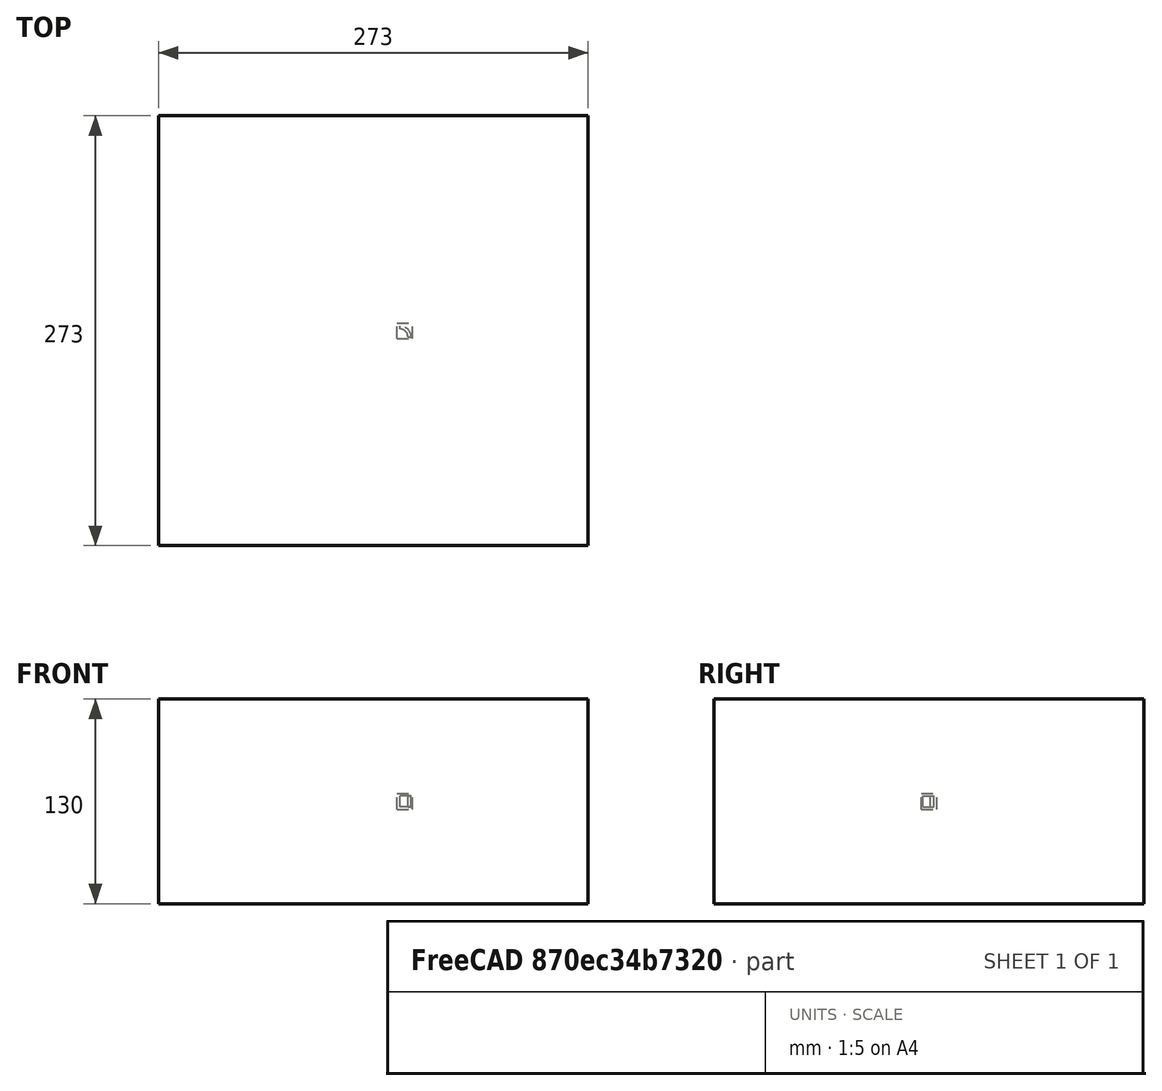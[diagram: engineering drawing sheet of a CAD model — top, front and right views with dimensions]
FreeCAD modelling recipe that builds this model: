
FCSTD DOCUMENT  (FreeCAD 0.21R33694 (Git))
Label: polarArray-of-Part-base-xformed
License: All rights reserved
LicenseURL: http://en.wikipedia.org/wiki/All_rights_reserved
objects: App::DocumentObjectGroupPython×1251, Part::FeaturePython×4, App::Part×4
note: 3 computed .brp shape members not serialized (recipe doc carries the construction recipe); baked Part::Feature solids carry a one-line shape summary decoded from their .brp

FEATURE [App::DocumentObjectGroupPython] HALFPI  # scripted group (container) (typed FeaturePython)
  name = HALFPI
  value = pi/2.
FEATURE [App::DocumentObjectGroupPython] PI  # scripted group (container) (typed FeaturePython)
  name = PI
  value = 1.*pi
FEATURE [App::DocumentObjectGroupPython] TWOPI  # scripted group (container) (typed FeaturePython)
  name = TWOPI
  value = 2.*pi
FEATURE [App::DocumentObjectGroupPython] Constants  # scripted group (container) (typed FeaturePython)
  Group = -> [HALFPI,PI,TWOPI]
FEATURE [App::DocumentObjectGroupPython] Variables  # scripted group (container) (typed FeaturePython)
FEATURE [App::DocumentObjectGroupPython] Quantities  # scripted group (container) (typed FeaturePython)
FEATURE [App::DocumentObjectGroupPython] Isotopes  # scripted group (container) (typed FeaturePython)
FEATURE [App::DocumentObjectGroupPython] Elements  # scripted group (container) (typed FeaturePython)
FEATURE [App::DocumentObjectGroupPython] Matrix  # scripted group (container) (typed FeaturePython)
FEATURE [App::DocumentObjectGroupPython] Surfaces  # scripted group (container) (typed FeaturePython)
FEATURE [App::DocumentObjectGroupPython] Opticals  # scripted group (container) (typed FeaturePython)
  Group = -> [Matrix,Surfaces]
FEATURE [App::DocumentObjectGroupPython] G4Isotopes  # scripted group (container) (typed FeaturePython)
FEATURE [App::DocumentObjectGroupPython] H_element  # scripted group (container) (typed FeaturePython)
  Z = 1
  atom_value = 1.008
  formula = H
  name = H_element
FEATURE [App::DocumentObjectGroupPython] He_element  # scripted group (container) (typed FeaturePython)
  Z = 2
  atom_value = 4.0026
  formula = He
  name = He_element
FEATURE [App::DocumentObjectGroupPython] Li_element  # scripted group (container) (typed FeaturePython)
  Z = 3
  atom_value = 6.94
  formula = Li
  name = Li_element
FEATURE [App::DocumentObjectGroupPython] Be_element  # scripted group (container) (typed FeaturePython)
  Z = 4
  atom_value = 9.01218
  formula = Be
  name = Be_element
FEATURE [App::DocumentObjectGroupPython] B_element  # scripted group (container) (typed FeaturePython)
  Z = 5
  atom_value = 10.81
  formula = B
  name = B_element
FEATURE [App::DocumentObjectGroupPython] C_element  # scripted group (container) (typed FeaturePython)
  Z = 6
  atom_value = 12.011
  formula = C
  name = C_element
FEATURE [App::DocumentObjectGroupPython] N_element  # scripted group (container) (typed FeaturePython)
  Z = 7
  atom_value = 14.007
  formula = N
  name = N_element
FEATURE [App::DocumentObjectGroupPython] O_element  # scripted group (container) (typed FeaturePython)
  Z = 8
  atom_value = 15.999
  formula = O
  name = O_element
FEATURE [App::DocumentObjectGroupPython] F_element  # scripted group (container) (typed FeaturePython)
  Z = 9
  atom_value = 18.9984
  formula = F
  name = F_element
FEATURE [App::DocumentObjectGroupPython] Ne_element  # scripted group (container) (typed FeaturePython)
  Z = 10
  atom_value = 20.1797
  formula = Ne
  name = Ne_element
FEATURE [App::DocumentObjectGroupPython] Na_element  # scripted group (container) (typed FeaturePython)
  Z = 11
  atom_value = 22.9898
  formula = Na
  name = Na_element
FEATURE [App::DocumentObjectGroupPython] Mg_element  # scripted group (container) (typed FeaturePython)
  Z = 12
  atom_value = 24.305
  formula = Mg
  name = Mg_element
FEATURE [App::DocumentObjectGroupPython] Al_element  # scripted group (container) (typed FeaturePython)
  Z = 13
  atom_value = 26.9815
  formula = Al
  name = Al_element
FEATURE [App::DocumentObjectGroupPython] Si_element  # scripted group (container) (typed FeaturePython)
  Z = 14
  atom_value = 28.085
  formula = Si
  name = Si_element
FEATURE [App::DocumentObjectGroupPython] P_element  # scripted group (container) (typed FeaturePython)
  Z = 15
  atom_value = 30.9738
  formula = P
  name = P_element
FEATURE [App::DocumentObjectGroupPython] S_element  # scripted group (container) (typed FeaturePython)
  Z = 16
  atom_value = 32.06
  formula = S
  name = S_element
FEATURE [App::DocumentObjectGroupPython] Cl_element  # scripted group (container) (typed FeaturePython)
  Z = 17
  atom_value = 35.45
  formula = Cl
  name = Cl_element
FEATURE [App::DocumentObjectGroupPython] Ar_element  # scripted group (container) (typed FeaturePython)
  Z = 18
  atom_value = 39.95
  formula = Ar
  name = Ar_element
FEATURE [App::DocumentObjectGroupPython] K_element  # scripted group (container) (typed FeaturePython)
  Z = 19
  atom_value = 39.0983
  formula = K
  name = K_element
FEATURE [App::DocumentObjectGroupPython] Ca_element  # scripted group (container) (typed FeaturePython)
  Z = 20
  atom_value = 40.078
  formula = Ca
  name = Ca_element
FEATURE [App::DocumentObjectGroupPython] Sc_element  # scripted group (container) (typed FeaturePython)
  Z = 21
  atom_value = 44.9559
  formula = Sc
  name = Sc_element
FEATURE [App::DocumentObjectGroupPython] Ti_element  # scripted group (container) (typed FeaturePython)
  Z = 22
  atom_value = 47.867
  formula = Ti
  name = Ti_element
FEATURE [App::DocumentObjectGroupPython] V_element  # scripted group (container) (typed FeaturePython)
  Z = 23
  atom_value = 50.9415
  formula = V
  name = V_element
FEATURE [App::DocumentObjectGroupPython] Cr_element  # scripted group (container) (typed FeaturePython)
  Z = 24
  atom_value = 51.9961
  formula = Cr
  name = Cr_element
FEATURE [App::DocumentObjectGroupPython] Mn_element  # scripted group (container) (typed FeaturePython)
  Z = 25
  atom_value = 54.938
  formula = Mn
  name = Mn_element
FEATURE [App::DocumentObjectGroupPython] Fe_element  # scripted group (container) (typed FeaturePython)
  Z = 26
  atom_value = 55.845
  formula = Fe
  name = Fe_element
FEATURE [App::DocumentObjectGroupPython] Co_element  # scripted group (container) (typed FeaturePython)
  Z = 27
  atom_value = 58.9332
  formula = Co
  name = Co_element
FEATURE [App::DocumentObjectGroupPython] Ni_element  # scripted group (container) (typed FeaturePython)
  Z = 28
  atom_value = 58.6934
  formula = Ni
  name = Ni_element
FEATURE [App::DocumentObjectGroupPython] Cu_element  # scripted group (container) (typed FeaturePython)
  Z = 29
  atom_value = 63.546
  formula = Cu
  name = Cu_element
FEATURE [App::DocumentObjectGroupPython] Zn_element  # scripted group (container) (typed FeaturePython)
  Z = 30
  atom_value = 65.38
  formula = Zn
  name = Zn_element
FEATURE [App::DocumentObjectGroupPython] Ga_element  # scripted group (container) (typed FeaturePython)
  Z = 31
  atom_value = 69.723
  formula = Ga
  name = Ga_element
FEATURE [App::DocumentObjectGroupPython] Ge_element  # scripted group (container) (typed FeaturePython)
  Z = 32
  atom_value = 72.63
  formula = Ge
  name = Ge_element
FEATURE [App::DocumentObjectGroupPython] As_element  # scripted group (container) (typed FeaturePython)
  Z = 33
  atom_value = 74.9216
  formula = As
  name = As_element
FEATURE [App::DocumentObjectGroupPython] Se_element  # scripted group (container) (typed FeaturePython)
  Z = 34
  atom_value = 78.971
  formula = Se
  name = Se_element
FEATURE [App::DocumentObjectGroupPython] Br_element  # scripted group (container) (typed FeaturePython)
  Z = 35
  atom_value = 79.904
  formula = Br
  name = Br_element
FEATURE [App::DocumentObjectGroupPython] Kr_element  # scripted group (container) (typed FeaturePython)
  Z = 36
  atom_value = 83.798
  formula = Kr
  name = Kr_element
FEATURE [App::DocumentObjectGroupPython] Rb_element  # scripted group (container) (typed FeaturePython)
  Z = 37
  atom_value = 85.4678
  formula = Rb
  name = Rb_element
FEATURE [App::DocumentObjectGroupPython] Sr_element  # scripted group (container) (typed FeaturePython)
  Z = 38
  atom_value = 87.62
  formula = Sr
  name = Sr_element
FEATURE [App::DocumentObjectGroupPython] Y_element  # scripted group (container) (typed FeaturePython)
  Z = 39
  atom_value = 88.9058
  formula = Y
  name = Y_element
FEATURE [App::DocumentObjectGroupPython] Zr_element  # scripted group (container) (typed FeaturePython)
  Z = 40
  atom_value = 91.224
  formula = Zr
  name = Zr_element
FEATURE [App::DocumentObjectGroupPython] Nb_element  # scripted group (container) (typed FeaturePython)
  Z = 41
  atom_value = 92.9064
  formula = Nb
  name = Nb_element
FEATURE [App::DocumentObjectGroupPython] Mo_element  # scripted group (container) (typed FeaturePython)
  Z = 42
  atom_value = 95.95
  formula = Mo
  name = Mo_element
FEATURE [App::DocumentObjectGroupPython] Tc_element  # scripted group (container) (typed FeaturePython)
  Z = 43
  atom_value = 97
  formula = Tc
  name = Tc_element
FEATURE [App::DocumentObjectGroupPython] Ru_element  # scripted group (container) (typed FeaturePython)
  Z = 44
  atom_value = 101.07
  formula = Ru
  name = Ru_element
FEATURE [App::DocumentObjectGroupPython] Rh_element  # scripted group (container) (typed FeaturePython)
  Z = 45
  atom_value = 102.905
  formula = Rh
  name = Rh_element
FEATURE [App::DocumentObjectGroupPython] Pd_element  # scripted group (container) (typed FeaturePython)
  Z = 46
  atom_value = 106.42
  formula = Pd
  name = Pd_element
FEATURE [App::DocumentObjectGroupPython] Ag_element  # scripted group (container) (typed FeaturePython)
  Z = 47
  atom_value = 107.868
  formula = Ag
  name = Ag_element
FEATURE [App::DocumentObjectGroupPython] Cd_element  # scripted group (container) (typed FeaturePython)
  Z = 48
  atom_value = 112.414
  formula = Cd
  name = Cd_element
FEATURE [App::DocumentObjectGroupPython] In_element  # scripted group (container) (typed FeaturePython)
  Z = 49
  atom_value = 114.818
  formula = In
  name = In_element
FEATURE [App::DocumentObjectGroupPython] Sn_element  # scripted group (container) (typed FeaturePython)
  Z = 50
  atom_value = 118.71
  formula = Sn
  name = Sn_element
FEATURE [App::DocumentObjectGroupPython] Sb_element  # scripted group (container) (typed FeaturePython)
  Z = 51
  atom_value = 121.76
  formula = Sb
  name = Sb_element
FEATURE [App::DocumentObjectGroupPython] Te_element  # scripted group (container) (typed FeaturePython)
  Z = 52
  atom_value = 127.6
  formula = Te
  name = Te_element
FEATURE [App::DocumentObjectGroupPython] I_element  # scripted group (container) (typed FeaturePython)
  Z = 53
  atom_value = 126.904
  formula = I
  name = I_element
FEATURE [App::DocumentObjectGroupPython] Xe_element  # scripted group (container) (typed FeaturePython)
  Z = 54
  atom_value = 131.293
  formula = Xe
  name = Xe_element
FEATURE [App::DocumentObjectGroupPython] Cs_element  # scripted group (container) (typed FeaturePython)
  Z = 55
  atom_value = 132.905
  formula = Cs
  name = Cs_element
FEATURE [App::DocumentObjectGroupPython] Ba_element  # scripted group (container) (typed FeaturePython)
  Z = 56
  atom_value = 137.327
  formula = Ba
  name = Ba_element
FEATURE [App::DocumentObjectGroupPython] La_element  # scripted group (container) (typed FeaturePython)
  Z = 57
  atom_value = 138.905
  formula = La
  name = La_element
FEATURE [App::DocumentObjectGroupPython] Ce_element  # scripted group (container) (typed FeaturePython)
  Z = 58
  atom_value = 140.116
  formula = Ce
  name = Ce_element
FEATURE [App::DocumentObjectGroupPython] Pr_element  # scripted group (container) (typed FeaturePython)
  Z = 59
  atom_value = 140.908
  formula = Pr
  name = Pr_element
FEATURE [App::DocumentObjectGroupPython] Nd_element  # scripted group (container) (typed FeaturePython)
  Z = 60
  atom_value = 144.242
  formula = Nd
  name = Nd_element
FEATURE [App::DocumentObjectGroupPython] Pm_element  # scripted group (container) (typed FeaturePython)
  Z = 61
  atom_value = 145
  formula = Pm
  name = Pm_element
FEATURE [App::DocumentObjectGroupPython] Sm_element  # scripted group (container) (typed FeaturePython)
  Z = 62
  atom_value = 150.36
  formula = Sm
  name = Sm_element
FEATURE [App::DocumentObjectGroupPython] Eu_element  # scripted group (container) (typed FeaturePython)
  Z = 63
  atom_value = 151.964
  formula = Eu
  name = Eu_element
FEATURE [App::DocumentObjectGroupPython] Gd_element  # scripted group (container) (typed FeaturePython)
  Z = 64
  atom_value = 157.25
  formula = Gd
  name = Gd_element
FEATURE [App::DocumentObjectGroupPython] Tb_element  # scripted group (container) (typed FeaturePython)
  Z = 65
  atom_value = 158.925
  formula = Tb
  name = Tb_element
FEATURE [App::DocumentObjectGroupPython] Dy_element  # scripted group (container) (typed FeaturePython)
  Z = 66
  atom_value = 162.5
  formula = Dy
  name = Dy_element
FEATURE [App::DocumentObjectGroupPython] Ho_element  # scripted group (container) (typed FeaturePython)
  Z = 67
  atom_value = 164.93
  formula = Ho
  name = Ho_element
FEATURE [App::DocumentObjectGroupPython] Er_element  # scripted group (container) (typed FeaturePython)
  Z = 68
  atom_value = 167.259
  formula = Er
  name = Er_element
FEATURE [App::DocumentObjectGroupPython] Tm_element  # scripted group (container) (typed FeaturePython)
  Z = 69
  atom_value = 168.934
  formula = Tm
  name = Tm_element
FEATURE [App::DocumentObjectGroupPython] Yb_element  # scripted group (container) (typed FeaturePython)
  Z = 70
  atom_value = 173.045
  formula = Yb
  name = Yb_element
FEATURE [App::DocumentObjectGroupPython] Lu_element  # scripted group (container) (typed FeaturePython)
  Z = 71
  atom_value = 174.967
  formula = Lu
  name = Lu_element
FEATURE [App::DocumentObjectGroupPython] Hf_element  # scripted group (container) (typed FeaturePython)
  Z = 72
  atom_value = 178.49
  formula = Hf
  name = Hf_element
FEATURE [App::DocumentObjectGroupPython] Ta_element  # scripted group (container) (typed FeaturePython)
  Z = 73
  atom_value = 180.948
  formula = Ta
  name = Ta_element
FEATURE [App::DocumentObjectGroupPython] W_element  # scripted group (container) (typed FeaturePython)
  Z = 74
  atom_value = 183.84
  formula = W
  name = W_element
FEATURE [App::DocumentObjectGroupPython] Re_element  # scripted group (container) (typed FeaturePython)
  Z = 75
  atom_value = 186.207
  formula = Re
  name = Re_element
FEATURE [App::DocumentObjectGroupPython] Os_element  # scripted group (container) (typed FeaturePython)
  Z = 76
  atom_value = 190.23
  formula = Os
  name = Os_element
FEATURE [App::DocumentObjectGroupPython] Ir_element  # scripted group (container) (typed FeaturePython)
  Z = 77
  atom_value = 192.217
  formula = Ir
  name = Ir_element
FEATURE [App::DocumentObjectGroupPython] Pt_element  # scripted group (container) (typed FeaturePython)
  Z = 78
  atom_value = 195.084
  formula = Pt
  name = Pt_element
FEATURE [App::DocumentObjectGroupPython] Au_element  # scripted group (container) (typed FeaturePython)
  Z = 79
  atom_value = 196.967
  formula = Au
  name = Au_element
FEATURE [App::DocumentObjectGroupPython] Hg_element  # scripted group (container) (typed FeaturePython)
  Z = 80
  atom_value = 200.592
  formula = Hg
  name = Hg_element
FEATURE [App::DocumentObjectGroupPython] Tl_element  # scripted group (container) (typed FeaturePython)
  Z = 81
  atom_value = 204.38
  formula = Tl
  name = Tl_element
FEATURE [App::DocumentObjectGroupPython] Pb_element  # scripted group (container) (typed FeaturePython)
  Z = 82
  atom_value = 207.2
  formula = Pb
  name = Pb_element
FEATURE [App::DocumentObjectGroupPython] Bi_element  # scripted group (container) (typed FeaturePython)
  Z = 83
  atom_value = 208.98
  formula = Bi
  name = Bi_element
FEATURE [App::DocumentObjectGroupPython] Po_element  # scripted group (container) (typed FeaturePython)
  Z = 84
  atom_value = 209
  formula = Po
  name = Po_element
FEATURE [App::DocumentObjectGroupPython] At_element  # scripted group (container) (typed FeaturePython)
  Z = 85
  atom_value = 210
  formula = At
  name = At_element
FEATURE [App::DocumentObjectGroupPython] Rn_element  # scripted group (container) (typed FeaturePython)
  Z = 86
  atom_value = 222
  formula = Rn
  name = Rn_element
FEATURE [App::DocumentObjectGroupPython] Fr_element  # scripted group (container) (typed FeaturePython)
  Z = 87
  atom_value = 223
  formula = Fr
  name = Fr_element
FEATURE [App::DocumentObjectGroupPython] Ra_element  # scripted group (container) (typed FeaturePython)
  Z = 88
  atom_value = 226
  formula = Ra
  name = Ra_element
FEATURE [App::DocumentObjectGroupPython] Ac_element  # scripted group (container) (typed FeaturePython)
  Z = 89
  atom_value = 227
  formula = Ac
  name = Ac_element
FEATURE [App::DocumentObjectGroupPython] Th_element  # scripted group (container) (typed FeaturePython)
  Z = 90
  atom_value = 232.038
  formula = Th
  name = Th_element
FEATURE [App::DocumentObjectGroupPython] Pa_element  # scripted group (container) (typed FeaturePython)
  Z = 91
  atom_value = 231.036
  formula = Pa
  name = Pa_element
FEATURE [App::DocumentObjectGroupPython] U_element  # scripted group (container) (typed FeaturePython)
  Z = 92
  atom_value = 238.029
  formula = U
  name = U_element
FEATURE [App::DocumentObjectGroupPython] Np_element  # scripted group (container) (typed FeaturePython)
  Z = 93
  atom_value = 237
  formula = Np
  name = Np_element
FEATURE [App::DocumentObjectGroupPython] Pu_element  # scripted group (container) (typed FeaturePython)
  Z = 94
  atom_value = 244
  formula = Pu
  name = Pu_element
FEATURE [App::DocumentObjectGroupPython] Am_element  # scripted group (container) (typed FeaturePython)
  Z = 95
  atom_value = 243
  formula = Am
  name = Am_element
FEATURE [App::DocumentObjectGroupPython] Cm_element  # scripted group (container) (typed FeaturePython)
  Z = 96
  atom_value = 247
  formula = Cm
  name = Cm_element
FEATURE [App::DocumentObjectGroupPython] Bk_element  # scripted group (container) (typed FeaturePython)
  Z = 97
  atom_value = 247
  formula = Bk
  name = Bk_element
FEATURE [App::DocumentObjectGroupPython] Cf_element  # scripted group (container) (typed FeaturePython)
  Z = 98
  atom_value = 251
  formula = Cf
  name = Cf_element
FEATURE [App::DocumentObjectGroupPython] G4Elements  # scripted group (container) (typed FeaturePython)
  Group = -> [H_element,He_element,Li_element,Be_element,B_element,C_element,N_element,O_element,F_element,Ne_element,Na_element,Mg_element,Al_element,Si_element,P_element,S_element,Cl_element,Ar_element,K_element,Ca_element,Sc_element,Ti_element,V_element,Cr_element,Mn_element,Fe_element,Co_element,Ni_element,Cu_element,Zn_element,Ga_element,Ge_element,As_element,Se_element,Br_element,Kr_element,Rb_element,+61 more]
FEATURE [App::DocumentObjectGroupPython] H_element001  label="H_element : 0.101"  # scripted group (container) (typed FeaturePython)
  n = 0.101327
FEATURE [App::DocumentObjectGroupPython] C_element001  label="C_element : 0.775"  # scripted group (container) (typed FeaturePython)
  n = 0.7755
FEATURE [App::DocumentObjectGroupPython] N_element001  label="N_element : 0.035"  # scripted group (container) (typed FeaturePython)
  n = 0.035057
FEATURE [App::DocumentObjectGroupPython] O_element001  label="O_element : 0.052"  # scripted group (container) (typed FeaturePython)
  n = 0.0523159
FEATURE [App::DocumentObjectGroupPython] F_element001  label="F_element : 0.017"  # scripted group (container) (typed FeaturePython)
  n = 0.017422
FEATURE [App::DocumentObjectGroupPython] Ca_element001  label="Ca_element : 0.018"  # scripted group (container) (typed FeaturePython)
  n = 0.018378
FEATURE [App::DocumentObjectGroupPython] G4_A_150_TISSUE  label="G4_A-150_TISSUE"  # scripted group (container) (typed FeaturePython)
  Dunit = g/cm3
  Dvalue = 1.127
  Group = -> [H_element001,C_element001,N_element001,O_element001,F_element001,Ca_element001]
  conduct = 2
  density = 1
  expand = 3
  formula = G4_A-150_TISSUE
  name = G4_A-150_TISSUE
  specific = 4
FEATURE [App::DocumentObjectGroupPython] C_element002  label="C_element : 3"  # scripted group (container) (typed FeaturePython)
  n = 3
  ref = C_element
FEATURE [App::DocumentObjectGroupPython] H_element002  label="H_element : 6"  # scripted group (container) (typed FeaturePython)
  n = 6
  ref = H_element
FEATURE [App::DocumentObjectGroupPython] O_element002  label="O_element : 1"  # scripted group (container) (typed FeaturePython)
  n = 1
  ref = O_element
FEATURE [App::DocumentObjectGroupPython] G4_ACETONE  # scripted group (container) (typed FeaturePython)
  Dunit = g/cm3
  Dvalue = 0.7899
  Group = -> [C_element002,H_element002,O_element002]
  conduct = 2
  density = 1
  expand = 3
  formula = G4_ACETONE
  name = G4_ACETONE
  specific = 4
FEATURE [App::DocumentObjectGroupPython] C_element003  label="C_element : 2"  # scripted group (container) (typed FeaturePython)
  n = 2
  ref = C_element
FEATURE [App::DocumentObjectGroupPython] H_element003  label="H_element : 2"  # scripted group (container) (typed FeaturePython)
  n = 2
  ref = H_element
FEATURE [App::DocumentObjectGroupPython] G4_ACETYLENE  # scripted group (container) (typed FeaturePython)
  Dunit = g/cm3
  Dvalue = 0.0010967
  Group = -> [C_element003,H_element003]
  conduct = 2
  density = 1
  expand = 3
  formula = G4_ACETYLENE
  name = G4_ACETYLENE
  specific = 4
FEATURE [App::DocumentObjectGroupPython] C_element004  label="C_element : 5"  # scripted group (container) (typed FeaturePython)
  n = 5
  ref = C_element
FEATURE [App::DocumentObjectGroupPython] H_element004  label="H_element : 5"  # scripted group (container) (typed FeaturePython)
  n = 5
  ref = H_element
FEATURE [App::DocumentObjectGroupPython] N_element002  label="N_element : 5"  # scripted group (container) (typed FeaturePython)
  n = 5
  ref = N_element
FEATURE [App::DocumentObjectGroupPython] G4_ADENINE  # scripted group (container) (typed FeaturePython)
  Dunit = g/cm3
  Dvalue = 1.6
  Group = -> [C_element004,H_element004,N_element002]
  conduct = 2
  density = 1
  expand = 3
  formula = G4_ADENINE
  name = G4_ADENINE
  specific = 4
FEATURE [App::DocumentObjectGroupPython] H_element005  label="H_element : 0.114"  # scripted group (container) (typed FeaturePython)
  n = 0.114
FEATURE [App::DocumentObjectGroupPython] C_element005  label="C_element : 0.598"  # scripted group (container) (typed FeaturePython)
  n = 0.598
FEATURE [App::DocumentObjectGroupPython] N_element003  label="N_element : 0.007"  # scripted group (container) (typed FeaturePython)
  n = 0.007
FEATURE [App::DocumentObjectGroupPython] O_element003  label="O_element : 0.278"  # scripted group (container) (typed FeaturePython)
  n = 0.278
FEATURE [App::DocumentObjectGroupPython] Na_element001  label="Na_element : 0.001"  # scripted group (container) (typed FeaturePython)
  n = 0.001
FEATURE [App::DocumentObjectGroupPython] S_element001  label="S_element : 0.001"  # scripted group (container) (typed FeaturePython)
  n = 0.001
FEATURE [App::DocumentObjectGroupPython] Cl_element001  label="Cl_element : 0.001"  # scripted group (container) (typed FeaturePython)
  n = 0.001
FEATURE [App::DocumentObjectGroupPython] G4_ADIPOSE_TISSUE_ICRP  # scripted group (container) (typed FeaturePython)
  Dunit = g/cm3
  Dvalue = 0.95
  Group = -> [H_element005,C_element005,N_element003,O_element003,Na_element001,S_element001,Cl_element001]
  conduct = 2
  density = 1
  expand = 3
  formula = G4_ADIPOSE_TISSUE_ICRP
  name = G4_ADIPOSE_TISSUE_ICRP
  specific = 4
FEATURE [App::DocumentObjectGroupPython] C_element006  label="C_element : 0.000"  # scripted group (container) (typed FeaturePython)
  n = 0.000124
FEATURE [App::DocumentObjectGroupPython] N_element004  label="N_element : 0.755"  # scripted group (container) (typed FeaturePython)
  n = 0.755268
FEATURE [App::DocumentObjectGroupPython] O_element004  label="O_element : 0.232"  # scripted group (container) (typed FeaturePython)
  n = 0.231781
FEATURE [App::DocumentObjectGroupPython] Ar_element001  label="Ar_element : 0.013"  # scripted group (container) (typed FeaturePython)
  n = 0.012827
FEATURE [App::DocumentObjectGroupPython] G4_AIR  # scripted group (container) (typed FeaturePython)
  Dunit = g/cm3
  Dvalue = 0.00120479
  Group = -> [C_element006,N_element004,O_element004,Ar_element001]
  conduct = 2
  density = 1
  expand = 3
  formula = G4_AIR
  name = G4_AIR
  specific = 4
FEATURE [App::DocumentObjectGroupPython] C_element007  label="C_element : 006"  # scripted group (container) (typed FeaturePython)
  n = 3
  ref = C_element
FEATURE [App::DocumentObjectGroupPython] H_element006  label="H_element : 7"  # scripted group (container) (typed FeaturePython)
  n = 7
  ref = H_element
FEATURE [App::DocumentObjectGroupPython] N_element005  label="N_element : 1"  # scripted group (container) (typed FeaturePython)
  n = 1
  ref = N_element
FEATURE [App::DocumentObjectGroupPython] O_element005  label="O_element : 2"  # scripted group (container) (typed FeaturePython)
  n = 2
  ref = O_element
FEATURE [App::DocumentObjectGroupPython] G4_ALANINE  # scripted group (container) (typed FeaturePython)
  Dunit = g/cm3
  Dvalue = 1.42
  Group = -> [C_element007,H_element006,N_element005,O_element005]
  conduct = 2
  density = 1
  expand = 3
  formula = G4_ALANINE
  name = G4_ALANINE
  specific = 4
FEATURE [App::DocumentObjectGroupPython] Al_element001  label="Al_element : 2"  # scripted group (container) (typed FeaturePython)
  n = 2
  ref = Al_element
FEATURE [App::DocumentObjectGroupPython] O_element006  label="O_element : 3"  # scripted group (container) (typed FeaturePython)
  n = 3
  ref = O_element
FEATURE [App::DocumentObjectGroupPython] G4_ALUMINUM_OXIDE  # scripted group (container) (typed FeaturePython)
  Dunit = g/cm3
  Dvalue = 3.97
  Group = -> [Al_element001,O_element006]
  conduct = 2
  density = 1
  expand = 3
  formula = G4_ALUMINUM_OXIDE
  name = G4_ALUMINUM_OXIDE
  specific = 4
FEATURE [App::DocumentObjectGroupPython] H_element007  label="H_element : 0.106"  # scripted group (container) (typed FeaturePython)
  n = 0.10593
FEATURE [App::DocumentObjectGroupPython] C_element008  label="C_element : 0.789"  # scripted group (container) (typed FeaturePython)
  n = 0.788974
FEATURE [App::DocumentObjectGroupPython] O_element007  label="O_element : 0.105"  # scripted group (container) (typed FeaturePython)
  n = 0.105096
FEATURE [App::DocumentObjectGroupPython] G4_AMBER  # scripted group (container) (typed FeaturePython)
  Dunit = g/cm3
  Dvalue = 1.1
  Group = -> [H_element007,C_element008,O_element007]
  conduct = 2
  density = 1
  expand = 3
  formula = G4_AMBER
  name = G4_AMBER
  specific = 4
FEATURE [App::DocumentObjectGroupPython] N_element006  label="N_element : 006"  # scripted group (container) (typed FeaturePython)
  n = 1
  ref = N_element
FEATURE [App::DocumentObjectGroupPython] H_element008  label="H_element : 3"  # scripted group (container) (typed FeaturePython)
  n = 3
  ref = H_element
FEATURE [App::DocumentObjectGroupPython] G4_AMMONIA  # scripted group (container) (typed FeaturePython)
  Dunit = g/cm3
  Dvalue = 0.000826019
  Group = -> [N_element006,H_element008]
  conduct = 2
  density = 1
  expand = 3
  formula = G4_AMMONIA
  name = G4_AMMONIA
  specific = 4
FEATURE [App::DocumentObjectGroupPython] C_element009  label="C_element : 6"  # scripted group (container) (typed FeaturePython)
  n = 6
  ref = C_element
FEATURE [App::DocumentObjectGroupPython] H_element009  label="H_element : 008"  # scripted group (container) (typed FeaturePython)
  n = 7
  ref = H_element
FEATURE [App::DocumentObjectGroupPython] N_element007  label="N_element : 007"  # scripted group (container) (typed FeaturePython)
  n = 1
  ref = N_element
FEATURE [App::DocumentObjectGroupPython] G4_ANILINE  # scripted group (container) (typed FeaturePython)
  Dunit = g/cm3
  Dvalue = 1.0235
  Group = -> [C_element009,H_element009,N_element007]
  conduct = 2
  density = 1
  expand = 3
  formula = G4_ANILINE
  name = G4_ANILINE
  specific = 4
FEATURE [App::DocumentObjectGroupPython] C_element010  label="C_element : 14"  # scripted group (container) (typed FeaturePython)
  n = 14
  ref = C_element
FEATURE [App::DocumentObjectGroupPython] H_element010  label="H_element : 10"  # scripted group (container) (typed FeaturePython)
  n = 10
  ref = H_element
FEATURE [App::DocumentObjectGroupPython] G4_ANTHRACENE  # scripted group (container) (typed FeaturePython)
  Dunit = g/cm3
  Dvalue = 1.283
  Group = -> [C_element010,H_element010]
  conduct = 2
  density = 1
  expand = 3
  formula = G4_ANTHRACENE
  name = G4_ANTHRACENE
  specific = 4
FEATURE [App::DocumentObjectGroupPython] H_element011  label="H_element : 0.065"  # scripted group (container) (typed FeaturePython)
  n = 0.0654709
FEATURE [App::DocumentObjectGroupPython] C_element011  label="C_element : 0.537"  # scripted group (container) (typed FeaturePython)
  n = 0.536944
FEATURE [App::DocumentObjectGroupPython] N_element008  label="N_element : 0.021"  # scripted group (container) (typed FeaturePython)
  n = 0.0215
FEATURE [App::DocumentObjectGroupPython] O_element008  label="O_element : 0.032"  # scripted group (container) (typed FeaturePython)
  n = 0.032085
FEATURE [App::DocumentObjectGroupPython] F_element002  label="F_element : 0.167"  # scripted group (container) (typed FeaturePython)
  n = 0.167411
FEATURE [App::DocumentObjectGroupPython] Ca_element002  label="Ca_element : 0.177"  # scripted group (container) (typed FeaturePython)
  n = 0.176589
FEATURE [App::DocumentObjectGroupPython] G4_B_100_BONE  label="G4_B-100_BONE"  # scripted group (container) (typed FeaturePython)
  Dunit = g/cm3
  Dvalue = 1.45
  Group = -> [H_element011,C_element011,N_element008,O_element008,F_element002,Ca_element002]
  conduct = 2
  density = 1
  expand = 3
  formula = G4_B-100_BONE
  name = G4_B-100_BONE
  specific = 4
FEATURE [App::DocumentObjectGroupPython] H_element012  label="H_element : 0.057"  # scripted group (container) (typed FeaturePython)
  n = 0.057441
FEATURE [App::DocumentObjectGroupPython] C_element012  label="C_element : 0.790"  # scripted group (container) (typed FeaturePython)
  n = 0.774591
FEATURE [App::DocumentObjectGroupPython] O_element009  label="O_element : 0.168"  # scripted group (container) (typed FeaturePython)
  n = 0.167968
FEATURE [App::DocumentObjectGroupPython] G4_BAKELITE  # scripted group (container) (typed FeaturePython)
  Dunit = g/cm3
  Dvalue = 1.25
  Group = -> [H_element012,C_element012,O_element009]
  conduct = 2
  density = 1
  expand = 3
  formula = G4_BAKELITE
  name = G4_BAKELITE
  specific = 4
FEATURE [App::DocumentObjectGroupPython] Ba_element001  label="Ba_element : 1"  # scripted group (container) (typed FeaturePython)
  n = 1
  ref = Ba_element
FEATURE [App::DocumentObjectGroupPython] F_element003  label="F_element : 2"  # scripted group (container) (typed FeaturePython)
  n = 2
  ref = F_element
FEATURE [App::DocumentObjectGroupPython] G4_BARIUM_FLUORIDE  # scripted group (container) (typed FeaturePython)
  Dunit = g/cm3
  Dvalue = 4.89
  Group = -> [Ba_element001,F_element003]
  conduct = 2
  density = 1
  expand = 3
  formula = G4_BARIUM_FLUORIDE
  name = G4_BARIUM_FLUORIDE
  specific = 4
FEATURE [App::DocumentObjectGroupPython] Ba_element002  label="Ba_element : 002"  # scripted group (container) (typed FeaturePython)
  n = 1
  ref = Ba_element
FEATURE [App::DocumentObjectGroupPython] S_element002  label="S_element : 1"  # scripted group (container) (typed FeaturePython)
  n = 1
  ref = S_element
FEATURE [App::DocumentObjectGroupPython] O_element010  label="O_element : 4"  # scripted group (container) (typed FeaturePython)
  n = 4
  ref = O_element
FEATURE [App::DocumentObjectGroupPython] G4_BARIUM_SULFATE  # scripted group (container) (typed FeaturePython)
  Dunit = g/cm3
  Dvalue = 4.5
  Group = -> [Ba_element002,S_element002,O_element010]
  conduct = 2
  density = 1
  expand = 3
  formula = G4_BARIUM_SULFATE
  name = G4_BARIUM_SULFATE
  specific = 4
FEATURE [App::DocumentObjectGroupPython] C_element013  label="C_element : 007"  # scripted group (container) (typed FeaturePython)
  n = 6
  ref = C_element
FEATURE [App::DocumentObjectGroupPython] H_element013  label="H_element : 009"  # scripted group (container) (typed FeaturePython)
  n = 6
  ref = H_element
FEATURE [App::DocumentObjectGroupPython] G4_BENZENE  # scripted group (container) (typed FeaturePython)
  Dunit = g/cm3
  Dvalue = 0.87865
  Group = -> [C_element013,H_element013]
  conduct = 2
  density = 1
  expand = 3
  formula = G4_BENZENE
  name = G4_BENZENE
  specific = 4
FEATURE [App::DocumentObjectGroupPython] Be_element001  label="Be_element : 1"  # scripted group (container) (typed FeaturePython)
  n = 1
  ref = Be_element
FEATURE [App::DocumentObjectGroupPython] O_element011  label="O_element : 005"  # scripted group (container) (typed FeaturePython)
  n = 1
  ref = O_element
FEATURE [App::DocumentObjectGroupPython] G4_BERYLLIUM_OXIDE  # scripted group (container) (typed FeaturePython)
  Dunit = g/cm3
  Dvalue = 3.01
  Group = -> [Be_element001,O_element011]
  conduct = 2
  density = 1
  expand = 3
  formula = G4_BERYLLIUM_OXIDE
  name = G4_BERYLLIUM_OXIDE
  specific = 4
FEATURE [App::DocumentObjectGroupPython] Bi_element001  label="Bi_element : 4"  # scripted group (container) (typed FeaturePython)
  n = 4
  ref = Bi_element
FEATURE [App::DocumentObjectGroupPython] Ge_element001  label="Ge_element : 3"  # scripted group (container) (typed FeaturePython)
  n = 3
  ref = Ge_element
FEATURE [App::DocumentObjectGroupPython] O_element012  label="O_element : 12"  # scripted group (container) (typed FeaturePython)
  n = 12
  ref = O_element
FEATURE [App::DocumentObjectGroupPython] G4_BGO  # scripted group (container) (typed FeaturePython)
  Dunit = g/cm3
  Dvalue = 7.13
  Group = -> [Bi_element001,Ge_element001,O_element012]
  conduct = 2
  density = 1
  expand = 3
  formula = G4_BGO
  name = G4_BGO
  specific = 4
FEATURE [App::DocumentObjectGroupPython] H_element014  label="H_element : 0.102"  # scripted group (container) (typed FeaturePython)
  n = 0.102
FEATURE [App::DocumentObjectGroupPython] C_element014  label="C_element : 0.110"  # scripted group (container) (typed FeaturePython)
  n = 0.11
FEATURE [App::DocumentObjectGroupPython] N_element009  label="N_element : 0.033"  # scripted group (container) (typed FeaturePython)
  n = 0.033
FEATURE [App::DocumentObjectGroupPython] O_element013  label="O_element : 0.745"  # scripted group (container) (typed FeaturePython)
  n = 0.745
FEATURE [App::DocumentObjectGroupPython] Na_element002  label="Na_element : 0.002"  # scripted group (container) (typed FeaturePython)
  n = 0.001
FEATURE [App::DocumentObjectGroupPython] P_element001  label="P_element : 0.001"  # scripted group (container) (typed FeaturePython)
  n = 0.001
FEATURE [App::DocumentObjectGroupPython] S_element003  label="S_element : 0.002"  # scripted group (container) (typed FeaturePython)
  n = 0.002
FEATURE [App::DocumentObjectGroupPython] Cl_element002  label="Cl_element : 0.003"  # scripted group (container) (typed FeaturePython)
  n = 0.003
FEATURE [App::DocumentObjectGroupPython] K_element001  label="K_element : 0.002"  # scripted group (container) (typed FeaturePython)
  n = 0.002
FEATURE [App::DocumentObjectGroupPython] Fe_element001  label="Fe_element : 0.001"  # scripted group (container) (typed FeaturePython)
  n = 0.001
FEATURE [App::DocumentObjectGroupPython] G4_BLOOD_ICRP  # scripted group (container) (typed FeaturePython)
  Dunit = g/cm3
  Dvalue = 1.06
  Group = -> [H_element014,C_element014,N_element009,O_element013,Na_element002,P_element001,S_element003,Cl_element002,K_element001,Fe_element001]
  conduct = 2
  density = 1
  expand = 3
  formula = G4_BLOOD_ICRP
  name = G4_BLOOD_ICRP
  specific = 4
FEATURE [App::DocumentObjectGroupPython] H_element015  label="H_element : 0.064"  # scripted group (container) (typed FeaturePython)
  n = 0.064
FEATURE [App::DocumentObjectGroupPython] C_element015  label="C_element : 0.278"  # scripted group (container) (typed FeaturePython)
  n = 0.278
FEATURE [App::DocumentObjectGroupPython] N_element010  label="N_element : 0.027"  # scripted group (container) (typed FeaturePython)
  n = 0.027
FEATURE [App::DocumentObjectGroupPython] O_element014  label="O_element : 0.410"  # scripted group (container) (typed FeaturePython)
  n = 0.41
FEATURE [App::DocumentObjectGroupPython] Mg_element001  label="Mg_element : 0.002"  # scripted group (container) (typed FeaturePython)
  n = 0.002
FEATURE [App::DocumentObjectGroupPython] P_element002  label="P_element : 0.070"  # scripted group (container) (typed FeaturePython)
  n = 0.07
FEATURE [App::DocumentObjectGroupPython] S_element004  label="S_element : 0.003"  # scripted group (container) (typed FeaturePython)
  n = 0.002
FEATURE [App::DocumentObjectGroupPython] Ca_element003  label="Ca_element : 0.147"  # scripted group (container) (typed FeaturePython)
  n = 0.147
FEATURE [App::DocumentObjectGroupPython] G4_BONE_COMPACT_ICRU  # scripted group (container) (typed FeaturePython)
  Dunit = g/cm3
  Dvalue = 1.85
  Group = -> [H_element015,C_element015,N_element010,O_element014,Mg_element001,P_element002,S_element004,Ca_element003]
  conduct = 2
  density = 1
  expand = 3
  formula = G4_BONE_COMPACT_ICRU
  name = G4_BONE_COMPACT_ICRU
  specific = 4
FEATURE [App::DocumentObjectGroupPython] H_element016  label="H_element : 0.034"  # scripted group (container) (typed FeaturePython)
  n = 0.034
FEATURE [App::DocumentObjectGroupPython] C_element016  label="C_element : 0.155"  # scripted group (container) (typed FeaturePython)
  n = 0.155
FEATURE [App::DocumentObjectGroupPython] N_element011  label="N_element : 0.042"  # scripted group (container) (typed FeaturePython)
  n = 0.042
FEATURE [App::DocumentObjectGroupPython] O_element015  label="O_element : 0.435"  # scripted group (container) (typed FeaturePython)
  n = 0.435
FEATURE [App::DocumentObjectGroupPython] Na_element003  label="Na_element : 0.003"  # scripted group (container) (typed FeaturePython)
  n = 0.001
FEATURE [App::DocumentObjectGroupPython] Mg_element002  label="Mg_element : 0.003"  # scripted group (container) (typed FeaturePython)
  n = 0.002
FEATURE [App::DocumentObjectGroupPython] P_element003  label="P_element : 0.103"  # scripted group (container) (typed FeaturePython)
  n = 0.103
FEATURE [App::DocumentObjectGroupPython] S_element005  label="S_element : 0.004"  # scripted group (container) (typed FeaturePython)
  n = 0.003
FEATURE [App::DocumentObjectGroupPython] Ca_element004  label="Ca_element : 0.225"  # scripted group (container) (typed FeaturePython)
  n = 0.225
FEATURE [App::DocumentObjectGroupPython] G4_BONE_CORTICAL_ICRP  # scripted group (container) (typed FeaturePython)
  Dunit = g/cm3
  Dvalue = 1.92
  Group = -> [H_element016,C_element016,N_element011,O_element015,Na_element003,Mg_element002,P_element003,S_element005,Ca_element004]
  conduct = 2
  density = 1
  expand = 3
  formula = G4_BONE_CORTICAL_ICRP
  name = G4_BONE_CORTICAL_ICRP
  specific = 4
FEATURE [App::DocumentObjectGroupPython] B_element001  label="B_element : 4"  # scripted group (container) (typed FeaturePython)
  n = 4
  ref = B_element
FEATURE [App::DocumentObjectGroupPython] C_element017  label="C_element : 1"  # scripted group (container) (typed FeaturePython)
  n = 1
  ref = C_element
FEATURE [App::DocumentObjectGroupPython] G4_BORON_CARBIDE  # scripted group (container) (typed FeaturePython)
  Dunit = g/cm3
  Dvalue = 2.52
  Group = -> [B_element001,C_element017]
  conduct = 2
  density = 1
  expand = 3
  formula = G4_BORON_CARBIDE
  name = G4_BORON_CARBIDE
  specific = 4
FEATURE [App::DocumentObjectGroupPython] B_element002  label="B_element : 2"  # scripted group (container) (typed FeaturePython)
  n = 2
  ref = B_element
FEATURE [App::DocumentObjectGroupPython] O_element016  label="O_element : 006"  # scripted group (container) (typed FeaturePython)
  n = 3
  ref = O_element
FEATURE [App::DocumentObjectGroupPython] G4_BORON_OXIDE  # scripted group (container) (typed FeaturePython)
  Dunit = g/cm3
  Dvalue = 1.812
  Group = -> [B_element002,O_element016]
  conduct = 2
  density = 1
  expand = 3
  formula = G4_BORON_OXIDE
  name = G4_BORON_OXIDE
  specific = 4
FEATURE [App::DocumentObjectGroupPython] H_element017  label="H_element : 0.107"  # scripted group (container) (typed FeaturePython)
  n = 0.107
FEATURE [App::DocumentObjectGroupPython] C_element018  label="C_element : 0.145"  # scripted group (container) (typed FeaturePython)
  n = 0.145
FEATURE [App::DocumentObjectGroupPython] N_element012  label="N_element : 0.022"  # scripted group (container) (typed FeaturePython)
  n = 0.022
FEATURE [App::DocumentObjectGroupPython] O_element017  label="O_element : 0.712"  # scripted group (container) (typed FeaturePython)
  n = 0.712
FEATURE [App::DocumentObjectGroupPython] Na_element004  label="Na_element : 0.004"  # scripted group (container) (typed FeaturePython)
  n = 0.002
FEATURE [App::DocumentObjectGroupPython] P_element004  label="P_element : 0.004"  # scripted group (container) (typed FeaturePython)
  n = 0.004
FEATURE [App::DocumentObjectGroupPython] S_element006  label="S_element : 0.005"  # scripted group (container) (typed FeaturePython)
  n = 0.002
FEATURE [App::DocumentObjectGroupPython] Cl_element003  label="Cl_element : 0.004"  # scripted group (container) (typed FeaturePython)
  n = 0.003
FEATURE [App::DocumentObjectGroupPython] K_element002  label="K_element : 0.003"  # scripted group (container) (typed FeaturePython)
  n = 0.003
FEATURE [App::DocumentObjectGroupPython] G4_BRAIN_ICRP  # scripted group (container) (typed FeaturePython)
  Dunit = g/cm3
  Dvalue = 1.04
  Group = -> [H_element017,C_element018,N_element012,O_element017,Na_element004,P_element004,S_element006,Cl_element003,K_element002]
  conduct = 2
  density = 1
  expand = 3
  formula = G4_BRAIN_ICRP
  name = G4_BRAIN_ICRP
  specific = 4
FEATURE [App::DocumentObjectGroupPython] C_element019  label="C_element : 4"  # scripted group (container) (typed FeaturePython)
  n = 4
  ref = C_element
FEATURE [App::DocumentObjectGroupPython] H_element018  label="H_element : 010"  # scripted group (container) (typed FeaturePython)
  n = 10
  ref = H_element
FEATURE [App::DocumentObjectGroupPython] G4_BUTANE  # scripted group (container) (typed FeaturePython)
  Dunit = g/cm3
  Dvalue = 0.00249343
  Group = -> [C_element019,H_element018]
  conduct = 2
  density = 1
  expand = 3
  formula = G4_BUTANE
  name = G4_BUTANE
  specific = 4
FEATURE [App::DocumentObjectGroupPython] C_element020  label="C_element : 008"  # scripted group (container) (typed FeaturePython)
  n = 4
  ref = C_element
FEATURE [App::DocumentObjectGroupPython] H_element019  label="H_element : 011"  # scripted group (container) (typed FeaturePython)
  n = 10
  ref = H_element
FEATURE [App::DocumentObjectGroupPython] O_element018  label="O_element : 007"  # scripted group (container) (typed FeaturePython)
  n = 1
  ref = O_element
FEATURE [App::DocumentObjectGroupPython] G4_N_BUTYL_ALCOHOL  label="G4_N-BUTYL_ALCOHOL"  # scripted group (container) (typed FeaturePython)
  Dunit = g/cm3
  Dvalue = 0.8098
  Group = -> [C_element020,H_element019,O_element018]
  conduct = 2
  density = 1
  expand = 3
  formula = G4_N-BUTYL_ALCOHOL
  name = G4_N-BUTYL_ALCOHOL
  specific = 4
FEATURE [App::DocumentObjectGroupPython] H_element020  label="H_element : 0.025"  # scripted group (container) (typed FeaturePython)
  n = 0.02468
FEATURE [App::DocumentObjectGroupPython] C_element021  label="C_element : 0.502"  # scripted group (container) (typed FeaturePython)
  n = 0.501611
FEATURE [App::DocumentObjectGroupPython] O_element019  label="O_element : 0.005"  # scripted group (container) (typed FeaturePython)
  n = 0.004527
FEATURE [App::DocumentObjectGroupPython] F_element004  label="F_element : 0.465"  # scripted group (container) (typed FeaturePython)
  n = 0.465209
FEATURE [App::DocumentObjectGroupPython] Si_element001  label="Si_element : 0.004"  # scripted group (container) (typed FeaturePython)
  n = 0.003973
FEATURE [App::DocumentObjectGroupPython] G4_C_552  label="G4_C-552"  # scripted group (container) (typed FeaturePython)
  Dunit = g/cm3
  Dvalue = 1.76
  Group = -> [H_element020,C_element021,O_element019,F_element004,Si_element001]
  conduct = 2
  density = 1
  expand = 3
  formula = G4_C-552
  name = G4_C-552
  specific = 4
FEATURE [App::DocumentObjectGroupPython] Cd_element001  label="Cd_element : 1"  # scripted group (container) (typed FeaturePython)
  n = 1
  ref = Cd_element
FEATURE [App::DocumentObjectGroupPython] Te_element001  label="Te_element : 1"  # scripted group (container) (typed FeaturePython)
  n = 1
  ref = Te_element
FEATURE [App::DocumentObjectGroupPython] G4_CADMIUM_TELLURIDE  # scripted group (container) (typed FeaturePython)
  Dunit = g/cm3
  Dvalue = 6.2
  Group = -> [Cd_element001,Te_element001]
  conduct = 2
  density = 1
  expand = 3
  formula = G4_CADMIUM_TELLURIDE
  name = G4_CADMIUM_TELLURIDE
  specific = 4
FEATURE [App::DocumentObjectGroupPython] Cd_element002  label="Cd_element : 002"  # scripted group (container) (typed FeaturePython)
  n = 1
  ref = Cd_element
FEATURE [App::DocumentObjectGroupPython] W_element001  label="W_element : 1"  # scripted group (container) (typed FeaturePython)
  n = 1
  ref = W_element
FEATURE [App::DocumentObjectGroupPython] O_element020  label="O_element : 008"  # scripted group (container) (typed FeaturePython)
  n = 4
  ref = O_element
FEATURE [App::DocumentObjectGroupPython] G4_CADMIUM_TUNGSTATE  # scripted group (container) (typed FeaturePython)
  Dunit = g/cm3
  Dvalue = 7.9
  Group = -> [Cd_element002,W_element001,O_element020]
  conduct = 2
  density = 1
  expand = 3
  formula = G4_CADMIUM_TUNGSTATE
  name = G4_CADMIUM_TUNGSTATE
  specific = 4
FEATURE [App::DocumentObjectGroupPython] Ca_element005  label="Ca_element : 1"  # scripted group (container) (typed FeaturePython)
  n = 1
  ref = Ca_element
FEATURE [App::DocumentObjectGroupPython] C_element022  label="C_element : 009"  # scripted group (container) (typed FeaturePython)
  n = 1
  ref = C_element
FEATURE [App::DocumentObjectGroupPython] O_element021  label="O_element : 009"  # scripted group (container) (typed FeaturePython)
  n = 3
  ref = O_element
FEATURE [App::DocumentObjectGroupPython] G4_CALCIUM_CARBONATE  # scripted group (container) (typed FeaturePython)
  Dunit = g/cm3
  Dvalue = 2.8
  Group = -> [Ca_element005,C_element022,O_element021]
  conduct = 2
  density = 1
  expand = 3
  formula = G4_CALCIUM_CARBONATE
  name = G4_CALCIUM_CARBONATE
  specific = 4
FEATURE [App::DocumentObjectGroupPython] Ca_element006  label="Ca_element : 002"  # scripted group (container) (typed FeaturePython)
  n = 1
  ref = Ca_element
FEATURE [App::DocumentObjectGroupPython] F_element005  label="F_element : 003"  # scripted group (container) (typed FeaturePython)
  n = 2
  ref = F_element
FEATURE [App::DocumentObjectGroupPython] G4_CALCIUM_FLUORIDE  # scripted group (container) (typed FeaturePython)
  Dunit = g/cm3
  Dvalue = 3.18
  Group = -> [Ca_element006,F_element005]
  conduct = 2
  density = 1
  expand = 3
  formula = G4_CALCIUM_FLUORIDE
  name = G4_CALCIUM_FLUORIDE
  specific = 4
FEATURE [App::DocumentObjectGroupPython] Ca_element007  label="Ca_element : 003"  # scripted group (container) (typed FeaturePython)
  n = 1
  ref = Ca_element
FEATURE [App::DocumentObjectGroupPython] O_element022  label="O_element : 010"  # scripted group (container) (typed FeaturePython)
  n = 1
  ref = O_element
FEATURE [App::DocumentObjectGroupPython] G4_CALCIUM_OXIDE  # scripted group (container) (typed FeaturePython)
  Dunit = g/cm3
  Dvalue = 3.3
  Group = -> [Ca_element007,O_element022]
  conduct = 2
  density = 1
  expand = 3
  formula = G4_CALCIUM_OXIDE
  name = G4_CALCIUM_OXIDE
  specific = 4
FEATURE [App::DocumentObjectGroupPython] Ca_element008  label="Ca_element : 004"  # scripted group (container) (typed FeaturePython)
  n = 1
  ref = Ca_element
FEATURE [App::DocumentObjectGroupPython] S_element007  label="S_element : 002"  # scripted group (container) (typed FeaturePython)
  n = 1
  ref = S_element
FEATURE [App::DocumentObjectGroupPython] O_element023  label="O_element : 011"  # scripted group (container) (typed FeaturePython)
  n = 4
  ref = O_element
FEATURE [App::DocumentObjectGroupPython] G4_CALCIUM_SULFATE  # scripted group (container) (typed FeaturePython)
  Dunit = g/cm3
  Dvalue = 2.96
  Group = -> [Ca_element008,S_element007,O_element023]
  conduct = 2
  density = 1
  expand = 3
  formula = G4_CALCIUM_SULFATE
  name = G4_CALCIUM_SULFATE
  specific = 4
FEATURE [App::DocumentObjectGroupPython] Ca_element009  label="Ca_element : 005"  # scripted group (container) (typed FeaturePython)
  n = 1
  ref = Ca_element
FEATURE [App::DocumentObjectGroupPython] W_element002  label="W_element : 002"  # scripted group (container) (typed FeaturePython)
  n = 1
  ref = W_element
FEATURE [App::DocumentObjectGroupPython] O_element024  label="O_element : 012"  # scripted group (container) (typed FeaturePython)
  n = 4
  ref = O_element
FEATURE [App::DocumentObjectGroupPython] G4_CALCIUM_TUNGSTATE  # scripted group (container) (typed FeaturePython)
  Dunit = g/cm3
  Dvalue = 6.062
  Group = -> [Ca_element009,W_element002,O_element024]
  conduct = 2
  density = 1
  expand = 3
  formula = G4_CALCIUM_TUNGSTATE
  name = G4_CALCIUM_TUNGSTATE
  specific = 4
FEATURE [App::DocumentObjectGroupPython] C_element023  label="C_element : 010"  # scripted group (container) (typed FeaturePython)
  n = 1
  ref = C_element
FEATURE [App::DocumentObjectGroupPython] O_element025  label="O_element : 013"  # scripted group (container) (typed FeaturePython)
  n = 2
  ref = O_element
FEATURE [App::DocumentObjectGroupPython] G4_CARBON_DIOXIDE  # scripted group (container) (typed FeaturePython)
  Dunit = g/cm3
  Dvalue = 0.00184212
  Group = -> [C_element023,O_element025]
  conduct = 2
  density = 1
  expand = 3
  formula = G4_CARBON_DIOXIDE
  name = G4_CARBON_DIOXIDE
  specific = 4
FEATURE [App::DocumentObjectGroupPython] C_element024  label="C_element : 011"  # scripted group (container) (typed FeaturePython)
  n = 1
  ref = C_element
FEATURE [App::DocumentObjectGroupPython] Cl_element004  label="Cl_element : 4"  # scripted group (container) (typed FeaturePython)
  n = 4
  ref = Cl_element
FEATURE [App::DocumentObjectGroupPython] G4_CARBON_TETRACHLORIDE  # scripted group (container) (typed FeaturePython)
  Dunit = g/cm3
  Dvalue = 1.594
  Group = -> [C_element024,Cl_element004]
  conduct = 2
  density = 1
  expand = 3
  formula = G4_CARBON_TETRACHLORIDE
  name = G4_CARBON_TETRACHLORIDE
  specific = 4
FEATURE [App::DocumentObjectGroupPython] C_element025  label="C_element : 012"  # scripted group (container) (typed FeaturePython)
  n = 6
  ref = C_element
FEATURE [App::DocumentObjectGroupPython] H_element021  label="H_element : 012"  # scripted group (container) (typed FeaturePython)
  n = 10
  ref = H_element
FEATURE [App::DocumentObjectGroupPython] O_element026  label="O_element : 5"  # scripted group (container) (typed FeaturePython)
  n = 5
  ref = O_element
FEATURE [App::DocumentObjectGroupPython] G4_CELLULOSE_CELLOPHANE  # scripted group (container) (typed FeaturePython)
  Dunit = g/cm3
  Dvalue = 1.42
  Group = -> [C_element025,H_element021,O_element026]
  conduct = 2
  density = 1
  expand = 3
  formula = G4_CELLULOSE_CELLOPHANE
  name = G4_CELLULOSE_CELLOPHANE
  specific = 4
FEATURE [App::DocumentObjectGroupPython] H_element022  label="H_element : 0.067"  # scripted group (container) (typed FeaturePython)
  n = 0.067125
FEATURE [App::DocumentObjectGroupPython] C_element026  label="C_element : 0.545"  # scripted group (container) (typed FeaturePython)
  n = 0.545403
FEATURE [App::DocumentObjectGroupPython] O_element027  label="O_element : 0.387"  # scripted group (container) (typed FeaturePython)
  n = 0.387472
FEATURE [App::DocumentObjectGroupPython] G4_CELLULOSE_BUTYRATE  # scripted group (container) (typed FeaturePython)
  Dunit = g/cm3
  Dvalue = 1.2
  Group = -> [H_element022,C_element026,O_element027]
  conduct = 2
  density = 1
  expand = 3
  formula = G4_CELLULOSE_BUTYRATE
  name = G4_CELLULOSE_BUTYRATE
  specific = 4
FEATURE [App::DocumentObjectGroupPython] H_element023  label="H_element : 0.029"  # scripted group (container) (typed FeaturePython)
  n = 0.029216
FEATURE [App::DocumentObjectGroupPython] C_element027  label="C_element : 0.271"  # scripted group (container) (typed FeaturePython)
  n = 0.271296
FEATURE [App::DocumentObjectGroupPython] N_element013  label="N_element : 0.121"  # scripted group (container) (typed FeaturePython)
  n = 0.121276
FEATURE [App::DocumentObjectGroupPython] O_element028  label="O_element : 0.578"  # scripted group (container) (typed FeaturePython)
  n = 0.578212
FEATURE [App::DocumentObjectGroupPython] G4_CELLULOSE_NITRATE  # scripted group (container) (typed FeaturePython)
  Dunit = g/cm3
  Dvalue = 1.49
  Group = -> [H_element023,C_element027,N_element013,O_element028]
  conduct = 2
  density = 1
  expand = 3
  formula = G4_CELLULOSE_NITRATE
  name = G4_CELLULOSE_NITRATE
  specific = 4
FEATURE [App::DocumentObjectGroupPython] H_element024  label="H_element : 0.108"  # scripted group (container) (typed FeaturePython)
  n = 0.107596
FEATURE [App::DocumentObjectGroupPython] N_element014  label="N_element : 0.001"  # scripted group (container) (typed FeaturePython)
  n = 0.0008
FEATURE [App::DocumentObjectGroupPython] O_element029  label="O_element : 0.875"  # scripted group (container) (typed FeaturePython)
  n = 0.874976
FEATURE [App::DocumentObjectGroupPython] S_element008  label="S_element : 0.015"  # scripted group (container) (typed FeaturePython)
  n = 0.014627
FEATURE [App::DocumentObjectGroupPython] Ce_element001  label="Ce_element : 0.002"  # scripted group (container) (typed FeaturePython)
  n = 0.002001
FEATURE [App::DocumentObjectGroupPython] G4_CERIC_SULFATE  # scripted group (container) (typed FeaturePython)
  Dunit = g/cm3
  Dvalue = 1.03
  Group = -> [H_element024,N_element014,O_element029,S_element008,Ce_element001]
  conduct = 2
  density = 1
  expand = 3
  formula = G4_CERIC_SULFATE
  name = G4_CERIC_SULFATE
  specific = 4
FEATURE [App::DocumentObjectGroupPython] Cs_element001  label="Cs_element : 1"  # scripted group (container) (typed FeaturePython)
  n = 1
  ref = Cs_element
FEATURE [App::DocumentObjectGroupPython] F_element006  label="F_element : 1"  # scripted group (container) (typed FeaturePython)
  n = 1
  ref = F_element
FEATURE [App::DocumentObjectGroupPython] G4_CESIUM_FLUORIDE  # scripted group (container) (typed FeaturePython)
  Dunit = g/cm3
  Dvalue = 4.115
  Group = -> [Cs_element001,F_element006]
  conduct = 2
  density = 1
  expand = 3
  formula = G4_CESIUM_FLUORIDE
  name = G4_CESIUM_FLUORIDE
  specific = 4
FEATURE [App::DocumentObjectGroupPython] Cs_element002  label="Cs_element : 002"  # scripted group (container) (typed FeaturePython)
  n = 1
  ref = Cs_element
FEATURE [App::DocumentObjectGroupPython] I_element001  label="I_element : 1"  # scripted group (container) (typed FeaturePython)
  n = 1
  ref = I_element
FEATURE [App::DocumentObjectGroupPython] G4_CESIUM_IODIDE  # scripted group (container) (typed FeaturePython)
  Dunit = g/cm3
  Dvalue = 4.51
  Group = -> [Cs_element002,I_element001]
  conduct = 2
  density = 1
  expand = 3
  formula = G4_CESIUM_IODIDE
  name = G4_CESIUM_IODIDE
  specific = 4
FEATURE [App::DocumentObjectGroupPython] C_element028  label="C_element : 013"  # scripted group (container) (typed FeaturePython)
  n = 6
  ref = C_element
FEATURE [App::DocumentObjectGroupPython] H_element025  label="H_element : 013"  # scripted group (container) (typed FeaturePython)
  n = 5
  ref = H_element
FEATURE [App::DocumentObjectGroupPython] Cl_element005  label="Cl_element : 1"  # scripted group (container) (typed FeaturePython)
  n = 1
  ref = Cl_element
FEATURE [App::DocumentObjectGroupPython] G4_CHLOROBENZENE  # scripted group (container) (typed FeaturePython)
  Dunit = g/cm3
  Dvalue = 1.1058
  Group = -> [C_element028,H_element025,Cl_element005]
  conduct = 2
  density = 1
  expand = 3
  formula = G4_CHLOROBENZENE
  name = G4_CHLOROBENZENE
  specific = 4
FEATURE [App::DocumentObjectGroupPython] C_element029  label="C_element : 014"  # scripted group (container) (typed FeaturePython)
  n = 1
  ref = C_element
FEATURE [App::DocumentObjectGroupPython] H_element026  label="H_element : 1"  # scripted group (container) (typed FeaturePython)
  n = 1
  ref = H_element
FEATURE [App::DocumentObjectGroupPython] Cl_element006  label="Cl_element : 3"  # scripted group (container) (typed FeaturePython)
  n = 3
  ref = Cl_element
FEATURE [App::DocumentObjectGroupPython] G4_CHLOROFORM  # scripted group (container) (typed FeaturePython)
  Dunit = g/cm3
  Dvalue = 1.4832
  Group = -> [C_element029,H_element026,Cl_element006]
  conduct = 2
  density = 1
  expand = 3
  formula = G4_CHLOROFORM
  name = G4_CHLOROFORM
  specific = 4
FEATURE [App::DocumentObjectGroupPython] H_element027  label="H_element : 0.010"  # scripted group (container) (typed FeaturePython)
  n = 0.01
FEATURE [App::DocumentObjectGroupPython] C_element030  label="C_element : 0.001"  # scripted group (container) (typed FeaturePython)
  n = 0.001
FEATURE [App::DocumentObjectGroupPython] O_element030  label="O_element : 0.529"  # scripted group (container) (typed FeaturePython)
  n = 0.529107
FEATURE [App::DocumentObjectGroupPython] Na_element005  label="Na_element : 0.016"  # scripted group (container) (typed FeaturePython)
  n = 0.016
FEATURE [App::DocumentObjectGroupPython] Mg_element003  label="Mg_element : 0.004"  # scripted group (container) (typed FeaturePython)
  n = 0.002
FEATURE [App::DocumentObjectGroupPython] Al_element002  label="Al_element : 0.034"  # scripted group (container) (typed FeaturePython)
  n = 0.033872
FEATURE [App::DocumentObjectGroupPython] Si_element002  label="Si_element : 0.337"  # scripted group (container) (typed FeaturePython)
  n = 0.337021
FEATURE [App::DocumentObjectGroupPython] K_element003  label="K_element : 0.013"  # scripted group (container) (typed FeaturePython)
  n = 0.013
FEATURE [App::DocumentObjectGroupPython] Ca_element010  label="Ca_element : 0.044"  # scripted group (container) (typed FeaturePython)
  n = 0.044
FEATURE [App::DocumentObjectGroupPython] Fe_element002  label="Fe_element : 0.014"  # scripted group (container) (typed FeaturePython)
  n = 0.014
FEATURE [App::DocumentObjectGroupPython] G4_CONCRETE  # scripted group (container) (typed FeaturePython)
  Dunit = g/cm3
  Dvalue = 2.3
  Group = -> [H_element027,C_element030,O_element030,Na_element005,Mg_element003,Al_element002,Si_element002,K_element003,Ca_element010,Fe_element002]
  conduct = 2
  density = 1
  expand = 3
  formula = G4_CONCRETE
  name = G4_CONCRETE
  specific = 4
FEATURE [App::DocumentObjectGroupPython] C_element031  label="C_element : 015"  # scripted group (container) (typed FeaturePython)
  n = 6
  ref = C_element
FEATURE [App::DocumentObjectGroupPython] H_element028  label="H_element : 12"  # scripted group (container) (typed FeaturePython)
  n = 12
  ref = H_element
FEATURE [App::DocumentObjectGroupPython] G4_CYCLOHEXANE  # scripted group (container) (typed FeaturePython)
  Dunit = g/cm3
  Dvalue = 0.779
  Group = -> [C_element031,H_element028]
  conduct = 2
  density = 1
  expand = 3
  formula = G4_CYCLOHEXANE
  name = G4_CYCLOHEXANE
  specific = 4
FEATURE [App::DocumentObjectGroupPython] C_element032  label="C_element : 016"  # scripted group (container) (typed FeaturePython)
  n = 6
  ref = C_element
FEATURE [App::DocumentObjectGroupPython] H_element029  label="H_element : 4"  # scripted group (container) (typed FeaturePython)
  n = 4
  ref = H_element
FEATURE [App::DocumentObjectGroupPython] Cl_element007  label="Cl_element : 2"  # scripted group (container) (typed FeaturePython)
  n = 2
  ref = Cl_element
FEATURE [App::DocumentObjectGroupPython] G4_1_2_DICHLOROBENZENE  label="G4_1.2-DICHLOROBENZENE"  # scripted group (container) (typed FeaturePython)
  Dunit = g/cm3
  Dvalue = 1.3048
  Group = -> [C_element032,H_element029,Cl_element007]
  conduct = 2
  density = 1
  expand = 3
  formula = G4_1.2-DICHLOROBENZENE
  name = G4_1.2-DICHLOROBENZENE
  specific = 4
FEATURE [App::DocumentObjectGroupPython] C_element033  label="C_element : 017"  # scripted group (container) (typed FeaturePython)
  n = 4
  ref = C_element
FEATURE [App::DocumentObjectGroupPython] H_element030  label="H_element : 8"  # scripted group (container) (typed FeaturePython)
  n = 8
  ref = H_element
FEATURE [App::DocumentObjectGroupPython] O_element031  label="O_element : 014"  # scripted group (container) (typed FeaturePython)
  n = 1
  ref = O_element
FEATURE [App::DocumentObjectGroupPython] Cl_element008  label="Cl_element : 005"  # scripted group (container) (typed FeaturePython)
  n = 2
  ref = Cl_element
FEATURE [App::DocumentObjectGroupPython] G4_DICHLORODIETHYL_ETHER  # scripted group (container) (typed FeaturePython)
  Dunit = g/cm3
  Dvalue = 1.2199
  Group = -> [C_element033,H_element030,O_element031,Cl_element008]
  conduct = 2
  density = 1
  expand = 3
  formula = G4_DICHLORODIETHYL_ETHER
  name = G4_DICHLORODIETHYL_ETHER
  specific = 4
FEATURE [App::DocumentObjectGroupPython] C_element034  label="C_element : 018"  # scripted group (container) (typed FeaturePython)
  n = 2
  ref = C_element
FEATURE [App::DocumentObjectGroupPython] H_element031  label="H_element : 014"  # scripted group (container) (typed FeaturePython)
  n = 4
  ref = H_element
FEATURE [App::DocumentObjectGroupPython] Cl_element009  label="Cl_element : 006"  # scripted group (container) (typed FeaturePython)
  n = 2
  ref = Cl_element
FEATURE [App::DocumentObjectGroupPython] G4_1_2_DICHLOROETHANE  label="G4_1.2-DICHLOROETHANE"  # scripted group (container) (typed FeaturePython)
  Dunit = g/cm3
  Dvalue = 1.2351
  Group = -> [C_element034,H_element031,Cl_element009]
  conduct = 2
  density = 1
  expand = 3
  formula = G4_1.2-DICHLOROETHANE
  name = G4_1.2-DICHLOROETHANE
  specific = 4
FEATURE [App::DocumentObjectGroupPython] C_element035  label="C_element : 019"  # scripted group (container) (typed FeaturePython)
  n = 4
  ref = C_element
FEATURE [App::DocumentObjectGroupPython] H_element032  label="H_element : 015"  # scripted group (container) (typed FeaturePython)
  n = 10
  ref = H_element
FEATURE [App::DocumentObjectGroupPython] O_element032  label="O_element : 015"  # scripted group (container) (typed FeaturePython)
  n = 1
  ref = O_element
FEATURE [App::DocumentObjectGroupPython] G4_DIETHYL_ETHER  # scripted group (container) (typed FeaturePython)
  Dunit = g/cm3
  Dvalue = 0.71378
  Group = -> [C_element035,H_element032,O_element032]
  conduct = 2
  density = 1
  expand = 3
  formula = G4_DIETHYL_ETHER
  name = G4_DIETHYL_ETHER
  specific = 4
FEATURE [App::DocumentObjectGroupPython] C_element036  label="C_element : 020"  # scripted group (container) (typed FeaturePython)
  n = 3
  ref = C_element
FEATURE [App::DocumentObjectGroupPython] H_element033  label="H_element : 016"  # scripted group (container) (typed FeaturePython)
  n = 7
  ref = H_element
FEATURE [App::DocumentObjectGroupPython] N_element015  label="N_element : 008"  # scripted group (container) (typed FeaturePython)
  n = 1
  ref = N_element
FEATURE [App::DocumentObjectGroupPython] O_element033  label="O_element : 016"  # scripted group (container) (typed FeaturePython)
  n = 1
  ref = O_element
FEATURE [App::DocumentObjectGroupPython] G4_N_N_DIMETHYL_FORMAMIDE  label="G4_N.N-DIMETHYL_FORMAMIDE"  # scripted group (container) (typed FeaturePython)
  Dunit = g/cm3
  Dvalue = 0.9487
  Group = -> [C_element036,H_element033,N_element015,O_element033]
  conduct = 2
  density = 1
  expand = 3
  formula = G4_N.N-DIMETHYL_FORMAMIDE
  name = G4_N.N-DIMETHYL_FORMAMIDE
  specific = 4
FEATURE [App::DocumentObjectGroupPython] C_element037  label="C_element : 021"  # scripted group (container) (typed FeaturePython)
  n = 2
  ref = C_element
FEATURE [App::DocumentObjectGroupPython] H_element034  label="H_element : 017"  # scripted group (container) (typed FeaturePython)
  n = 6
  ref = H_element
FEATURE [App::DocumentObjectGroupPython] O_element034  label="O_element : 017"  # scripted group (container) (typed FeaturePython)
  n = 1
  ref = O_element
FEATURE [App::DocumentObjectGroupPython] S_element009  label="S_element : 003"  # scripted group (container) (typed FeaturePython)
  n = 1
  ref = S_element
FEATURE [App::DocumentObjectGroupPython] G4_DIMETHYL_SULFOXIDE  # scripted group (container) (typed FeaturePython)
  Dunit = g/cm3
  Dvalue = 1.1014
  Group = -> [C_element037,H_element034,O_element034,S_element009]
  conduct = 2
  density = 1
  expand = 3
  formula = G4_DIMETHYL_SULFOXIDE
  name = G4_DIMETHYL_SULFOXIDE
  specific = 4
FEATURE [App::DocumentObjectGroupPython] C_element038  label="C_element : 022"  # scripted group (container) (typed FeaturePython)
  n = 2
  ref = C_element
FEATURE [App::DocumentObjectGroupPython] H_element035  label="H_element : 018"  # scripted group (container) (typed FeaturePython)
  n = 6
  ref = H_element
FEATURE [App::DocumentObjectGroupPython] G4_ETHANE  # scripted group (container) (typed FeaturePython)
  Dunit = g/cm3
  Dvalue = 0.00125324
  Group = -> [C_element038,H_element035]
  conduct = 2
  density = 1
  expand = 3
  formula = G4_ETHANE
  name = G4_ETHANE
  specific = 4
FEATURE [App::DocumentObjectGroupPython] C_element039  label="C_element : 023"  # scripted group (container) (typed FeaturePython)
  n = 2
  ref = C_element
FEATURE [App::DocumentObjectGroupPython] H_element036  label="H_element : 019"  # scripted group (container) (typed FeaturePython)
  n = 6
  ref = H_element
FEATURE [App::DocumentObjectGroupPython] O_element035  label="O_element : 018"  # scripted group (container) (typed FeaturePython)
  n = 1
  ref = O_element
FEATURE [App::DocumentObjectGroupPython] G4_ETHYL_ALCOHOL  # scripted group (container) (typed FeaturePython)
  Dunit = g/cm3
  Dvalue = 0.7893
  Group = -> [C_element039,H_element036,O_element035]
  conduct = 2
  density = 1
  expand = 3
  formula = G4_ETHYL_ALCOHOL
  name = G4_ETHYL_ALCOHOL
  specific = 4
FEATURE [App::DocumentObjectGroupPython] H_element037  label="H_element : 0.090"  # scripted group (container) (typed FeaturePython)
  n = 0.090027
FEATURE [App::DocumentObjectGroupPython] C_element040  label="C_element : 0.585"  # scripted group (container) (typed FeaturePython)
  n = 0.585182
FEATURE [App::DocumentObjectGroupPython] O_element036  label="O_element : 0.325"  # scripted group (container) (typed FeaturePython)
  n = 0.324791
FEATURE [App::DocumentObjectGroupPython] G4_ETHYL_CELLULOSE  # scripted group (container) (typed FeaturePython)
  Dunit = g/cm3
  Dvalue = 1.13
  Group = -> [H_element037,C_element040,O_element036]
  conduct = 2
  density = 1
  expand = 3
  formula = G4_ETHYL_CELLULOSE
  name = G4_ETHYL_CELLULOSE
  specific = 4
FEATURE [App::DocumentObjectGroupPython] C_element041  label="C_element : 024"  # scripted group (container) (typed FeaturePython)
  n = 2
  ref = C_element
FEATURE [App::DocumentObjectGroupPython] H_element038  label="H_element : 020"  # scripted group (container) (typed FeaturePython)
  n = 4
  ref = H_element
FEATURE [App::DocumentObjectGroupPython] G4_ETHYLENE  # scripted group (container) (typed FeaturePython)
  Dunit = g/cm3
  Dvalue = 0.00117497
  Group = -> [C_element041,H_element038]
  conduct = 2
  density = 1
  expand = 3
  formula = G4_ETHYLENE
  name = G4_ETHYLENE
  specific = 4
FEATURE [App::DocumentObjectGroupPython] H_element039  label="H_element : 0.096"  # scripted group (container) (typed FeaturePython)
  n = 0.096
FEATURE [App::DocumentObjectGroupPython] C_element042  label="C_element : 0.195"  # scripted group (container) (typed FeaturePython)
  n = 0.195
FEATURE [App::DocumentObjectGroupPython] N_element016  label="N_element : 0.057"  # scripted group (container) (typed FeaturePython)
  n = 0.057
FEATURE [App::DocumentObjectGroupPython] O_element037  label="O_element : 0.646"  # scripted group (container) (typed FeaturePython)
  n = 0.646
FEATURE [App::DocumentObjectGroupPython] Na_element006  label="Na_element : 0.017"  # scripted group (container) (typed FeaturePython)
  n = 0.001
FEATURE [App::DocumentObjectGroupPython] P_element005  label="P_element : 0.104"  # scripted group (container) (typed FeaturePython)
  n = 0.001
FEATURE [App::DocumentObjectGroupPython] S_element010  label="S_element : 0.016"  # scripted group (container) (typed FeaturePython)
  n = 0.003
FEATURE [App::DocumentObjectGroupPython] Cl_element010  label="Cl_element : 0.005"  # scripted group (container) (typed FeaturePython)
  n = 0.001
FEATURE [App::DocumentObjectGroupPython] G4_EYE_LENS_ICRP  # scripted group (container) (typed FeaturePython)
  Dunit = g/cm3
  Dvalue = 1.07
  Group = -> [H_element039,C_element042,N_element016,O_element037,Na_element006,P_element005,S_element010,Cl_element010]
  conduct = 2
  density = 1
  expand = 3
  formula = G4_EYE_LENS_ICRP
  name = G4_EYE_LENS_ICRP
  specific = 4
FEATURE [App::DocumentObjectGroupPython] Fe_element003  label="Fe_element : 2"  # scripted group (container) (typed FeaturePython)
  n = 2
  ref = Fe_element
FEATURE [App::DocumentObjectGroupPython] O_element038  label="O_element : 019"  # scripted group (container) (typed FeaturePython)
  n = 3
  ref = O_element
FEATURE [App::DocumentObjectGroupPython] G4_FERRIC_OXIDE  # scripted group (container) (typed FeaturePython)
  Dunit = g/cm3
  Dvalue = 5.2
  Group = -> [Fe_element003,O_element038]
  conduct = 2
  density = 1
  expand = 3
  formula = G4_FERRIC_OXIDE
  name = G4_FERRIC_OXIDE
  specific = 4
FEATURE [App::DocumentObjectGroupPython] Fe_element004  label="Fe_element : 1"  # scripted group (container) (typed FeaturePython)
  n = 1
  ref = Fe_element
FEATURE [App::DocumentObjectGroupPython] B_element003  label="B_element : 1"  # scripted group (container) (typed FeaturePython)
  n = 1
  ref = B_element
FEATURE [App::DocumentObjectGroupPython] G4_FERROBORIDE  # scripted group (container) (typed FeaturePython)
  Dunit = g/cm3
  Dvalue = 7.15
  Group = -> [Fe_element004,B_element003]
  conduct = 2
  density = 1
  expand = 3
  formula = G4_FERROBORIDE
  name = G4_FERROBORIDE
  specific = 4
FEATURE [App::DocumentObjectGroupPython] Fe_element005  label="Fe_element : 003"  # scripted group (container) (typed FeaturePython)
  n = 1
  ref = Fe_element
FEATURE [App::DocumentObjectGroupPython] O_element039  label="O_element : 020"  # scripted group (container) (typed FeaturePython)
  n = 1
  ref = O_element
FEATURE [App::DocumentObjectGroupPython] G4_FERROUS_OXIDE  # scripted group (container) (typed FeaturePython)
  Dunit = g/cm3
  Dvalue = 5.7
  Group = -> [Fe_element005,O_element039]
  conduct = 2
  density = 1
  expand = 3
  formula = G4_FERROUS_OXIDE
  name = G4_FERROUS_OXIDE
  specific = 4
FEATURE [App::DocumentObjectGroupPython] H_element040  label="H_element : 0.115"  # scripted group (container) (typed FeaturePython)
  n = 0.108259
FEATURE [App::DocumentObjectGroupPython] N_element017  label="N_element : 0.000"  # scripted group (container) (typed FeaturePython)
  n = 2.7e-05
FEATURE [App::DocumentObjectGroupPython] O_element040  label="O_element : 0.879"  # scripted group (container) (typed FeaturePython)
  n = 0.878636
FEATURE [App::DocumentObjectGroupPython] Na_element007  label="Na_element : 0.000"  # scripted group (container) (typed FeaturePython)
  n = 2.2e-05
FEATURE [App::DocumentObjectGroupPython] S_element011  label="S_element : 0.013"  # scripted group (container) (typed FeaturePython)
  n = 0.012968
FEATURE [App::DocumentObjectGroupPython] Cl_element011  label="Cl_element : 0.000"  # scripted group (container) (typed FeaturePython)
  n = 3.4e-05
FEATURE [App::DocumentObjectGroupPython] Fe_element006  label="Fe_element : 0.000"  # scripted group (container) (typed FeaturePython)
  n = 5.4e-05
FEATURE [App::DocumentObjectGroupPython] G4_FERROUS_SULFATE  # scripted group (container) (typed FeaturePython)
  Dunit = g/cm3
  Dvalue = 1.024
  Group = -> [H_element040,N_element017,O_element040,Na_element007,S_element011,Cl_element011,Fe_element006]
  conduct = 2
  density = 1
  expand = 3
  formula = G4_FERROUS_SULFATE
  name = G4_FERROUS_SULFATE
  specific = 4
FEATURE [App::DocumentObjectGroupPython] C_element043  label="C_element : 0.099"  # scripted group (container) (typed FeaturePython)
  n = 0.099335
FEATURE [App::DocumentObjectGroupPython] F_element007  label="F_element : 0.314"  # scripted group (container) (typed FeaturePython)
  n = 0.314247
FEATURE [App::DocumentObjectGroupPython] Cl_element012  label="Cl_element : 0.586"  # scripted group (container) (typed FeaturePython)
  n = 0.586418
FEATURE [App::DocumentObjectGroupPython] G4_FREON_12  label="G4_FREON-12"  # scripted group (container) (typed FeaturePython)
  Dunit = g/cm3
  Dvalue = 1.12
  Group = -> [C_element043,F_element007,Cl_element012]
  conduct = 2
  density = 1
  expand = 3
  formula = G4_FREON-12
  name = G4_FREON-12
  specific = 4
FEATURE [App::DocumentObjectGroupPython] C_element044  label="C_element : 0.057"  # scripted group (container) (typed FeaturePython)
  n = 0.057245
FEATURE [App::DocumentObjectGroupPython] F_element008  label="F_element : 0.181"  # scripted group (container) (typed FeaturePython)
  n = 0.181096
FEATURE [App::DocumentObjectGroupPython] Br_element001  label="Br_element : 0.762"  # scripted group (container) (typed FeaturePython)
  n = 0.761659
FEATURE [App::DocumentObjectGroupPython] G4_FREON_12B2  label="G4_FREON-12B2"  # scripted group (container) (typed FeaturePython)
  Dunit = g/cm3
  Dvalue = 1.8
  Group = -> [C_element044,F_element008,Br_element001]
  conduct = 2
  density = 1
  expand = 3
  formula = G4_FREON-12B2
  name = G4_FREON-12B2
  specific = 4
FEATURE [App::DocumentObjectGroupPython] C_element045  label="C_element : 0.115"  # scripted group (container) (typed FeaturePython)
  n = 0.114983
FEATURE [App::DocumentObjectGroupPython] F_element009  label="F_element : 0.546"  # scripted group (container) (typed FeaturePython)
  n = 0.545621
FEATURE [App::DocumentObjectGroupPython] Cl_element013  label="Cl_element : 0.339"  # scripted group (container) (typed FeaturePython)
  n = 0.339396
FEATURE [App::DocumentObjectGroupPython] G4_FREON_13  label="G4_FREON-13"  # scripted group (container) (typed FeaturePython)
  Dunit = g/cm3
  Dvalue = 0.95
  Group = -> [C_element045,F_element009,Cl_element013]
  conduct = 2
  density = 1
  expand = 3
  formula = G4_FREON-13
  name = G4_FREON-13
  specific = 4
FEATURE [App::DocumentObjectGroupPython] C_element046  label="C_element : 025"  # scripted group (container) (typed FeaturePython)
  n = 1
  ref = C_element
FEATURE [App::DocumentObjectGroupPython] F_element010  label="F_element : 3"  # scripted group (container) (typed FeaturePython)
  n = 3
  ref = F_element
FEATURE [App::DocumentObjectGroupPython] Br_element002  label="Br_element : 1"  # scripted group (container) (typed FeaturePython)
  n = 1
  ref = Br_element
FEATURE [App::DocumentObjectGroupPython] G4_FREON_13B1  label="G4_FREON-13B1"  # scripted group (container) (typed FeaturePython)
  Dunit = g/cm3
  Dvalue = 1.5
  Group = -> [C_element046,F_element010,Br_element002]
  conduct = 2
  density = 1
  expand = 3
  formula = G4_FREON-13B1
  name = G4_FREON-13B1
  specific = 4
FEATURE [App::DocumentObjectGroupPython] C_element047  label="C_element : 0.061"  # scripted group (container) (typed FeaturePython)
  n = 0.061309
FEATURE [App::DocumentObjectGroupPython] F_element011  label="F_element : 0.291"  # scripted group (container) (typed FeaturePython)
  n = 0.290924
FEATURE [App::DocumentObjectGroupPython] I_element002  label="I_element : 0.648"  # scripted group (container) (typed FeaturePython)
  n = 0.647767
FEATURE [App::DocumentObjectGroupPython] G4_FREON_13I1  label="G4_FREON-13I1"  # scripted group (container) (typed FeaturePython)
  Dunit = g/cm3
  Dvalue = 1.8
  Group = -> [C_element047,F_element011,I_element002]
  conduct = 2
  density = 1
  expand = 3
  formula = G4_FREON-13I1
  name = G4_FREON-13I1
  specific = 4
FEATURE [App::DocumentObjectGroupPython] Gd_element001  label="Gd_element : 2"  # scripted group (container) (typed FeaturePython)
  n = 2
  ref = Gd_element
FEATURE [App::DocumentObjectGroupPython] O_element041  label="O_element : 021"  # scripted group (container) (typed FeaturePython)
  n = 2
  ref = O_element
FEATURE [App::DocumentObjectGroupPython] S_element012  label="S_element : 004"  # scripted group (container) (typed FeaturePython)
  n = 1
  ref = S_element
FEATURE [App::DocumentObjectGroupPython] G4_GADOLINIUM_OXYSULFIDE  # scripted group (container) (typed FeaturePython)
  Dunit = g/cm3
  Dvalue = 7.44
  Group = -> [Gd_element001,O_element041,S_element012]
  conduct = 2
  density = 1
  expand = 3
  formula = G4_GADOLINIUM_OXYSULFIDE
  name = G4_GADOLINIUM_OXYSULFIDE
  specific = 4
FEATURE [App::DocumentObjectGroupPython] Ga_element001  label="Ga_element : 1"  # scripted group (container) (typed FeaturePython)
  n = 1
  ref = Ga_element
FEATURE [App::DocumentObjectGroupPython] As_element001  label="As_element : 1"  # scripted group (container) (typed FeaturePython)
  n = 1
  ref = As_element
FEATURE [App::DocumentObjectGroupPython] G4_GALLIUM_ARSENIDE  # scripted group (container) (typed FeaturePython)
  Dunit = g/cm3
  Dvalue = 5.31
  Group = -> [Ga_element001,As_element001]
  conduct = 2
  density = 1
  expand = 3
  formula = G4_GALLIUM_ARSENIDE
  name = G4_GALLIUM_ARSENIDE
  specific = 4
FEATURE [App::DocumentObjectGroupPython] H_element041  label="H_element : 0.081"  # scripted group (container) (typed FeaturePython)
  n = 0.08118
FEATURE [App::DocumentObjectGroupPython] C_element048  label="C_element : 0.416"  # scripted group (container) (typed FeaturePython)
  n = 0.41606
FEATURE [App::DocumentObjectGroupPython] N_element018  label="N_element : 0.111"  # scripted group (container) (typed FeaturePython)
  n = 0.11124
FEATURE [App::DocumentObjectGroupPython] O_element042  label="O_element : 0.381"  # scripted group (container) (typed FeaturePython)
  n = 0.38064
FEATURE [App::DocumentObjectGroupPython] S_element013  label="S_element : 0.011"  # scripted group (container) (typed FeaturePython)
  n = 0.01088
FEATURE [App::DocumentObjectGroupPython] G4_GEL_PHOTO_EMULSION  # scripted group (container) (typed FeaturePython)
  Dunit = g/cm3
  Dvalue = 1.2914
  Group = -> [H_element041,C_element048,N_element018,O_element042,S_element013]
  conduct = 2
  density = 1
  expand = 3
  formula = G4_GEL_PHOTO_EMULSION
  name = G4_GEL_PHOTO_EMULSION
  specific = 4
FEATURE [App::DocumentObjectGroupPython] B_element004  label="B_element : 0.040"  # scripted group (container) (typed FeaturePython)
  n = 0.0400639
FEATURE [App::DocumentObjectGroupPython] O_element043  label="O_element : 0.540"  # scripted group (container) (typed FeaturePython)
  n = 0.539561
FEATURE [App::DocumentObjectGroupPython] Na_element008  label="Na_element : 0.028"  # scripted group (container) (typed FeaturePython)
  n = 0.0281909
FEATURE [App::DocumentObjectGroupPython] Al_element003  label="Al_element : 0.012"  # scripted group (container) (typed FeaturePython)
  n = 0.011644
FEATURE [App::DocumentObjectGroupPython] Si_element003  label="Si_element : 0.377"  # scripted group (container) (typed FeaturePython)
  n = 0.377219
FEATURE [App::DocumentObjectGroupPython] K_element004  label="K_element : 0.014"  # scripted group (container) (typed FeaturePython)
  n = 0.00332099
FEATURE [App::DocumentObjectGroupPython] G4_Pyrex_Glass  # scripted group (container) (typed FeaturePython)
  Dunit = g/cm3
  Dvalue = 2.23
  Group = -> [B_element004,O_element043,Na_element008,Al_element003,Si_element003,K_element004]
  conduct = 2
  density = 1
  expand = 3
  formula = G4_Pyrex_Glass
  name = G4_Pyrex_Glass
  specific = 4
FEATURE [App::DocumentObjectGroupPython] O_element044  label="O_element : 0.156"  # scripted group (container) (typed FeaturePython)
  n = 0.156453
FEATURE [App::DocumentObjectGroupPython] Si_element004  label="Si_element : 0.081"  # scripted group (container) (typed FeaturePython)
  n = 0.080866
FEATURE [App::DocumentObjectGroupPython] Ti_element001  label="Ti_element : 0.008"  # scripted group (container) (typed FeaturePython)
  n = 0.008092
FEATURE [App::DocumentObjectGroupPython] As_element002  label="As_element : 0.003"  # scripted group (container) (typed FeaturePython)
  n = 0.002651
FEATURE [App::DocumentObjectGroupPython] Pb_element001  label="Pb_element : 0.752"  # scripted group (container) (typed FeaturePython)
  n = 0.751938
FEATURE [App::DocumentObjectGroupPython] G4_GLASS_LEAD  # scripted group (container) (typed FeaturePython)
  Dunit = g/cm3
  Dvalue = 6.22
  Group = -> [O_element044,Si_element004,Ti_element001,As_element002,Pb_element001]
  conduct = 2
  density = 1
  expand = 3
  formula = G4_GLASS_LEAD
  name = G4_GLASS_LEAD
  specific = 4
FEATURE [App::DocumentObjectGroupPython] O_element045  label="O_element : 0.460"  # scripted group (container) (typed FeaturePython)
  n = 0.4598
FEATURE [App::DocumentObjectGroupPython] Na_element009  label="Na_element : 0.096"  # scripted group (container) (typed FeaturePython)
  n = 0.0964411
FEATURE [App::DocumentObjectGroupPython] Si_element005  label="Si_element : 0.378"  # scripted group (container) (typed FeaturePython)
  n = 0.336553
FEATURE [App::DocumentObjectGroupPython] Ca_element011  label="Ca_element : 0.107"  # scripted group (container) (typed FeaturePython)
  n = 0.107205
FEATURE [App::DocumentObjectGroupPython] G4_GLASS_PLATE  # scripted group (container) (typed FeaturePython)
  Dunit = g/cm3
  Dvalue = 2.4
  Group = -> [O_element045,Na_element009,Si_element005,Ca_element011]
  conduct = 2
  density = 1
  expand = 3
  formula = G4_GLASS_PLATE
  name = G4_GLASS_PLATE
  specific = 4
FEATURE [App::DocumentObjectGroupPython] C_element049  label="C_element : 026"  # scripted group (container) (typed FeaturePython)
  n = 5
  ref = C_element
FEATURE [App::DocumentObjectGroupPython] H_element042  label="H_element : 021"  # scripted group (container) (typed FeaturePython)
  n = 10
  ref = H_element
FEATURE [App::DocumentObjectGroupPython] N_element019  label="N_element : 2"  # scripted group (container) (typed FeaturePython)
  n = 2
  ref = N_element
FEATURE [App::DocumentObjectGroupPython] O_element046  label="O_element : 022"  # scripted group (container) (typed FeaturePython)
  n = 3
  ref = O_element
FEATURE [App::DocumentObjectGroupPython] G4_GLUTAMINE  # scripted group (container) (typed FeaturePython)
  Dunit = g/cm3
  Dvalue = 1.46
  Group = -> [C_element049,H_element042,N_element019,O_element046]
  conduct = 2
  density = 1
  expand = 3
  formula = G4_GLUTAMINE
  name = G4_GLUTAMINE
  specific = 4
FEATURE [App::DocumentObjectGroupPython] C_element050  label="C_element : 027"  # scripted group (container) (typed FeaturePython)
  n = 3
  ref = C_element
FEATURE [App::DocumentObjectGroupPython] H_element043  label="H_element : 022"  # scripted group (container) (typed FeaturePython)
  n = 8
  ref = H_element
FEATURE [App::DocumentObjectGroupPython] O_element047  label="O_element : 023"  # scripted group (container) (typed FeaturePython)
  n = 3
  ref = O_element
FEATURE [App::DocumentObjectGroupPython] G4_GLYCEROL  # scripted group (container) (typed FeaturePython)
  Dunit = g/cm3
  Dvalue = 1.2613
  Group = -> [C_element050,H_element043,O_element047]
  conduct = 2
  density = 1
  expand = 3
  formula = G4_GLYCEROL
  name = G4_GLYCEROL
  specific = 4
FEATURE [App::DocumentObjectGroupPython] C_element051  label="C_element : 028"  # scripted group (container) (typed FeaturePython)
  n = 5
  ref = C_element
FEATURE [App::DocumentObjectGroupPython] H_element044  label="H_element : 023"  # scripted group (container) (typed FeaturePython)
  n = 5
  ref = H_element
FEATURE [App::DocumentObjectGroupPython] N_element020  label="N_element : 009"  # scripted group (container) (typed FeaturePython)
  n = 5
  ref = N_element
FEATURE [App::DocumentObjectGroupPython] O_element048  label="O_element : 024"  # scripted group (container) (typed FeaturePython)
  n = 1
  ref = O_element
FEATURE [App::DocumentObjectGroupPython] G4_GUANINE  # scripted group (container) (typed FeaturePython)
  Dunit = g/cm3
  Dvalue = 2.2
  Group = -> [C_element051,H_element044,N_element020,O_element048]
  conduct = 2
  density = 1
  expand = 3
  formula = G4_GUANINE
  name = G4_GUANINE
  specific = 4
FEATURE [App::DocumentObjectGroupPython] Ca_element012  label="Ca_element : 006"  # scripted group (container) (typed FeaturePython)
  n = 1
  ref = Ca_element
FEATURE [App::DocumentObjectGroupPython] S_element014  label="S_element : 005"  # scripted group (container) (typed FeaturePython)
  n = 1
  ref = S_element
FEATURE [App::DocumentObjectGroupPython] O_element049  label="O_element : 6"  # scripted group (container) (typed FeaturePython)
  n = 6
  ref = O_element
FEATURE [App::DocumentObjectGroupPython] H_element045  label="H_element : 024"  # scripted group (container) (typed FeaturePython)
  n = 4
  ref = H_element
FEATURE [App::DocumentObjectGroupPython] G4_GYPSUM  # scripted group (container) (typed FeaturePython)
  Dunit = g/cm3
  Dvalue = 2.32
  Group = -> [Ca_element012,S_element014,O_element049,H_element045]
  conduct = 2
  density = 1
  expand = 3
  formula = G4_GYPSUM
  name = G4_GYPSUM
  specific = 4
FEATURE [App::DocumentObjectGroupPython] C_element052  label="C_element : 7"  # scripted group (container) (typed FeaturePython)
  n = 7
  ref = C_element
FEATURE [App::DocumentObjectGroupPython] H_element046  label="H_element : 16"  # scripted group (container) (typed FeaturePython)
  n = 16
  ref = H_element
FEATURE [App::DocumentObjectGroupPython] G4_N_HEPTANE  label="G4_N-HEPTANE"  # scripted group (container) (typed FeaturePython)
  Dunit = g/cm3
  Dvalue = 0.68376
  Group = -> [C_element052,H_element046]
  conduct = 2
  density = 1
  expand = 3
  formula = G4_N-HEPTANE
  name = G4_N-HEPTANE
  specific = 4
FEATURE [App::DocumentObjectGroupPython] C_element053  label="C_element : 029"  # scripted group (container) (typed FeaturePython)
  n = 6
  ref = C_element
FEATURE [App::DocumentObjectGroupPython] H_element047  label="H_element : 14"  # scripted group (container) (typed FeaturePython)
  n = 14
  ref = H_element
FEATURE [App::DocumentObjectGroupPython] G4_N_HEXANE  label="G4_N-HEXANE"  # scripted group (container) (typed FeaturePython)
  Dunit = g/cm3
  Dvalue = 0.6603
  Group = -> [C_element053,H_element047]
  conduct = 2
  density = 1
  expand = 3
  formula = G4_N-HEXANE
  name = G4_N-HEXANE
  specific = 4
FEATURE [App::DocumentObjectGroupPython] C_element054  label="C_element : 22"  # scripted group (container) (typed FeaturePython)
  n = 22
  ref = C_element
FEATURE [App::DocumentObjectGroupPython] H_element048  label="H_element : 025"  # scripted group (container) (typed FeaturePython)
  n = 10
  ref = H_element
FEATURE [App::DocumentObjectGroupPython] N_element021  label="N_element : 010"  # scripted group (container) (typed FeaturePython)
  n = 2
  ref = N_element
FEATURE [App::DocumentObjectGroupPython] O_element050  label="O_element : 025"  # scripted group (container) (typed FeaturePython)
  n = 5
  ref = O_element
FEATURE [App::DocumentObjectGroupPython] G4_KAPTON  # scripted group (container) (typed FeaturePython)
  Dunit = g/cm3
  Dvalue = 1.42
  Group = -> [C_element054,H_element048,N_element021,O_element050]
  conduct = 2
  density = 1
  expand = 3
  formula = G4_KAPTON
  name = G4_KAPTON
  specific = 4
FEATURE [App::DocumentObjectGroupPython] La_element001  label="La_element : 1"  # scripted group (container) (typed FeaturePython)
  n = 1
  ref = La_element
FEATURE [App::DocumentObjectGroupPython] Br_element003  label="Br_element : 002"  # scripted group (container) (typed FeaturePython)
  n = 1
  ref = Br_element
FEATURE [App::DocumentObjectGroupPython] O_element051  label="O_element : 026"  # scripted group (container) (typed FeaturePython)
  n = 1
  ref = O_element
FEATURE [App::DocumentObjectGroupPython] G4_LANTHANUM_OXYBROMIDE  # scripted group (container) (typed FeaturePython)
  Dunit = g/cm3
  Dvalue = 6.28
  Group = -> [La_element001,Br_element003,O_element051]
  conduct = 2
  density = 1
  expand = 3
  formula = G4_LANTHANUM_OXYBROMIDE
  name = G4_LANTHANUM_OXYBROMIDE
  specific = 4
FEATURE [App::DocumentObjectGroupPython] La_element002  label="La_element : 2"  # scripted group (container) (typed FeaturePython)
  n = 2
  ref = La_element
FEATURE [App::DocumentObjectGroupPython] O_element052  label="O_element : 027"  # scripted group (container) (typed FeaturePython)
  n = 2
  ref = O_element
FEATURE [App::DocumentObjectGroupPython] S_element015  label="S_element : 006"  # scripted group (container) (typed FeaturePython)
  n = 1
  ref = S_element
FEATURE [App::DocumentObjectGroupPython] G4_LANTHANUM_OXYSULFIDE  # scripted group (container) (typed FeaturePython)
  Dunit = g/cm3
  Dvalue = 5.86
  Group = -> [La_element002,O_element052,S_element015]
  conduct = 2
  density = 1
  expand = 3
  formula = G4_LANTHANUM_OXYSULFIDE
  name = G4_LANTHANUM_OXYSULFIDE
  specific = 4
FEATURE [App::DocumentObjectGroupPython] O_element053  label="O_element : 0.072"  # scripted group (container) (typed FeaturePython)
  n = 0.071682
FEATURE [App::DocumentObjectGroupPython] Pb_element002  label="Pb_element : 0.928"  # scripted group (container) (typed FeaturePython)
  n = 0.928318
FEATURE [App::DocumentObjectGroupPython] G4_LEAD_OXIDE  # scripted group (container) (typed FeaturePython)
  Dunit = g/cm3
  Dvalue = 9.53
  Group = -> [O_element053,Pb_element002]
  conduct = 2
  density = 1
  expand = 3
  formula = G4_LEAD_OXIDE
  name = G4_LEAD_OXIDE
  specific = 4
FEATURE [App::DocumentObjectGroupPython] Li_element001  label="Li_element : 1"  # scripted group (container) (typed FeaturePython)
  n = 1
  ref = Li_element
FEATURE [App::DocumentObjectGroupPython] N_element022  label="N_element : 011"  # scripted group (container) (typed FeaturePython)
  n = 1
  ref = N_element
FEATURE [App::DocumentObjectGroupPython] H_element049  label="H_element : 026"  # scripted group (container) (typed FeaturePython)
  n = 2
  ref = H_element
FEATURE [App::DocumentObjectGroupPython] G4_LITHIUM_AMIDE  # scripted group (container) (typed FeaturePython)
  Dunit = g/cm3
  Dvalue = 1.178
  Group = -> [Li_element001,N_element022,H_element049]
  conduct = 2
  density = 1
  expand = 3
  formula = G4_LITHIUM_AMIDE
  name = G4_LITHIUM_AMIDE
  specific = 4
FEATURE [App::DocumentObjectGroupPython] Li_element002  label="Li_element : 2"  # scripted group (container) (typed FeaturePython)
  n = 2
  ref = Li_element
FEATURE [App::DocumentObjectGroupPython] C_element055  label="C_element : 030"  # scripted group (container) (typed FeaturePython)
  n = 1
  ref = C_element
FEATURE [App::DocumentObjectGroupPython] O_element054  label="O_element : 028"  # scripted group (container) (typed FeaturePython)
  n = 3
  ref = O_element
FEATURE [App::DocumentObjectGroupPython] G4_LITHIUM_CARBONATE  # scripted group (container) (typed FeaturePython)
  Dunit = g/cm3
  Dvalue = 2.11
  Group = -> [Li_element002,C_element055,O_element054]
  conduct = 2
  density = 1
  expand = 3
  formula = G4_LITHIUM_CARBONATE
  name = G4_LITHIUM_CARBONATE
  specific = 4
FEATURE [App::DocumentObjectGroupPython] Li_element003  label="Li_element : 003"  # scripted group (container) (typed FeaturePython)
  n = 1
  ref = Li_element
FEATURE [App::DocumentObjectGroupPython] F_element012  label="F_element : 004"  # scripted group (container) (typed FeaturePython)
  n = 1
  ref = F_element
FEATURE [App::DocumentObjectGroupPython] G4_LITHIUM_FLUORIDE  # scripted group (container) (typed FeaturePython)
  Dunit = g/cm3
  Dvalue = 2.635
  Group = -> [Li_element003,F_element012]
  conduct = 2
  density = 1
  expand = 3
  formula = G4_LITHIUM_FLUORIDE
  name = G4_LITHIUM_FLUORIDE
  specific = 4
FEATURE [App::DocumentObjectGroupPython] Li_element004  label="Li_element : 004"  # scripted group (container) (typed FeaturePython)
  n = 1
  ref = Li_element
FEATURE [App::DocumentObjectGroupPython] H_element050  label="H_element : 027"  # scripted group (container) (typed FeaturePython)
  n = 1
  ref = H_element
FEATURE [App::DocumentObjectGroupPython] G4_LITHIUM_HYDRIDE  # scripted group (container) (typed FeaturePython)
  Dunit = g/cm3
  Dvalue = 0.82
  Group = -> [Li_element004,H_element050]
  conduct = 2
  density = 1
  expand = 3
  formula = G4_LITHIUM_HYDRIDE
  name = G4_LITHIUM_HYDRIDE
  specific = 4
FEATURE [App::DocumentObjectGroupPython] Li_element005  label="Li_element : 005"  # scripted group (container) (typed FeaturePython)
  n = 1
  ref = Li_element
FEATURE [App::DocumentObjectGroupPython] I_element003  label="I_element : 002"  # scripted group (container) (typed FeaturePython)
  n = 1
  ref = I_element
FEATURE [App::DocumentObjectGroupPython] G4_LITHIUM_IODIDE  # scripted group (container) (typed FeaturePython)
  Dunit = g/cm3
  Dvalue = 3.494
  Group = -> [Li_element005,I_element003]
  conduct = 2
  density = 1
  expand = 3
  formula = G4_LITHIUM_IODIDE
  name = G4_LITHIUM_IODIDE
  specific = 4
FEATURE [App::DocumentObjectGroupPython] Li_element006  label="Li_element : 006"  # scripted group (container) (typed FeaturePython)
  n = 2
  ref = Li_element
FEATURE [App::DocumentObjectGroupPython] O_element055  label="O_element : 029"  # scripted group (container) (typed FeaturePython)
  n = 1
  ref = O_element
FEATURE [App::DocumentObjectGroupPython] G4_LITHIUM_OXIDE  # scripted group (container) (typed FeaturePython)
  Dunit = g/cm3
  Dvalue = 2.013
  Group = -> [Li_element006,O_element055]
  conduct = 2
  density = 1
  expand = 3
  formula = G4_LITHIUM_OXIDE
  name = G4_LITHIUM_OXIDE
  specific = 4
FEATURE [App::DocumentObjectGroupPython] Li_element007  label="Li_element : 007"  # scripted group (container) (typed FeaturePython)
  n = 2
  ref = Li_element
FEATURE [App::DocumentObjectGroupPython] B_element005  label="B_element : 005"  # scripted group (container) (typed FeaturePython)
  n = 4
  ref = B_element
FEATURE [App::DocumentObjectGroupPython] O_element056  label="O_element : 7"  # scripted group (container) (typed FeaturePython)
  n = 7
  ref = O_element
FEATURE [App::DocumentObjectGroupPython] G4_LITHIUM_TETRABORATE  # scripted group (container) (typed FeaturePython)
  Dunit = g/cm3
  Dvalue = 2.44
  Group = -> [Li_element007,B_element005,O_element056]
  conduct = 2
  density = 1
  expand = 3
  formula = G4_LITHIUM_TETRABORATE
  name = G4_LITHIUM_TETRABORATE
  specific = 4
FEATURE [App::DocumentObjectGroupPython] H_element051  label="H_element : 0.105"  # scripted group (container) (typed FeaturePython)
  n = 0.105
FEATURE [App::DocumentObjectGroupPython] C_element056  label="C_element : 0.083"  # scripted group (container) (typed FeaturePython)
  n = 0.083
FEATURE [App::DocumentObjectGroupPython] N_element023  label="N_element : 0.023"  # scripted group (container) (typed FeaturePython)
  n = 0.023
FEATURE [App::DocumentObjectGroupPython] O_element057  label="O_element : 0.779"  # scripted group (container) (typed FeaturePython)
  n = 0.779
FEATURE [App::DocumentObjectGroupPython] Na_element010  label="Na_element : 0.097"  # scripted group (container) (typed FeaturePython)
  n = 0.002
FEATURE [App::DocumentObjectGroupPython] P_element006  label="P_element : 0.105"  # scripted group (container) (typed FeaturePython)
  n = 0.001
FEATURE [App::DocumentObjectGroupPython] S_element016  label="S_element : 0.017"  # scripted group (container) (typed FeaturePython)
  n = 0.002
FEATURE [App::DocumentObjectGroupPython] Cl_element014  label="Cl_element : 0.587"  # scripted group (container) (typed FeaturePython)
  n = 0.003
FEATURE [App::DocumentObjectGroupPython] K_element005  label="K_element : 0.015"  # scripted group (container) (typed FeaturePython)
  n = 0.002
FEATURE [App::DocumentObjectGroupPython] G4_LUNG_ICRP  # scripted group (container) (typed FeaturePython)
  Dunit = g/cm3
  Dvalue = 1.04
  Group = -> [H_element051,C_element056,N_element023,O_element057,Na_element010,P_element006,S_element016,Cl_element014,K_element005]
  conduct = 2
  density = 1
  expand = 3
  formula = G4_LUNG_ICRP
  name = G4_LUNG_ICRP
  specific = 4
FEATURE [App::DocumentObjectGroupPython] H_element052  label="H_element : 0.116"  # scripted group (container) (typed FeaturePython)
  n = 0.114318
FEATURE [App::DocumentObjectGroupPython] C_element057  label="C_element : 0.656"  # scripted group (container) (typed FeaturePython)
  n = 0.655824
FEATURE [App::DocumentObjectGroupPython] O_element058  label="O_element : 0.092"  # scripted group (container) (typed FeaturePython)
  n = 0.0921831
FEATURE [App::DocumentObjectGroupPython] Mg_element004  label="Mg_element : 0.135"  # scripted group (container) (typed FeaturePython)
  n = 0.134792
FEATURE [App::DocumentObjectGroupPython] Ca_element013  label="Ca_element : 0.003"  # scripted group (container) (typed FeaturePython)
  n = 0.002883
FEATURE [App::DocumentObjectGroupPython] G4_M3_WAX  # scripted group (container) (typed FeaturePython)
  Dunit = g/cm3
  Dvalue = 1.05
  Group = -> [H_element052,C_element057,O_element058,Mg_element004,Ca_element013]
  conduct = 2
  density = 1
  expand = 3
  formula = G4_M3_WAX
  name = G4_M3_WAX
  specific = 4
FEATURE [App::DocumentObjectGroupPython] Mg_element005  label="Mg_element : 1"  # scripted group (container) (typed FeaturePython)
  n = 1
  ref = Mg_element
FEATURE [App::DocumentObjectGroupPython] C_element058  label="C_element : 031"  # scripted group (container) (typed FeaturePython)
  n = 1
  ref = C_element
FEATURE [App::DocumentObjectGroupPython] O_element059  label="O_element : 030"  # scripted group (container) (typed FeaturePython)
  n = 3
  ref = O_element
FEATURE [App::DocumentObjectGroupPython] G4_MAGNESIUM_CARBONATE  # scripted group (container) (typed FeaturePython)
  Dunit = g/cm3
  Dvalue = 2.958
  Group = -> [Mg_element005,C_element058,O_element059]
  conduct = 2
  density = 1
  expand = 3
  formula = G4_MAGNESIUM_CARBONATE
  name = G4_MAGNESIUM_CARBONATE
  specific = 4
FEATURE [App::DocumentObjectGroupPython] Mg_element006  label="Mg_element : 002"  # scripted group (container) (typed FeaturePython)
  n = 1
  ref = Mg_element
FEATURE [App::DocumentObjectGroupPython] F_element013  label="F_element : 005"  # scripted group (container) (typed FeaturePython)
  n = 2
  ref = F_element
FEATURE [App::DocumentObjectGroupPython] G4_MAGNESIUM_FLUORIDE  # scripted group (container) (typed FeaturePython)
  Dunit = g/cm3
  Dvalue = 3
  Group = -> [Mg_element006,F_element013]
  conduct = 2
  density = 1
  expand = 3
  formula = G4_MAGNESIUM_FLUORIDE
  name = G4_MAGNESIUM_FLUORIDE
  specific = 4
FEATURE [App::DocumentObjectGroupPython] Mg_element007  label="Mg_element : 003"  # scripted group (container) (typed FeaturePython)
  n = 1
  ref = Mg_element
FEATURE [App::DocumentObjectGroupPython] O_element060  label="O_element : 031"  # scripted group (container) (typed FeaturePython)
  n = 1
  ref = O_element
FEATURE [App::DocumentObjectGroupPython] G4_MAGNESIUM_OXIDE  # scripted group (container) (typed FeaturePython)
  Dunit = g/cm3
  Dvalue = 3.58
  Group = -> [Mg_element007,O_element060]
  conduct = 2
  density = 1
  expand = 3
  formula = G4_MAGNESIUM_OXIDE
  name = G4_MAGNESIUM_OXIDE
  specific = 4
FEATURE [App::DocumentObjectGroupPython] Mg_element008  label="Mg_element : 004"  # scripted group (container) (typed FeaturePython)
  n = 1
  ref = Mg_element
FEATURE [App::DocumentObjectGroupPython] B_element006  label="B_element : 006"  # scripted group (container) (typed FeaturePython)
  n = 4
  ref = B_element
FEATURE [App::DocumentObjectGroupPython] O_element061  label="O_element : 032"  # scripted group (container) (typed FeaturePython)
  n = 7
  ref = O_element
FEATURE [App::DocumentObjectGroupPython] G4_MAGNESIUM_TETRABORATE  # scripted group (container) (typed FeaturePython)
  Dunit = g/cm3
  Dvalue = 2.53
  Group = -> [Mg_element008,B_element006,O_element061]
  conduct = 2
  density = 1
  expand = 3
  formula = G4_MAGNESIUM_TETRABORATE
  name = G4_MAGNESIUM_TETRABORATE
  specific = 4
FEATURE [App::DocumentObjectGroupPython] Hg_element001  label="Hg_element : 1"  # scripted group (container) (typed FeaturePython)
  n = 1
  ref = Hg_element
FEATURE [App::DocumentObjectGroupPython] I_element004  label="I_element : 2"  # scripted group (container) (typed FeaturePython)
  n = 2
  ref = I_element
FEATURE [App::DocumentObjectGroupPython] G4_MERCURIC_IODIDE  # scripted group (container) (typed FeaturePython)
  Dunit = g/cm3
  Dvalue = 6.36
  Group = -> [Hg_element001,I_element004]
  conduct = 2
  density = 1
  expand = 3
  formula = G4_MERCURIC_IODIDE
  name = G4_MERCURIC_IODIDE
  specific = 4
FEATURE [App::DocumentObjectGroupPython] C_element059  label="C_element : 032"  # scripted group (container) (typed FeaturePython)
  n = 1
  ref = C_element
FEATURE [App::DocumentObjectGroupPython] H_element053  label="H_element : 028"  # scripted group (container) (typed FeaturePython)
  n = 4
  ref = H_element
FEATURE [App::DocumentObjectGroupPython] G4_METHANE  # scripted group (container) (typed FeaturePython)
  Dunit = g/cm3
  Dvalue = 0.000667151
  Group = -> [C_element059,H_element053]
  conduct = 2
  density = 1
  expand = 3
  formula = G4_METHANE
  name = G4_METHANE
  specific = 4
FEATURE [App::DocumentObjectGroupPython] C_element060  label="C_element : 033"  # scripted group (container) (typed FeaturePython)
  n = 1
  ref = C_element
FEATURE [App::DocumentObjectGroupPython] H_element054  label="H_element : 029"  # scripted group (container) (typed FeaturePython)
  n = 4
  ref = H_element
FEATURE [App::DocumentObjectGroupPython] O_element062  label="O_element : 033"  # scripted group (container) (typed FeaturePython)
  n = 1
  ref = O_element
FEATURE [App::DocumentObjectGroupPython] G4_METHANOL  # scripted group (container) (typed FeaturePython)
  Dunit = g/cm3
  Dvalue = 0.7914
  Group = -> [C_element060,H_element054,O_element062]
  conduct = 2
  density = 1
  expand = 3
  formula = G4_METHANOL
  name = G4_METHANOL
  specific = 4
FEATURE [App::DocumentObjectGroupPython] H_element055  label="H_element : 0.134"  # scripted group (container) (typed FeaturePython)
  n = 0.13404
FEATURE [App::DocumentObjectGroupPython] C_element061  label="C_element : 0.778"  # scripted group (container) (typed FeaturePython)
  n = 0.77796
FEATURE [App::DocumentObjectGroupPython] O_element063  label="O_element : 0.035"  # scripted group (container) (typed FeaturePython)
  n = 0.03502
FEATURE [App::DocumentObjectGroupPython] Mg_element009  label="Mg_element : 0.039"  # scripted group (container) (typed FeaturePython)
  n = 0.038594
FEATURE [App::DocumentObjectGroupPython] Ti_element002  label="Ti_element : 0.014"  # scripted group (container) (typed FeaturePython)
  n = 0.014386
FEATURE [App::DocumentObjectGroupPython] G4_MIX_D_WAX  # scripted group (container) (typed FeaturePython)
  Dunit = g/cm3
  Dvalue = 0.99
  Group = -> [H_element055,C_element061,O_element063,Mg_element009,Ti_element002]
  conduct = 2
  density = 1
  expand = 3
  formula = G4_MIX_D_WAX
  name = G4_MIX_D_WAX
  specific = 4
FEATURE [App::DocumentObjectGroupPython] H_element056  label="H_element : 0.135"  # scripted group (container) (typed FeaturePython)
  n = 0.081192
FEATURE [App::DocumentObjectGroupPython] C_element062  label="C_element : 0.583"  # scripted group (container) (typed FeaturePython)
  n = 0.583442
FEATURE [App::DocumentObjectGroupPython] N_element024  label="N_element : 0.018"  # scripted group (container) (typed FeaturePython)
  n = 0.017798
FEATURE [App::DocumentObjectGroupPython] O_element064  label="O_element : 0.186"  # scripted group (container) (typed FeaturePython)
  n = 0.186381
FEATURE [App::DocumentObjectGroupPython] Mg_element010  label="Mg_element : 0.130"  # scripted group (container) (typed FeaturePython)
  n = 0.130287
FEATURE [App::DocumentObjectGroupPython] Cl_element015  label="Cl_element : 0.588"  # scripted group (container) (typed FeaturePython)
  n = 0.0009
FEATURE [App::DocumentObjectGroupPython] G4_MS20_TISSUE  # scripted group (container) (typed FeaturePython)
  Dunit = g/cm3
  Dvalue = 1
  Group = -> [H_element056,C_element062,N_element024,O_element064,Mg_element010,Cl_element015]
  conduct = 2
  density = 1
  expand = 3
  formula = G4_MS20_TISSUE
  name = G4_MS20_TISSUE
  specific = 4
FEATURE [App::DocumentObjectGroupPython] H_element057  label="H_element : 0.136"  # scripted group (container) (typed FeaturePython)
  n = 0.102
FEATURE [App::DocumentObjectGroupPython] C_element063  label="C_element : 0.143"  # scripted group (container) (typed FeaturePython)
  n = 0.143
FEATURE [App::DocumentObjectGroupPython] N_element025  label="N_element : 0.034"  # scripted group (container) (typed FeaturePython)
  n = 0.034
FEATURE [App::DocumentObjectGroupPython] O_element065  label="O_element : 0.710"  # scripted group (container) (typed FeaturePython)
  n = 0.71
FEATURE [App::DocumentObjectGroupPython] Na_element011  label="Na_element : 0.098"  # scripted group (container) (typed FeaturePython)
  n = 0.001
FEATURE [App::DocumentObjectGroupPython] P_element007  label="P_element : 0.002"  # scripted group (container) (typed FeaturePython)
  n = 0.002
FEATURE [App::DocumentObjectGroupPython] S_element017  label="S_element : 0.018"  # scripted group (container) (typed FeaturePython)
  n = 0.003
FEATURE [App::DocumentObjectGroupPython] Cl_element016  label="Cl_element : 0.589"  # scripted group (container) (typed FeaturePython)
  n = 0.001
FEATURE [App::DocumentObjectGroupPython] K_element006  label="K_element : 0.004"  # scripted group (container) (typed FeaturePython)
  n = 0.004
FEATURE [App::DocumentObjectGroupPython] G4_MUSCLE_SKELETAL_ICRP  # scripted group (container) (typed FeaturePython)
  Dunit = g/cm3
  Dvalue = 1.05
  Group = -> [H_element057,C_element063,N_element025,O_element065,Na_element011,P_element007,S_element017,Cl_element016,K_element006]
  conduct = 2
  density = 1
  expand = 3
  formula = G4_MUSCLE_SKELETAL_ICRP
  name = G4_MUSCLE_SKELETAL_ICRP
  specific = 4
FEATURE [App::DocumentObjectGroupPython] H_element058  label="H_element : 0.137"  # scripted group (container) (typed FeaturePython)
  n = 0.102102
FEATURE [App::DocumentObjectGroupPython] C_element064  label="C_element : 0.123"  # scripted group (container) (typed FeaturePython)
  n = 0.123123
FEATURE [App::DocumentObjectGroupPython] N_element026  label="N_element : 0.756"  # scripted group (container) (typed FeaturePython)
  n = 0.035035
FEATURE [App::DocumentObjectGroupPython] O_element066  label="O_element : 0.730"  # scripted group (container) (typed FeaturePython)
  n = 0.72973
FEATURE [App::DocumentObjectGroupPython] Na_element012  label="Na_element : 0.099"  # scripted group (container) (typed FeaturePython)
  n = 0.001001
FEATURE [App::DocumentObjectGroupPython] P_element008  label="P_element : 0.106"  # scripted group (container) (typed FeaturePython)
  n = 0.002002
FEATURE [App::DocumentObjectGroupPython] S_element018  label="S_element : 0.019"  # scripted group (container) (typed FeaturePython)
  n = 0.004004
FEATURE [App::DocumentObjectGroupPython] K_element007  label="K_element : 0.016"  # scripted group (container) (typed FeaturePython)
  n = 0.003003
FEATURE [App::DocumentObjectGroupPython] G4_MUSCLE_STRIATED_ICRU  # scripted group (container) (typed FeaturePython)
  Dunit = g/cm3
  Dvalue = 1.04
  Group = -> [H_element058,C_element064,N_element026,O_element066,Na_element012,P_element008,S_element018,K_element007]
  conduct = 2
  density = 1
  expand = 3
  formula = G4_MUSCLE_STRIATED_ICRU
  name = G4_MUSCLE_STRIATED_ICRU
  specific = 4
FEATURE [App::DocumentObjectGroupPython] H_element059  label="H_element : 0.098"  # scripted group (container) (typed FeaturePython)
  n = 0.0982341
FEATURE [App::DocumentObjectGroupPython] C_element065  label="C_element : 0.156"  # scripted group (container) (typed FeaturePython)
  n = 0.156214
FEATURE [App::DocumentObjectGroupPython] N_element027  label="N_element : 0.757"  # scripted group (container) (typed FeaturePython)
  n = 0.035451
FEATURE [App::DocumentObjectGroupPython] O_element067  label="O_element : 0.880"  # scripted group (container) (typed FeaturePython)
  n = 0.710101
FEATURE [App::DocumentObjectGroupPython] G4_MUSCLE_WITH_SUCROSE  # scripted group (container) (typed FeaturePython)
  Dunit = g/cm3
  Dvalue = 1.11
  Group = -> [H_element059,C_element065,N_element027,O_element067]
  conduct = 2
  density = 1
  expand = 3
  formula = G4_MUSCLE_WITH_SUCROSE
  name = G4_MUSCLE_WITH_SUCROSE
  specific = 4
FEATURE [App::DocumentObjectGroupPython] H_element060  label="H_element : 0.138"  # scripted group (container) (typed FeaturePython)
  n = 0.101969
FEATURE [App::DocumentObjectGroupPython] C_element066  label="C_element : 0.120"  # scripted group (container) (typed FeaturePython)
  n = 0.120058
FEATURE [App::DocumentObjectGroupPython] N_element028  label="N_element : 0.758"  # scripted group (container) (typed FeaturePython)
  n = 0.035451
FEATURE [App::DocumentObjectGroupPython] O_element068  label="O_element : 0.743"  # scripted group (container) (typed FeaturePython)
  n = 0.742522
FEATURE [App::DocumentObjectGroupPython] G4_MUSCLE_WITHOUT_SUCROSE  # scripted group (container) (typed FeaturePython)
  Dunit = g/cm3
  Dvalue = 1.07
  Group = -> [H_element060,C_element066,N_element028,O_element068]
  conduct = 2
  density = 1
  expand = 3
  formula = G4_MUSCLE_WITHOUT_SUCROSE
  name = G4_MUSCLE_WITHOUT_SUCROSE
  specific = 4
FEATURE [App::DocumentObjectGroupPython] C_element067  label="C_element : 10"  # scripted group (container) (typed FeaturePython)
  n = 10
  ref = C_element
FEATURE [App::DocumentObjectGroupPython] H_element061  label="H_element : 030"  # scripted group (container) (typed FeaturePython)
  n = 8
  ref = H_element
FEATURE [App::DocumentObjectGroupPython] G4_NAPHTHALENE  # scripted group (container) (typed FeaturePython)
  Dunit = g/cm3
  Dvalue = 1.145
  Group = -> [C_element067,H_element061]
  conduct = 2
  density = 1
  expand = 3
  formula = G4_NAPHTHALENE
  name = G4_NAPHTHALENE
  specific = 4
FEATURE [App::DocumentObjectGroupPython] C_element068  label="C_element : 034"  # scripted group (container) (typed FeaturePython)
  n = 6
  ref = C_element
FEATURE [App::DocumentObjectGroupPython] H_element062  label="H_element : 031"  # scripted group (container) (typed FeaturePython)
  n = 5
  ref = H_element
FEATURE [App::DocumentObjectGroupPython] N_element029  label="N_element : 012"  # scripted group (container) (typed FeaturePython)
  n = 1
  ref = N_element
FEATURE [App::DocumentObjectGroupPython] O_element069  label="O_element : 034"  # scripted group (container) (typed FeaturePython)
  n = 2
  ref = O_element
FEATURE [App::DocumentObjectGroupPython] G4_NITROBENZENE  # scripted group (container) (typed FeaturePython)
  Dunit = g/cm3
  Dvalue = 1.19867
  Group = -> [C_element068,H_element062,N_element029,O_element069]
  conduct = 2
  density = 1
  expand = 3
  formula = G4_NITROBENZENE
  name = G4_NITROBENZENE
  specific = 4
FEATURE [App::DocumentObjectGroupPython] N_element030  label="N_element : 013"  # scripted group (container) (typed FeaturePython)
  n = 2
  ref = N_element
FEATURE [App::DocumentObjectGroupPython] O_element070  label="O_element : 035"  # scripted group (container) (typed FeaturePython)
  n = 1
  ref = O_element
FEATURE [App::DocumentObjectGroupPython] G4_NITROUS_OXIDE  # scripted group (container) (typed FeaturePython)
  Dunit = g/cm3
  Dvalue = 0.00183094
  Group = -> [N_element030,O_element070]
  conduct = 2
  density = 1
  expand = 3
  formula = G4_NITROUS_OXIDE
  name = G4_NITROUS_OXIDE
  specific = 4
FEATURE [App::DocumentObjectGroupPython] H_element063  label="H_element : 0.104"  # scripted group (container) (typed FeaturePython)
  n = 0.103509
FEATURE [App::DocumentObjectGroupPython] C_element069  label="C_element : 0.648"  # scripted group (container) (typed FeaturePython)
  n = 0.648416
FEATURE [App::DocumentObjectGroupPython] N_element031  label="N_element : 0.100"  # scripted group (container) (typed FeaturePython)
  n = 0.0995361
FEATURE [App::DocumentObjectGroupPython] O_element071  label="O_element : 0.149"  # scripted group (container) (typed FeaturePython)
  n = 0.148539
FEATURE [App::DocumentObjectGroupPython] G4_NYLON_8062  label="G4_NYLON-8062"  # scripted group (container) (typed FeaturePython)
  Dunit = g/cm3
  Dvalue = 1.08
  Group = -> [H_element063,C_element069,N_element031,O_element071]
  conduct = 2
  density = 1
  expand = 3
  formula = G4_NYLON-8062
  name = G4_NYLON-8062
  specific = 4
FEATURE [App::DocumentObjectGroupPython] C_element070  label="C_element : 035"  # scripted group (container) (typed FeaturePython)
  n = 6
  ref = C_element
FEATURE [App::DocumentObjectGroupPython] H_element064  label="H_element : 11"  # scripted group (container) (typed FeaturePython)
  n = 11
  ref = H_element
FEATURE [App::DocumentObjectGroupPython] N_element032  label="N_element : 014"  # scripted group (container) (typed FeaturePython)
  n = 1
  ref = N_element
FEATURE [App::DocumentObjectGroupPython] O_element072  label="O_element : 036"  # scripted group (container) (typed FeaturePython)
  n = 1
  ref = O_element
FEATURE [App::DocumentObjectGroupPython] G4_NYLON_6_6  label="G4_NYLON-6-6"  # scripted group (container) (typed FeaturePython)
  Dunit = g/cm3
  Dvalue = 1.14
  Group = -> [C_element070,H_element064,N_element032,O_element072]
  conduct = 2
  density = 1
  expand = 3
  formula = G4_NYLON-6-6
  name = G4_NYLON-6-6
  specific = 4
FEATURE [App::DocumentObjectGroupPython] H_element065  label="H_element : 0.139"  # scripted group (container) (typed FeaturePython)
  n = 0.107062
FEATURE [App::DocumentObjectGroupPython] C_element071  label="C_element : 0.680"  # scripted group (container) (typed FeaturePython)
  n = 0.680449
FEATURE [App::DocumentObjectGroupPython] N_element033  label="N_element : 0.099"  # scripted group (container) (typed FeaturePython)
  n = 0.099189
FEATURE [App::DocumentObjectGroupPython] O_element073  label="O_element : 0.113"  # scripted group (container) (typed FeaturePython)
  n = 0.1133
FEATURE [App::DocumentObjectGroupPython] G4_NYLON_6_10  label="G4_NYLON-6-10"  # scripted group (container) (typed FeaturePython)
  Dunit = g/cm3
  Dvalue = 1.14
  Group = -> [H_element065,C_element071,N_element033,O_element073]
  conduct = 2
  density = 1
  expand = 3
  formula = G4_NYLON-6-10
  name = G4_NYLON-6-10
  specific = 4
FEATURE [App::DocumentObjectGroupPython] H_element066  label="H_element : 0.140"  # scripted group (container) (typed FeaturePython)
  n = 0.115476
FEATURE [App::DocumentObjectGroupPython] C_element072  label="C_element : 0.721"  # scripted group (container) (typed FeaturePython)
  n = 0.720818
FEATURE [App::DocumentObjectGroupPython] N_element034  label="N_element : 0.076"  # scripted group (container) (typed FeaturePython)
  n = 0.0764169
FEATURE [App::DocumentObjectGroupPython] O_element074  label="O_element : 0.087"  # scripted group (container) (typed FeaturePython)
  n = 0.0872889
FEATURE [App::DocumentObjectGroupPython] G4_NYLON_11_RILSAN  label="G4_NYLON-11_RILSAN"  # scripted group (container) (typed FeaturePython)
  Dunit = g/cm3
  Dvalue = 1.425
  Group = -> [H_element066,C_element072,N_element034,O_element074]
  conduct = 2
  density = 1
  expand = 3
  formula = G4_NYLON-11_RILSAN
  name = G4_NYLON-11_RILSAN
  specific = 4
FEATURE [App::DocumentObjectGroupPython] C_element073  label="C_element : 8"  # scripted group (container) (typed FeaturePython)
  n = 8
  ref = C_element
FEATURE [App::DocumentObjectGroupPython] H_element067  label="H_element : 18"  # scripted group (container) (typed FeaturePython)
  n = 18
  ref = H_element
FEATURE [App::DocumentObjectGroupPython] G4_OCTANE  # scripted group (container) (typed FeaturePython)
  Dunit = g/cm3
  Dvalue = 0.7026
  Group = -> [C_element073,H_element067]
  conduct = 2
  density = 1
  expand = 3
  formula = G4_OCTANE
  name = G4_OCTANE
  specific = 4
FEATURE [App::DocumentObjectGroupPython] C_element074  label="C_element : 25"  # scripted group (container) (typed FeaturePython)
  n = 25
  ref = C_element
FEATURE [App::DocumentObjectGroupPython] H_element068  label="H_element : 52"  # scripted group (container) (typed FeaturePython)
  n = 52
  ref = H_element
FEATURE [App::DocumentObjectGroupPython] G4_PARAFFIN  # scripted group (container) (typed FeaturePython)
  Dunit = g/cm3
  Dvalue = 0.93
  Group = -> [C_element074,H_element068]
  conduct = 2
  density = 1
  expand = 3
  formula = G4_PARAFFIN
  name = G4_PARAFFIN
  specific = 4
FEATURE [App::DocumentObjectGroupPython] C_element075  label="C_element : 036"  # scripted group (container) (typed FeaturePython)
  n = 5
  ref = C_element
FEATURE [App::DocumentObjectGroupPython] H_element069  label="H_element : 032"  # scripted group (container) (typed FeaturePython)
  n = 12
  ref = H_element
FEATURE [App::DocumentObjectGroupPython] G4_N_PENTANE  label="G4_N-PENTANE"  # scripted group (container) (typed FeaturePython)
  Dunit = g/cm3
  Dvalue = 0.6262
  Group = -> [C_element075,H_element069]
  conduct = 2
  density = 1
  expand = 3
  formula = G4_N-PENTANE
  name = G4_N-PENTANE
  specific = 4
FEATURE [App::DocumentObjectGroupPython] H_element070  label="H_element : 0.014"  # scripted group (container) (typed FeaturePython)
  n = 0.0141
FEATURE [App::DocumentObjectGroupPython] C_element076  label="C_element : 0.072"  # scripted group (container) (typed FeaturePython)
  n = 0.072261
FEATURE [App::DocumentObjectGroupPython] N_element035  label="N_element : 0.019"  # scripted group (container) (typed FeaturePython)
  n = 0.01932
FEATURE [App::DocumentObjectGroupPython] O_element075  label="O_element : 0.066"  # scripted group (container) (typed FeaturePython)
  n = 0.066101
FEATURE [App::DocumentObjectGroupPython] S_element019  label="S_element : 0.020"  # scripted group (container) (typed FeaturePython)
  n = 0.00189
FEATURE [App::DocumentObjectGroupPython] Br_element004  label="Br_element : 0.349"  # scripted group (container) (typed FeaturePython)
  n = 0.349103
FEATURE [App::DocumentObjectGroupPython] Ag_element001  label="Ag_element : 0.474"  # scripted group (container) (typed FeaturePython)
  n = 0.474105
FEATURE [App::DocumentObjectGroupPython] I_element005  label="I_element : 0.003"  # scripted group (container) (typed FeaturePython)
  n = 0.00312
FEATURE [App::DocumentObjectGroupPython] G4_PHOTO_EMULSION  # scripted group (container) (typed FeaturePython)
  Dunit = g/cm3
  Dvalue = 3.815
  Group = -> [H_element070,C_element076,N_element035,O_element075,S_element019,Br_element004,Ag_element001,I_element005]
  conduct = 2
  density = 1
  expand = 3
  formula = G4_PHOTO_EMULSION
  name = G4_PHOTO_EMULSION
  specific = 4
FEATURE [App::DocumentObjectGroupPython] C_element077  label="C_element : 9"  # scripted group (container) (typed FeaturePython)
  n = 9
  ref = C_element
FEATURE [App::DocumentObjectGroupPython] H_element071  label="H_element : 033"  # scripted group (container) (typed FeaturePython)
  n = 10
  ref = H_element
FEATURE [App::DocumentObjectGroupPython] G4_PLASTIC_SC_VINYLTOLUENE  # scripted group (container) (typed FeaturePython)
  Dunit = g/cm3
  Dvalue = 1.032
  Group = -> [C_element077,H_element071]
  conduct = 2
  density = 1
  expand = 3
  formula = G4_PLASTIC_SC_VINYLTOLUENE
  name = G4_PLASTIC_SC_VINYLTOLUENE
  specific = 4
FEATURE [App::DocumentObjectGroupPython] Pu_element001  label="Pu_element : 1"  # scripted group (container) (typed FeaturePython)
  n = 1
  ref = Pu_element
FEATURE [App::DocumentObjectGroupPython] O_element076  label="O_element : 037"  # scripted group (container) (typed FeaturePython)
  n = 2
  ref = O_element
FEATURE [App::DocumentObjectGroupPython] G4_PLUTONIUM_DIOXIDE  # scripted group (container) (typed FeaturePython)
  Dunit = g/cm3
  Dvalue = 11.46
  Group = -> [Pu_element001,O_element076]
  conduct = 2
  density = 1
  expand = 3
  formula = G4_PLUTONIUM_DIOXIDE
  name = G4_PLUTONIUM_DIOXIDE
  specific = 4
FEATURE [App::DocumentObjectGroupPython] C_element078  label="C_element : 037"  # scripted group (container) (typed FeaturePython)
  n = 3
  ref = C_element
FEATURE [App::DocumentObjectGroupPython] H_element072  label="H_element : 034"  # scripted group (container) (typed FeaturePython)
  n = 3
  ref = H_element
FEATURE [App::DocumentObjectGroupPython] N_element036  label="N_element : 015"  # scripted group (container) (typed FeaturePython)
  n = 1
  ref = N_element
FEATURE [App::DocumentObjectGroupPython] G4_POLYACRYLONITRILE  # scripted group (container) (typed FeaturePython)
  Dunit = g/cm3
  Dvalue = 1.17
  Group = -> [C_element078,H_element072,N_element036]
  conduct = 2
  density = 1
  expand = 3
  formula = G4_POLYACRYLONITRILE
  name = G4_POLYACRYLONITRILE
  specific = 4
FEATURE [App::DocumentObjectGroupPython] C_element079  label="C_element : 16"  # scripted group (container) (typed FeaturePython)
  n = 16
  ref = C_element
FEATURE [App::DocumentObjectGroupPython] H_element073  label="H_element : 035"  # scripted group (container) (typed FeaturePython)
  n = 14
  ref = H_element
FEATURE [App::DocumentObjectGroupPython] O_element077  label="O_element : 038"  # scripted group (container) (typed FeaturePython)
  n = 3
  ref = O_element
FEATURE [App::DocumentObjectGroupPython] G4_POLYCARBONATE  # scripted group (container) (typed FeaturePython)
  Dunit = g/cm3
  Dvalue = 1.2
  Group = -> [C_element079,H_element073,O_element077]
  conduct = 2
  density = 1
  expand = 3
  formula = G4_POLYCARBONATE
  name = G4_POLYCARBONATE
  specific = 4
FEATURE [App::DocumentObjectGroupPython] C_element080  label="C_element : 038"  # scripted group (container) (typed FeaturePython)
  n = 8
  ref = C_element
FEATURE [App::DocumentObjectGroupPython] H_element074  label="H_element : 036"  # scripted group (container) (typed FeaturePython)
  n = 7
  ref = H_element
FEATURE [App::DocumentObjectGroupPython] Cl_element017  label="Cl_element : 007"  # scripted group (container) (typed FeaturePython)
  n = 1
  ref = Cl_element
FEATURE [App::DocumentObjectGroupPython] G4_POLYCHLOROSTYRENE  # scripted group (container) (typed FeaturePython)
  Dunit = g/cm3
  Dvalue = 1.3
  Group = -> [C_element080,H_element074,Cl_element017]
  conduct = 2
  density = 1
  expand = 3
  formula = G4_POLYCHLOROSTYRENE
  name = G4_POLYCHLOROSTYRENE
  specific = 4
FEATURE [App::DocumentObjectGroupPython] C_element081  label="C_element : 039"  # scripted group (container) (typed FeaturePython)
  n = 1
  ref = C_element
FEATURE [App::DocumentObjectGroupPython] H_element075  label="H_element : 037"  # scripted group (container) (typed FeaturePython)
  n = 2
  ref = H_element
FEATURE [App::DocumentObjectGroupPython] G4_POLYETHYLENE  # scripted group (container) (typed FeaturePython)
  Dunit = g/cm3
  Dvalue = 0.94
  Group = -> [C_element081,H_element075]
  conduct = 2
  density = 1
  expand = 3
  formula = G4_POLYETHYLENE
  name = G4_POLYETHYLENE
  specific = 4
FEATURE [App::DocumentObjectGroupPython] C_element082  label="C_element : 040"  # scripted group (container) (typed FeaturePython)
  n = 10
  ref = C_element
FEATURE [App::DocumentObjectGroupPython] H_element076  label="H_element : 038"  # scripted group (container) (typed FeaturePython)
  n = 8
  ref = H_element
FEATURE [App::DocumentObjectGroupPython] O_element078  label="O_element : 039"  # scripted group (container) (typed FeaturePython)
  n = 4
  ref = O_element
FEATURE [App::DocumentObjectGroupPython] G4_MYLAR  # scripted group (container) (typed FeaturePython)
  Dunit = g/cm3
  Dvalue = 1.4
  Group = -> [C_element082,H_element076,O_element078]
  conduct = 2
  density = 1
  expand = 3
  formula = G4_MYLAR
  name = G4_MYLAR
  specific = 4
FEATURE [App::DocumentObjectGroupPython] C_element083  label="C_element : 041"  # scripted group (container) (typed FeaturePython)
  n = 5
  ref = C_element
FEATURE [App::DocumentObjectGroupPython] H_element077  label="H_element : 039"  # scripted group (container) (typed FeaturePython)
  n = 8
  ref = H_element
FEATURE [App::DocumentObjectGroupPython] O_element079  label="O_element : 040"  # scripted group (container) (typed FeaturePython)
  n = 2
  ref = O_element
FEATURE [App::DocumentObjectGroupPython] G4_PLEXIGLASS  # scripted group (container) (typed FeaturePython)
  Dunit = g/cm3
  Dvalue = 1.19
  Group = -> [C_element083,H_element077,O_element079]
  conduct = 2
  density = 1
  expand = 3
  formula = G4_PLEXIGLASS
  name = G4_PLEXIGLASS
  specific = 4
FEATURE [App::DocumentObjectGroupPython] C_element084  label="C_element : 042"  # scripted group (container) (typed FeaturePython)
  n = 1
  ref = C_element
FEATURE [App::DocumentObjectGroupPython] H_element078  label="H_element : 040"  # scripted group (container) (typed FeaturePython)
  n = 2
  ref = H_element
FEATURE [App::DocumentObjectGroupPython] O_element080  label="O_element : 041"  # scripted group (container) (typed FeaturePython)
  n = 1
  ref = O_element
FEATURE [App::DocumentObjectGroupPython] G4_POLYOXYMETHYLENE  # scripted group (container) (typed FeaturePython)
  Dunit = g/cm3
  Dvalue = 1.425
  Group = -> [C_element084,H_element078,O_element080]
  conduct = 2
  density = 1
  expand = 3
  formula = G4_POLYOXYMETHYLENE
  name = G4_POLYOXYMETHYLENE
  specific = 4
FEATURE [App::DocumentObjectGroupPython] C_element085  label="C_element : 043"  # scripted group (container) (typed FeaturePython)
  n = 2
  ref = C_element
FEATURE [App::DocumentObjectGroupPython] H_element079  label="H_element : 041"  # scripted group (container) (typed FeaturePython)
  n = 4
  ref = H_element
FEATURE [App::DocumentObjectGroupPython] G4_POLYPROPYLENE  # scripted group (container) (typed FeaturePython)
  Dunit = g/cm3
  Dvalue = 0.9
  Group = -> [C_element085,H_element079]
  conduct = 2
  density = 1
  expand = 3
  formula = G4_POLYPROPYLENE
  name = G4_POLYPROPYLENE
  specific = 4
FEATURE [App::DocumentObjectGroupPython] C_element086  label="C_element : 044"  # scripted group (container) (typed FeaturePython)
  n = 8
  ref = C_element
FEATURE [App::DocumentObjectGroupPython] H_element080  label="H_element : 042"  # scripted group (container) (typed FeaturePython)
  n = 8
  ref = H_element
FEATURE [App::DocumentObjectGroupPython] G4_POLYSTYRENE  # scripted group (container) (typed FeaturePython)
  Dunit = g/cm3
  Dvalue = 1.06
  Group = -> [C_element086,H_element080]
  conduct = 2
  density = 1
  expand = 3
  formula = G4_POLYSTYRENE
  name = G4_POLYSTYRENE
  specific = 4
FEATURE [App::DocumentObjectGroupPython] C_element087  label="C_element : 045"  # scripted group (container) (typed FeaturePython)
  n = 2
  ref = C_element
FEATURE [App::DocumentObjectGroupPython] F_element014  label="F_element : 4"  # scripted group (container) (typed FeaturePython)
  n = 4
  ref = F_element
FEATURE [App::DocumentObjectGroupPython] G4_TEFLON  # scripted group (container) (typed FeaturePython)
  Dunit = g/cm3
  Dvalue = 2.2
  Group = -> [C_element087,F_element014]
  conduct = 2
  density = 1
  expand = 3
  formula = G4_TEFLON
  name = G4_TEFLON
  specific = 4
FEATURE [App::DocumentObjectGroupPython] C_element088  label="C_element : 046"  # scripted group (container) (typed FeaturePython)
  n = 2
  ref = C_element
FEATURE [App::DocumentObjectGroupPython] F_element015  label="F_element : 006"  # scripted group (container) (typed FeaturePython)
  n = 3
  ref = F_element
FEATURE [App::DocumentObjectGroupPython] Cl_element018  label="Cl_element : 008"  # scripted group (container) (typed FeaturePython)
  n = 1
  ref = Cl_element
FEATURE [App::DocumentObjectGroupPython] G4_POLYTRIFLUOROCHLOROETHYLENE  # scripted group (container) (typed FeaturePython)
  Dunit = g/cm3
  Dvalue = 2.1
  Group = -> [C_element088,F_element015,Cl_element018]
  conduct = 2
  density = 1
  expand = 3
  formula = G4_POLYTRIFLUOROCHLOROETHYLENE
  name = G4_POLYTRIFLUOROCHLOROETHYLENE
  specific = 4
FEATURE [App::DocumentObjectGroupPython] C_element089  label="C_element : 047"  # scripted group (container) (typed FeaturePython)
  n = 4
  ref = C_element
FEATURE [App::DocumentObjectGroupPython] H_element081  label="H_element : 043"  # scripted group (container) (typed FeaturePython)
  n = 6
  ref = H_element
FEATURE [App::DocumentObjectGroupPython] O_element081  label="O_element : 042"  # scripted group (container) (typed FeaturePython)
  n = 2
  ref = O_element
FEATURE [App::DocumentObjectGroupPython] G4_POLYVINYL_ACETATE  # scripted group (container) (typed FeaturePython)
  Dunit = g/cm3
  Dvalue = 1.19
  Group = -> [C_element089,H_element081,O_element081]
  conduct = 2
  density = 1
  expand = 3
  formula = G4_POLYVINYL_ACETATE
  name = G4_POLYVINYL_ACETATE
  specific = 4
FEATURE [App::DocumentObjectGroupPython] C_element090  label="C_element : 048"  # scripted group (container) (typed FeaturePython)
  n = 2
  ref = C_element
FEATURE [App::DocumentObjectGroupPython] H_element082  label="H_element : 044"  # scripted group (container) (typed FeaturePython)
  n = 4
  ref = H_element
FEATURE [App::DocumentObjectGroupPython] O_element082  label="O_element : 043"  # scripted group (container) (typed FeaturePython)
  n = 1
  ref = O_element
FEATURE [App::DocumentObjectGroupPython] G4_POLYVINYL_ALCOHOL  # scripted group (container) (typed FeaturePython)
  Dunit = g/cm3
  Dvalue = 1.3
  Group = -> [C_element090,H_element082,O_element082]
  conduct = 2
  density = 1
  expand = 3
  formula = G4_POLYVINYL_ALCOHOL
  name = G4_POLYVINYL_ALCOHOL
  specific = 4
FEATURE [App::DocumentObjectGroupPython] C_element091  label="C_element : 049"  # scripted group (container) (typed FeaturePython)
  n = 8
  ref = C_element
FEATURE [App::DocumentObjectGroupPython] H_element083  label="H_element : 045"  # scripted group (container) (typed FeaturePython)
  n = 14
  ref = H_element
FEATURE [App::DocumentObjectGroupPython] O_element083  label="O_element : 044"  # scripted group (container) (typed FeaturePython)
  n = 2
  ref = O_element
FEATURE [App::DocumentObjectGroupPython] G4_POLYVINYL_BUTYRAL  # scripted group (container) (typed FeaturePython)
  Dunit = g/cm3
  Dvalue = 1.12
  Group = -> [C_element091,H_element083,O_element083]
  conduct = 2
  density = 1
  expand = 3
  formula = G4_POLYVINYL_BUTYRAL
  name = G4_POLYVINYL_BUTYRAL
  specific = 4
FEATURE [App::DocumentObjectGroupPython] C_element092  label="C_element : 050"  # scripted group (container) (typed FeaturePython)
  n = 2
  ref = C_element
FEATURE [App::DocumentObjectGroupPython] H_element084  label="H_element : 046"  # scripted group (container) (typed FeaturePython)
  n = 3
  ref = H_element
FEATURE [App::DocumentObjectGroupPython] Cl_element019  label="Cl_element : 009"  # scripted group (container) (typed FeaturePython)
  n = 1
  ref = Cl_element
FEATURE [App::DocumentObjectGroupPython] G4_POLYVINYL_CHLORIDE  # scripted group (container) (typed FeaturePython)
  Dunit = g/cm3
  Dvalue = 1.3
  Group = -> [C_element092,H_element084,Cl_element019]
  conduct = 2
  density = 1
  expand = 3
  formula = G4_POLYVINYL_CHLORIDE
  name = G4_POLYVINYL_CHLORIDE
  specific = 4
FEATURE [App::DocumentObjectGroupPython] C_element093  label="C_element : 051"  # scripted group (container) (typed FeaturePython)
  n = 2
  ref = C_element
FEATURE [App::DocumentObjectGroupPython] H_element085  label="H_element : 047"  # scripted group (container) (typed FeaturePython)
  n = 2
  ref = H_element
FEATURE [App::DocumentObjectGroupPython] Cl_element020  label="Cl_element : 010"  # scripted group (container) (typed FeaturePython)
  n = 2
  ref = Cl_element
FEATURE [App::DocumentObjectGroupPython] G4_POLYVINYLIDENE_CHLORIDE  # scripted group (container) (typed FeaturePython)
  Dunit = g/cm3
  Dvalue = 1.7
  Group = -> [C_element093,H_element085,Cl_element020]
  conduct = 2
  density = 1
  expand = 3
  formula = G4_POLYVINYLIDENE_CHLORIDE
  name = G4_POLYVINYLIDENE_CHLORIDE
  specific = 4
FEATURE [App::DocumentObjectGroupPython] C_element094  label="C_element : 052"  # scripted group (container) (typed FeaturePython)
  n = 2
  ref = C_element
FEATURE [App::DocumentObjectGroupPython] H_element086  label="H_element : 048"  # scripted group (container) (typed FeaturePython)
  n = 2
  ref = H_element
FEATURE [App::DocumentObjectGroupPython] F_element016  label="F_element : 007"  # scripted group (container) (typed FeaturePython)
  n = 2
  ref = F_element
FEATURE [App::DocumentObjectGroupPython] G4_POLYVINYLIDENE_FLUORIDE  # scripted group (container) (typed FeaturePython)
  Dunit = g/cm3
  Dvalue = 1.76
  Group = -> [C_element094,H_element086,F_element016]
  conduct = 2
  density = 1
  expand = 3
  formula = G4_POLYVINYLIDENE_FLUORIDE
  name = G4_POLYVINYLIDENE_FLUORIDE
  specific = 4
FEATURE [App::DocumentObjectGroupPython] C_element095  label="C_element : 053"  # scripted group (container) (typed FeaturePython)
  n = 6
  ref = C_element
FEATURE [App::DocumentObjectGroupPython] H_element087  label="H_element : 9"  # scripted group (container) (typed FeaturePython)
  n = 9
  ref = H_element
FEATURE [App::DocumentObjectGroupPython] N_element037  label="N_element : 016"  # scripted group (container) (typed FeaturePython)
  n = 1
  ref = N_element
FEATURE [App::DocumentObjectGroupPython] O_element084  label="O_element : 045"  # scripted group (container) (typed FeaturePython)
  n = 1
  ref = O_element
FEATURE [App::DocumentObjectGroupPython] G4_POLYVINYL_PYRROLIDONE  # scripted group (container) (typed FeaturePython)
  Dunit = g/cm3
  Dvalue = 1.25
  Group = -> [C_element095,H_element087,N_element037,O_element084]
  conduct = 2
  density = 1
  expand = 3
  formula = G4_POLYVINYL_PYRROLIDONE
  name = G4_POLYVINYL_PYRROLIDONE
  specific = 4
FEATURE [App::DocumentObjectGroupPython] K_element008  label="K_element : 1"  # scripted group (container) (typed FeaturePython)
  n = 1
  ref = K_element
FEATURE [App::DocumentObjectGroupPython] I_element006  label="I_element : 003"  # scripted group (container) (typed FeaturePython)
  n = 1
  ref = I_element
FEATURE [App::DocumentObjectGroupPython] G4_POTASSIUM_IODIDE  # scripted group (container) (typed FeaturePython)
  Dunit = g/cm3
  Dvalue = 3.13
  Group = -> [K_element008,I_element006]
  conduct = 2
  density = 1
  expand = 3
  formula = G4_POTASSIUM_IODIDE
  name = G4_POTASSIUM_IODIDE
  specific = 4
FEATURE [App::DocumentObjectGroupPython] K_element009  label="K_element : 2"  # scripted group (container) (typed FeaturePython)
  n = 2
  ref = K_element
FEATURE [App::DocumentObjectGroupPython] O_element085  label="O_element : 046"  # scripted group (container) (typed FeaturePython)
  n = 1
  ref = O_element
FEATURE [App::DocumentObjectGroupPython] G4_POTASSIUM_OXIDE  # scripted group (container) (typed FeaturePython)
  Dunit = g/cm3
  Dvalue = 2.32
  Group = -> [K_element009,O_element085]
  conduct = 2
  density = 1
  expand = 3
  formula = G4_POTASSIUM_OXIDE
  name = G4_POTASSIUM_OXIDE
  specific = 4
FEATURE [App::DocumentObjectGroupPython] C_element096  label="C_element : 054"  # scripted group (container) (typed FeaturePython)
  n = 3
  ref = C_element
FEATURE [App::DocumentObjectGroupPython] H_element088  label="H_element : 049"  # scripted group (container) (typed FeaturePython)
  n = 8
  ref = H_element
FEATURE [App::DocumentObjectGroupPython] G4_PROPANE  # scripted group (container) (typed FeaturePython)
  Dunit = g/cm3
  Dvalue = 0.00187939
  Group = -> [C_element096,H_element088]
  conduct = 2
  density = 1
  expand = 3
  formula = G4_PROPANE
  name = G4_PROPANE
  specific = 4
FEATURE [App::DocumentObjectGroupPython] C_element097  label="C_element : 055"  # scripted group (container) (typed FeaturePython)
  n = 3
  ref = C_element
FEATURE [App::DocumentObjectGroupPython] H_element089  label="H_element : 050"  # scripted group (container) (typed FeaturePython)
  n = 8
  ref = H_element
FEATURE [App::DocumentObjectGroupPython] G4_lPROPANE  # scripted group (container) (typed FeaturePython)
  Dunit = g/cm3
  Dvalue = 0.43
  Group = -> [C_element097,H_element089]
  conduct = 2
  density = 1
  expand = 3
  formula = G4_lPROPANE
  name = G4_lPROPANE
  specific = 4
FEATURE [App::DocumentObjectGroupPython] C_element098  label="C_element : 056"  # scripted group (container) (typed FeaturePython)
  n = 3
  ref = C_element
FEATURE [App::DocumentObjectGroupPython] H_element090  label="H_element : 051"  # scripted group (container) (typed FeaturePython)
  n = 8
  ref = H_element
FEATURE [App::DocumentObjectGroupPython] O_element086  label="O_element : 047"  # scripted group (container) (typed FeaturePython)
  n = 1
  ref = O_element
FEATURE [App::DocumentObjectGroupPython] G4_N_PROPYL_ALCOHOL  label="G4_N-PROPYL_ALCOHOL"  # scripted group (container) (typed FeaturePython)
  Dunit = g/cm3
  Dvalue = 0.8035
  Group = -> [C_element098,H_element090,O_element086]
  conduct = 2
  density = 1
  expand = 3
  formula = G4_N-PROPYL_ALCOHOL
  name = G4_N-PROPYL_ALCOHOL
  specific = 4
FEATURE [App::DocumentObjectGroupPython] C_element099  label="C_element : 057"  # scripted group (container) (typed FeaturePython)
  n = 5
  ref = C_element
FEATURE [App::DocumentObjectGroupPython] H_element091  label="H_element : 052"  # scripted group (container) (typed FeaturePython)
  n = 5
  ref = H_element
FEATURE [App::DocumentObjectGroupPython] N_element038  label="N_element : 017"  # scripted group (container) (typed FeaturePython)
  n = 1
  ref = N_element
FEATURE [App::DocumentObjectGroupPython] G4_PYRIDINE  # scripted group (container) (typed FeaturePython)
  Dunit = g/cm3
  Dvalue = 0.9819
  Group = -> [C_element099,H_element091,N_element038]
  conduct = 2
  density = 1
  expand = 3
  formula = G4_PYRIDINE
  name = G4_PYRIDINE
  specific = 4
FEATURE [App::DocumentObjectGroupPython] H_element092  label="H_element : 0.144"  # scripted group (container) (typed FeaturePython)
  n = 0.143711
FEATURE [App::DocumentObjectGroupPython] C_element100  label="C_element : 0.856"  # scripted group (container) (typed FeaturePython)
  n = 0.856289
FEATURE [App::DocumentObjectGroupPython] G4_RUBBER_BUTYL  # scripted group (container) (typed FeaturePython)
  Dunit = g/cm3
  Dvalue = 0.92
  Group = -> [H_element092,C_element100]
  conduct = 2
  density = 1
  expand = 3
  formula = G4_RUBBER_BUTYL
  name = G4_RUBBER_BUTYL
  specific = 4
FEATURE [App::DocumentObjectGroupPython] H_element093  label="H_element : 0.118"  # scripted group (container) (typed FeaturePython)
  n = 0.118371
FEATURE [App::DocumentObjectGroupPython] C_element101  label="C_element : 0.882"  # scripted group (container) (typed FeaturePython)
  n = 0.881629
FEATURE [App::DocumentObjectGroupPython] G4_RUBBER_NATURAL  # scripted group (container) (typed FeaturePython)
  Dunit = g/cm3
  Dvalue = 0.92
  Group = -> [H_element093,C_element101]
  conduct = 2
  density = 1
  expand = 3
  formula = G4_RUBBER_NATURAL
  name = G4_RUBBER_NATURAL
  specific = 4
FEATURE [App::DocumentObjectGroupPython] H_element094  label="H_element : 0.145"  # scripted group (container) (typed FeaturePython)
  n = 0.05692
FEATURE [App::DocumentObjectGroupPython] C_element102  label="C_element : 0.543"  # scripted group (container) (typed FeaturePython)
  n = 0.542646
FEATURE [App::DocumentObjectGroupPython] Cl_element021  label="Cl_element : 0.400"  # scripted group (container) (typed FeaturePython)
  n = 0.400434
FEATURE [App::DocumentObjectGroupPython] G4_RUBBER_NEOPRENE  # scripted group (container) (typed FeaturePython)
  Dunit = g/cm3
  Dvalue = 1.23
  Group = -> [H_element094,C_element102,Cl_element021]
  conduct = 2
  density = 1
  expand = 3
  formula = G4_RUBBER_NEOPRENE
  name = G4_RUBBER_NEOPRENE
  specific = 4
FEATURE [App::DocumentObjectGroupPython] Si_element006  label="Si_element : 1"  # scripted group (container) (typed FeaturePython)
  n = 1
  ref = Si_element
FEATURE [App::DocumentObjectGroupPython] O_element087  label="O_element : 048"  # scripted group (container) (typed FeaturePython)
  n = 2
  ref = O_element
FEATURE [App::DocumentObjectGroupPython] G4_SILICON_DIOXIDE  # scripted group (container) (typed FeaturePython)
  Dunit = g/cm3
  Dvalue = 2.32
  Group = -> [Si_element006,O_element087]
  conduct = 2
  density = 1
  expand = 3
  formula = G4_SILICON_DIOXIDE
  name = G4_SILICON_DIOXIDE
  specific = 4
FEATURE [App::DocumentObjectGroupPython] Ag_element002  label="Ag_element : 1"  # scripted group (container) (typed FeaturePython)
  n = 1
  ref = Ag_element
FEATURE [App::DocumentObjectGroupPython] Br_element005  label="Br_element : 003"  # scripted group (container) (typed FeaturePython)
  n = 1
  ref = Br_element
FEATURE [App::DocumentObjectGroupPython] G4_SILVER_BROMIDE  # scripted group (container) (typed FeaturePython)
  Dunit = g/cm3
  Dvalue = 6.473
  Group = -> [Ag_element002,Br_element005]
  conduct = 2
  density = 1
  expand = 3
  formula = G4_SILVER_BROMIDE
  name = G4_SILVER_BROMIDE
  specific = 4
FEATURE [App::DocumentObjectGroupPython] Ag_element003  label="Ag_element : 002"  # scripted group (container) (typed FeaturePython)
  n = 1
  ref = Ag_element
FEATURE [App::DocumentObjectGroupPython] Cl_element022  label="Cl_element : 011"  # scripted group (container) (typed FeaturePython)
  n = 1
  ref = Cl_element
FEATURE [App::DocumentObjectGroupPython] G4_SILVER_CHLORIDE  # scripted group (container) (typed FeaturePython)
  Dunit = g/cm3
  Dvalue = 5.56
  Group = -> [Ag_element003,Cl_element022]
  conduct = 2
  density = 1
  expand = 3
  formula = G4_SILVER_CHLORIDE
  name = G4_SILVER_CHLORIDE
  specific = 4
FEATURE [App::DocumentObjectGroupPython] Br_element006  label="Br_element : 0.423"  # scripted group (container) (typed FeaturePython)
  n = 0.422895
FEATURE [App::DocumentObjectGroupPython] Ag_element004  label="Ag_element : 0.574"  # scripted group (container) (typed FeaturePython)
  n = 0.573748
FEATURE [App::DocumentObjectGroupPython] I_element007  label="I_element : 0.649"  # scripted group (container) (typed FeaturePython)
  n = 0.003357
FEATURE [App::DocumentObjectGroupPython] G4_SILVER_HALIDES  # scripted group (container) (typed FeaturePython)
  Dunit = g/cm3
  Dvalue = 6.47
  Group = -> [Br_element006,Ag_element004,I_element007]
  conduct = 2
  density = 1
  expand = 3
  formula = G4_SILVER_HALIDES
  name = G4_SILVER_HALIDES
  specific = 4
FEATURE [App::DocumentObjectGroupPython] Ag_element005  label="Ag_element : 003"  # scripted group (container) (typed FeaturePython)
  n = 1
  ref = Ag_element
FEATURE [App::DocumentObjectGroupPython] I_element008  label="I_element : 004"  # scripted group (container) (typed FeaturePython)
  n = 1
  ref = I_element
FEATURE [App::DocumentObjectGroupPython] G4_SILVER_IODIDE  # scripted group (container) (typed FeaturePython)
  Dunit = g/cm3
  Dvalue = 6.01
  Group = -> [Ag_element005,I_element008]
  conduct = 2
  density = 1
  expand = 3
  formula = G4_SILVER_IODIDE
  name = G4_SILVER_IODIDE
  specific = 4
FEATURE [App::DocumentObjectGroupPython] H_element095  label="H_element : 0.100"  # scripted group (container) (typed FeaturePython)
  n = 0.1
FEATURE [App::DocumentObjectGroupPython] C_element103  label="C_element : 0.204"  # scripted group (container) (typed FeaturePython)
  n = 0.204
FEATURE [App::DocumentObjectGroupPython] N_element039  label="N_element : 0.759"  # scripted group (container) (typed FeaturePython)
  n = 0.042
FEATURE [App::DocumentObjectGroupPython] O_element088  label="O_element : 0.645"  # scripted group (container) (typed FeaturePython)
  n = 0.645
FEATURE [App::DocumentObjectGroupPython] Na_element013  label="Na_element : 0.100"  # scripted group (container) (typed FeaturePython)
  n = 0.002
FEATURE [App::DocumentObjectGroupPython] P_element009  label="P_element : 0.107"  # scripted group (container) (typed FeaturePython)
  n = 0.001
FEATURE [App::DocumentObjectGroupPython] S_element020  label="S_element : 0.021"  # scripted group (container) (typed FeaturePython)
  n = 0.002
FEATURE [App::DocumentObjectGroupPython] Cl_element023  label="Cl_element : 0.590"  # scripted group (container) (typed FeaturePython)
  n = 0.003
FEATURE [App::DocumentObjectGroupPython] K_element010  label="K_element : 0.001"  # scripted group (container) (typed FeaturePython)
  n = 0.001
FEATURE [App::DocumentObjectGroupPython] G4_SKIN_ICRP  # scripted group (container) (typed FeaturePython)
  Dunit = g/cm3
  Dvalue = 1.09
  Group = -> [H_element095,C_element103,N_element039,O_element088,Na_element013,P_element009,S_element020,Cl_element023,K_element010]
  conduct = 2
  density = 1
  expand = 3
  formula = G4_SKIN_ICRP
  name = G4_SKIN_ICRP
  specific = 4
FEATURE [App::DocumentObjectGroupPython] Na_element014  label="Na_element : 2"  # scripted group (container) (typed FeaturePython)
  n = 2
  ref = Na_element
FEATURE [App::DocumentObjectGroupPython] C_element104  label="C_element : 058"  # scripted group (container) (typed FeaturePython)
  n = 1
  ref = C_element
FEATURE [App::DocumentObjectGroupPython] O_element089  label="O_element : 049"  # scripted group (container) (typed FeaturePython)
  n = 3
  ref = O_element
FEATURE [App::DocumentObjectGroupPython] G4_SODIUM_CARBONATE  # scripted group (container) (typed FeaturePython)
  Dunit = g/cm3
  Dvalue = 2.532
  Group = -> [Na_element014,C_element104,O_element089]
  conduct = 2
  density = 1
  expand = 3
  formula = G4_SODIUM_CARBONATE
  name = G4_SODIUM_CARBONATE
  specific = 4
FEATURE [App::DocumentObjectGroupPython] Na_element015  label="Na_element : 1"  # scripted group (container) (typed FeaturePython)
  n = 1
  ref = Na_element
FEATURE [App::DocumentObjectGroupPython] I_element009  label="I_element : 005"  # scripted group (container) (typed FeaturePython)
  n = 1
  ref = I_element
FEATURE [App::DocumentObjectGroupPython] G4_SODIUM_IODIDE  # scripted group (container) (typed FeaturePython)
  Dunit = g/cm3
  Dvalue = 3.667
  Group = -> [Na_element015,I_element009]
  conduct = 2
  density = 1
  expand = 3
  formula = G4_SODIUM_IODIDE
  name = G4_SODIUM_IODIDE
  specific = 4
FEATURE [App::DocumentObjectGroupPython] Na_element016  label="Na_element : 003"  # scripted group (container) (typed FeaturePython)
  n = 2
  ref = Na_element
FEATURE [App::DocumentObjectGroupPython] O_element090  label="O_element : 050"  # scripted group (container) (typed FeaturePython)
  n = 1
  ref = O_element
FEATURE [App::DocumentObjectGroupPython] G4_SODIUM_MONOXIDE  # scripted group (container) (typed FeaturePython)
  Dunit = g/cm3
  Dvalue = 2.27
  Group = -> [Na_element016,O_element090]
  conduct = 2
  density = 1
  expand = 3
  formula = G4_SODIUM_MONOXIDE
  name = G4_SODIUM_MONOXIDE
  specific = 4
FEATURE [App::DocumentObjectGroupPython] Na_element017  label="Na_element : 004"  # scripted group (container) (typed FeaturePython)
  n = 1
  ref = Na_element
FEATURE [App::DocumentObjectGroupPython] N_element040  label="N_element : 018"  # scripted group (container) (typed FeaturePython)
  n = 1
  ref = N_element
FEATURE [App::DocumentObjectGroupPython] O_element091  label="O_element : 051"  # scripted group (container) (typed FeaturePython)
  n = 3
  ref = O_element
FEATURE [App::DocumentObjectGroupPython] G4_SODIUM_NITRATE  # scripted group (container) (typed FeaturePython)
  Dunit = g/cm3
  Dvalue = 2.261
  Group = -> [Na_element017,N_element040,O_element091]
  conduct = 2
  density = 1
  expand = 3
  formula = G4_SODIUM_NITRATE
  name = G4_SODIUM_NITRATE
  specific = 4
FEATURE [App::DocumentObjectGroupPython] C_element105  label="C_element : 059"  # scripted group (container) (typed FeaturePython)
  n = 14
  ref = C_element
FEATURE [App::DocumentObjectGroupPython] H_element096  label="H_element : 053"  # scripted group (container) (typed FeaturePython)
  n = 12
  ref = H_element
FEATURE [App::DocumentObjectGroupPython] G4_STILBENE  # scripted group (container) (typed FeaturePython)
  Dunit = g/cm3
  Dvalue = 0.9707
  Group = -> [C_element105,H_element096]
  conduct = 2
  density = 1
  expand = 3
  formula = G4_STILBENE
  name = G4_STILBENE
  specific = 4
FEATURE [App::DocumentObjectGroupPython] C_element106  label="C_element : 12"  # scripted group (container) (typed FeaturePython)
  n = 12
  ref = C_element
FEATURE [App::DocumentObjectGroupPython] H_element097  label="H_element : 22"  # scripted group (container) (typed FeaturePython)
  n = 22
  ref = H_element
FEATURE [App::DocumentObjectGroupPython] O_element092  label="O_element : 11"  # scripted group (container) (typed FeaturePython)
  n = 11
  ref = O_element
FEATURE [App::DocumentObjectGroupPython] G4_SUCROSE  # scripted group (container) (typed FeaturePython)
  Dunit = g/cm3
  Dvalue = 1.5805
  Group = -> [C_element106,H_element097,O_element092]
  conduct = 2
  density = 1
  expand = 3
  formula = G4_SUCROSE
  name = G4_SUCROSE
  specific = 4
FEATURE [App::DocumentObjectGroupPython] C_element107  label="C_element : 18"  # scripted group (container) (typed FeaturePython)
  n = 18
  ref = C_element
FEATURE [App::DocumentObjectGroupPython] H_element098  label="H_element : 054"  # scripted group (container) (typed FeaturePython)
  n = 14
  ref = H_element
FEATURE [App::DocumentObjectGroupPython] G4_TERPHENYL  # scripted group (container) (typed FeaturePython)
  Dunit = g/cm3
  Dvalue = 1.24
  Group = -> [C_element107,H_element098]
  conduct = 2
  density = 1
  expand = 3
  formula = G4_TERPHENYL
  name = G4_TERPHENYL
  specific = 4
FEATURE [App::DocumentObjectGroupPython] H_element099  label="H_element : 0.146"  # scripted group (container) (typed FeaturePython)
  n = 0.106
FEATURE [App::DocumentObjectGroupPython] C_element108  label="C_element : 0.883"  # scripted group (container) (typed FeaturePython)
  n = 0.099
FEATURE [App::DocumentObjectGroupPython] N_element041  label="N_element : 0.020"  # scripted group (container) (typed FeaturePython)
  n = 0.02
FEATURE [App::DocumentObjectGroupPython] O_element093  label="O_element : 0.766"  # scripted group (container) (typed FeaturePython)
  n = 0.766
FEATURE [App::DocumentObjectGroupPython] Na_element018  label="Na_element : 0.101"  # scripted group (container) (typed FeaturePython)
  n = 0.002
FEATURE [App::DocumentObjectGroupPython] P_element010  label="P_element : 0.108"  # scripted group (container) (typed FeaturePython)
  n = 0.001
FEATURE [App::DocumentObjectGroupPython] S_element021  label="S_element : 0.022"  # scripted group (container) (typed FeaturePython)
  n = 0.002
FEATURE [App::DocumentObjectGroupPython] Cl_element024  label="Cl_element : 0.002"  # scripted group (container) (typed FeaturePython)
  n = 0.002
FEATURE [App::DocumentObjectGroupPython] K_element011  label="K_element : 0.017"  # scripted group (container) (typed FeaturePython)
  n = 0.002
FEATURE [App::DocumentObjectGroupPython] G4_TESTIS_ICRP  # scripted group (container) (typed FeaturePython)
  Dunit = g/cm3
  Dvalue = 1.04
  Group = -> [H_element099,C_element108,N_element041,O_element093,Na_element018,P_element010,S_element021,Cl_element024,K_element011]
  conduct = 2
  density = 1
  expand = 3
  formula = G4_TESTIS_ICRP
  name = G4_TESTIS_ICRP
  specific = 4
FEATURE [App::DocumentObjectGroupPython] C_element109  label="C_element : 060"  # scripted group (container) (typed FeaturePython)
  n = 2
  ref = C_element
FEATURE [App::DocumentObjectGroupPython] Cl_element025  label="Cl_element : 012"  # scripted group (container) (typed FeaturePython)
  n = 4
  ref = Cl_element
FEATURE [App::DocumentObjectGroupPython] G4_TETRACHLOROETHYLENE  # scripted group (container) (typed FeaturePython)
  Dunit = g/cm3
  Dvalue = 1.625
  Group = -> [C_element109,Cl_element025]
  conduct = 2
  density = 1
  expand = 3
  formula = G4_TETRACHLOROETHYLENE
  name = G4_TETRACHLOROETHYLENE
  specific = 4
FEATURE [App::DocumentObjectGroupPython] Tl_element001  label="Tl_element : 1"  # scripted group (container) (typed FeaturePython)
  n = 1
  ref = Tl_element
FEATURE [App::DocumentObjectGroupPython] Cl_element026  label="Cl_element : 013"  # scripted group (container) (typed FeaturePython)
  n = 1
  ref = Cl_element
FEATURE [App::DocumentObjectGroupPython] G4_THALLIUM_CHLORIDE  # scripted group (container) (typed FeaturePython)
  Dunit = g/cm3
  Dvalue = 7.004
  Group = -> [Tl_element001,Cl_element026]
  conduct = 2
  density = 1
  expand = 3
  formula = G4_THALLIUM_CHLORIDE
  name = G4_THALLIUM_CHLORIDE
  specific = 4
FEATURE [App::DocumentObjectGroupPython] H_element100  label="H_element : 0.147"  # scripted group (container) (typed FeaturePython)
  n = 0.105
FEATURE [App::DocumentObjectGroupPython] C_element110  label="C_element : 0.256"  # scripted group (container) (typed FeaturePython)
  n = 0.256
FEATURE [App::DocumentObjectGroupPython] N_element042  label="N_element : 0.760"  # scripted group (container) (typed FeaturePython)
  n = 0.027
FEATURE [App::DocumentObjectGroupPython] O_element094  label="O_element : 0.602"  # scripted group (container) (typed FeaturePython)
  n = 0.602
FEATURE [App::DocumentObjectGroupPython] Na_element019  label="Na_element : 0.102"  # scripted group (container) (typed FeaturePython)
  n = 0.001
FEATURE [App::DocumentObjectGroupPython] P_element011  label="P_element : 0.109"  # scripted group (container) (typed FeaturePython)
  n = 0.002
FEATURE [App::DocumentObjectGroupPython] S_element022  label="S_element : 0.023"  # scripted group (container) (typed FeaturePython)
  n = 0.003
FEATURE [App::DocumentObjectGroupPython] Cl_element027  label="Cl_element : 0.591"  # scripted group (container) (typed FeaturePython)
  n = 0.002
FEATURE [App::DocumentObjectGroupPython] K_element012  label="K_element : 0.018"  # scripted group (container) (typed FeaturePython)
  n = 0.002
FEATURE [App::DocumentObjectGroupPython] G4_TISSUE_SOFT_ICRP  # scripted group (container) (typed FeaturePython)
  Dunit = g/cm3
  Dvalue = 1.03
  Group = -> [H_element100,C_element110,N_element042,O_element094,Na_element019,P_element011,S_element022,Cl_element027,K_element012]
  conduct = 2
  density = 1
  expand = 3
  formula = G4_TISSUE_SOFT_ICRP
  name = G4_TISSUE_SOFT_ICRP
  specific = 4
FEATURE [App::DocumentObjectGroupPython] H_element101  label="H_element : 0.148"  # scripted group (container) (typed FeaturePython)
  n = 0.101
FEATURE [App::DocumentObjectGroupPython] C_element111  label="C_element : 0.111"  # scripted group (container) (typed FeaturePython)
  n = 0.111
FEATURE [App::DocumentObjectGroupPython] N_element043  label="N_element : 0.026"  # scripted group (container) (typed FeaturePython)
  n = 0.026
FEATURE [App::DocumentObjectGroupPython] O_element095  label="O_element : 0.762"  # scripted group (container) (typed FeaturePython)
  n = 0.762
FEATURE [App::DocumentObjectGroupPython] G4_TISSUE_SOFT_ICRU_4  label="G4_TISSUE_SOFT_ICRU-4"  # scripted group (container) (typed FeaturePython)
  Dunit = g/cm3
  Dvalue = 1
  Group = -> [H_element101,C_element111,N_element043,O_element095]
  conduct = 2
  density = 1
  expand = 3
  formula = G4_TISSUE_SOFT_ICRU-4
  name = G4_TISSUE_SOFT_ICRU-4
  specific = 4
FEATURE [App::DocumentObjectGroupPython] H_element102  label="H_element : 0.149"  # scripted group (container) (typed FeaturePython)
  n = 0.101869
FEATURE [App::DocumentObjectGroupPython] C_element112  label="C_element : 0.456"  # scripted group (container) (typed FeaturePython)
  n = 0.456179
FEATURE [App::DocumentObjectGroupPython] N_element044  label="N_element : 0.761"  # scripted group (container) (typed FeaturePython)
  n = 0.035172
FEATURE [App::DocumentObjectGroupPython] O_element096  label="O_element : 0.407"  # scripted group (container) (typed FeaturePython)
  n = 0.40678
FEATURE [App::DocumentObjectGroupPython] G4_TISSUE_METHANE  label="G4_TISSUE-METHANE"  # scripted group (container) (typed FeaturePython)
  Dunit = g/cm3
  Dvalue = 0.00106409
  Group = -> [H_element102,C_element112,N_element044,O_element096]
  conduct = 2
  density = 1
  expand = 3
  formula = G4_TISSUE-METHANE
  name = G4_TISSUE-METHANE
  specific = 4
FEATURE [App::DocumentObjectGroupPython] H_element103  label="H_element : 0.103"  # scripted group (container) (typed FeaturePython)
  n = 0.102672
FEATURE [App::DocumentObjectGroupPython] C_element113  label="C_element : 0.569"  # scripted group (container) (typed FeaturePython)
  n = 0.56894
FEATURE [App::DocumentObjectGroupPython] N_element045  label="N_element : 0.762"  # scripted group (container) (typed FeaturePython)
  n = 0.035022
FEATURE [App::DocumentObjectGroupPython] O_element097  label="O_element : 0.293"  # scripted group (container) (typed FeaturePython)
  n = 0.293366
FEATURE [App::DocumentObjectGroupPython] G4_TISSUE_PROPANE  label="G4_TISSUE-PROPANE"  # scripted group (container) (typed FeaturePython)
  Dunit = g/cm3
  Dvalue = 0.00182628
  Group = -> [H_element103,C_element113,N_element045,O_element097]
  conduct = 2
  density = 1
  expand = 3
  formula = G4_TISSUE-PROPANE
  name = G4_TISSUE-PROPANE
  specific = 4
FEATURE [App::DocumentObjectGroupPython] Ti_element003  label="Ti_element : 1"  # scripted group (container) (typed FeaturePython)
  n = 1
  ref = Ti_element
FEATURE [App::DocumentObjectGroupPython] O_element098  label="O_element : 052"  # scripted group (container) (typed FeaturePython)
  n = 2
  ref = O_element
FEATURE [App::DocumentObjectGroupPython] G4_TITANIUM_DIOXIDE  # scripted group (container) (typed FeaturePython)
  Dunit = g/cm3
  Dvalue = 4.26
  Group = -> [Ti_element003,O_element098]
  conduct = 2
  density = 1
  expand = 3
  formula = G4_TITANIUM_DIOXIDE
  name = G4_TITANIUM_DIOXIDE
  specific = 4
FEATURE [App::DocumentObjectGroupPython] C_element114  label="C_element : 061"  # scripted group (container) (typed FeaturePython)
  n = 7
  ref = C_element
FEATURE [App::DocumentObjectGroupPython] H_element104  label="H_element : 055"  # scripted group (container) (typed FeaturePython)
  n = 8
  ref = H_element
FEATURE [App::DocumentObjectGroupPython] G4_TOLUENE  # scripted group (container) (typed FeaturePython)
  Dunit = g/cm3
  Dvalue = 0.8669
  Group = -> [C_element114,H_element104]
  conduct = 2
  density = 1
  expand = 3
  formula = G4_TOLUENE
  name = G4_TOLUENE
  specific = 4
FEATURE [App::DocumentObjectGroupPython] C_element115  label="C_element : 062"  # scripted group (container) (typed FeaturePython)
  n = 2
  ref = C_element
FEATURE [App::DocumentObjectGroupPython] H_element105  label="H_element : 056"  # scripted group (container) (typed FeaturePython)
  n = 1
  ref = H_element
FEATURE [App::DocumentObjectGroupPython] Cl_element028  label="Cl_element : 014"  # scripted group (container) (typed FeaturePython)
  n = 3
  ref = Cl_element
FEATURE [App::DocumentObjectGroupPython] G4_TRICHLOROETHYLENE  # scripted group (container) (typed FeaturePython)
  Dunit = g/cm3
  Dvalue = 1.46
  Group = -> [C_element115,H_element105,Cl_element028]
  conduct = 2
  density = 1
  expand = 3
  formula = G4_TRICHLOROETHYLENE
  name = G4_TRICHLOROETHYLENE
  specific = 4
FEATURE [App::DocumentObjectGroupPython] C_element116  label="C_element : 063"  # scripted group (container) (typed FeaturePython)
  n = 6
  ref = C_element
FEATURE [App::DocumentObjectGroupPython] H_element106  label="H_element : 15"  # scripted group (container) (typed FeaturePython)
  n = 15
  ref = H_element
FEATURE [App::DocumentObjectGroupPython] O_element099  label="O_element : 053"  # scripted group (container) (typed FeaturePython)
  n = 4
  ref = O_element
FEATURE [App::DocumentObjectGroupPython] P_element012  label="P_element : 1"  # scripted group (container) (typed FeaturePython)
  n = 1
  ref = P_element
FEATURE [App::DocumentObjectGroupPython] G4_TRIETHYL_PHOSPHATE  # scripted group (container) (typed FeaturePython)
  Dunit = g/cm3
  Dvalue = 1.07
  Group = -> [C_element116,H_element106,O_element099,P_element012]
  conduct = 2
  density = 1
  expand = 3
  formula = G4_TRIETHYL_PHOSPHATE
  name = G4_TRIETHYL_PHOSPHATE
  specific = 4
FEATURE [App::DocumentObjectGroupPython] W_element003  label="W_element : 003"  # scripted group (container) (typed FeaturePython)
  n = 1
  ref = W_element
FEATURE [App::DocumentObjectGroupPython] F_element017  label="F_element : 6"  # scripted group (container) (typed FeaturePython)
  n = 6
  ref = F_element
FEATURE [App::DocumentObjectGroupPython] G4_TUNGSTEN_HEXAFLUORIDE  # scripted group (container) (typed FeaturePython)
  Dunit = g/cm3
  Dvalue = 2.4
  Group = -> [W_element003,F_element017]
  conduct = 2
  density = 1
  expand = 3
  formula = G4_TUNGSTEN_HEXAFLUORIDE
  name = G4_TUNGSTEN_HEXAFLUORIDE
  specific = 4
FEATURE [App::DocumentObjectGroupPython] U_element001  label="U_element : 1"  # scripted group (container) (typed FeaturePython)
  n = 1
  ref = U_element
FEATURE [App::DocumentObjectGroupPython] C_element117  label="C_element : 064"  # scripted group (container) (typed FeaturePython)
  n = 2
  ref = C_element
FEATURE [App::DocumentObjectGroupPython] G4_URANIUM_DICARBIDE  # scripted group (container) (typed FeaturePython)
  Dunit = g/cm3
  Dvalue = 11.28
  Group = -> [U_element001,C_element117]
  conduct = 2
  density = 1
  expand = 3
  formula = G4_URANIUM_DICARBIDE
  name = G4_URANIUM_DICARBIDE
  specific = 4
FEATURE [App::DocumentObjectGroupPython] U_element002  label="U_element : 002"  # scripted group (container) (typed FeaturePython)
  n = 1
  ref = U_element
FEATURE [App::DocumentObjectGroupPython] C_element118  label="C_element : 065"  # scripted group (container) (typed FeaturePython)
  n = 1
  ref = C_element
FEATURE [App::DocumentObjectGroupPython] G4_URANIUM_MONOCARBIDE  # scripted group (container) (typed FeaturePython)
  Dunit = g/cm3
  Dvalue = 13.63
  Group = -> [U_element002,C_element118]
  conduct = 2
  density = 1
  expand = 3
  formula = G4_URANIUM_MONOCARBIDE
  name = G4_URANIUM_MONOCARBIDE
  specific = 4
FEATURE [App::DocumentObjectGroupPython] U_element003  label="U_element : 003"  # scripted group (container) (typed FeaturePython)
  n = 1
  ref = U_element
FEATURE [App::DocumentObjectGroupPython] O_element100  label="O_element : 054"  # scripted group (container) (typed FeaturePython)
  n = 2
  ref = O_element
FEATURE [App::DocumentObjectGroupPython] G4_URANIUM_OXIDE  # scripted group (container) (typed FeaturePython)
  Dunit = g/cm3
  Dvalue = 10.96
  Group = -> [U_element003,O_element100]
  conduct = 2
  density = 1
  expand = 3
  formula = G4_URANIUM_OXIDE
  name = G4_URANIUM_OXIDE
  specific = 4
FEATURE [App::DocumentObjectGroupPython] C_element119  label="C_element : 066"  # scripted group (container) (typed FeaturePython)
  n = 1
  ref = C_element
FEATURE [App::DocumentObjectGroupPython] H_element107  label="H_element : 057"  # scripted group (container) (typed FeaturePython)
  n = 4
  ref = H_element
FEATURE [App::DocumentObjectGroupPython] N_element046  label="N_element : 019"  # scripted group (container) (typed FeaturePython)
  n = 2
  ref = N_element
FEATURE [App::DocumentObjectGroupPython] O_element101  label="O_element : 055"  # scripted group (container) (typed FeaturePython)
  n = 1
  ref = O_element
FEATURE [App::DocumentObjectGroupPython] G4_UREA  # scripted group (container) (typed FeaturePython)
  Dunit = g/cm3
  Dvalue = 1.323
  Group = -> [C_element119,H_element107,N_element046,O_element101]
  conduct = 2
  density = 1
  expand = 3
  formula = G4_UREA
  name = G4_UREA
  specific = 4
FEATURE [App::DocumentObjectGroupPython] C_element120  label="C_element : 067"  # scripted group (container) (typed FeaturePython)
  n = 5
  ref = C_element
FEATURE [App::DocumentObjectGroupPython] H_element108  label="H_element : 058"  # scripted group (container) (typed FeaturePython)
  n = 11
  ref = H_element
FEATURE [App::DocumentObjectGroupPython] N_element047  label="N_element : 020"  # scripted group (container) (typed FeaturePython)
  n = 1
  ref = N_element
FEATURE [App::DocumentObjectGroupPython] O_element102  label="O_element : 056"  # scripted group (container) (typed FeaturePython)
  n = 2
  ref = O_element
FEATURE [App::DocumentObjectGroupPython] G4_VALINE  # scripted group (container) (typed FeaturePython)
  Dunit = g/cm3
  Dvalue = 1.23
  Group = -> [C_element120,H_element108,N_element047,O_element102]
  conduct = 2
  density = 1
  expand = 3
  formula = G4_VALINE
  name = G4_VALINE
  specific = 4
FEATURE [App::DocumentObjectGroupPython] H_element109  label="H_element : 0.009"  # scripted group (container) (typed FeaturePython)
  n = 0.009417
FEATURE [App::DocumentObjectGroupPython] C_element121  label="C_element : 0.281"  # scripted group (container) (typed FeaturePython)
  n = 0.280555
FEATURE [App::DocumentObjectGroupPython] F_element018  label="F_element : 0.710"  # scripted group (container) (typed FeaturePython)
  n = 0.710028
FEATURE [App::DocumentObjectGroupPython] G4_VITON  # scripted group (container) (typed FeaturePython)
  Dunit = g/cm3
  Dvalue = 1.8
  Group = -> [H_element109,C_element121,F_element018]
  conduct = 2
  density = 1
  expand = 3
  formula = G4_VITON
  name = G4_VITON
  specific = 4
FEATURE [App::DocumentObjectGroupPython] H_element110  label="H_element : 059"  # scripted group (container) (typed FeaturePython)
  n = 2
  ref = H_element
FEATURE [App::DocumentObjectGroupPython] O_element103  label="O_element : 057"  # scripted group (container) (typed FeaturePython)
  n = 1
  ref = O_element
FEATURE [App::DocumentObjectGroupPython] G4_WATER  # scripted group (container) (typed FeaturePython)
  Dunit = g/cm3
  Dvalue = 1
  Group = -> [H_element110,O_element103]
  conduct = 2
  density = 1
  expand = 3
  formula = G4_WATER
  name = G4_WATER
  specific = 4
FEATURE [App::DocumentObjectGroupPython] H_element111  label="H_element : 060"  # scripted group (container) (typed FeaturePython)
  n = 2
  ref = H_element
FEATURE [App::DocumentObjectGroupPython] O_element104  label="O_element : 058"  # scripted group (container) (typed FeaturePython)
  n = 1
  ref = O_element
FEATURE [App::DocumentObjectGroupPython] G4_WATER_VAPOR  # scripted group (container) (typed FeaturePython)
  Dunit = g/cm3
  Dvalue = 0.000756182
  Group = -> [H_element111,O_element104]
  conduct = 2
  density = 1
  expand = 3
  formula = G4_WATER_VAPOR
  name = G4_WATER_VAPOR
  specific = 4
FEATURE [App::DocumentObjectGroupPython] C_element122  label="C_element : 068"  # scripted group (container) (typed FeaturePython)
  n = 8
  ref = C_element
FEATURE [App::DocumentObjectGroupPython] H_element112  label="H_element : 061"  # scripted group (container) (typed FeaturePython)
  n = 10
  ref = H_element
FEATURE [App::DocumentObjectGroupPython] G4_XYLENE  # scripted group (container) (typed FeaturePython)
  Dunit = g/cm3
  Dvalue = 0.87
  Group = -> [C_element122,H_element112]
  conduct = 2
  density = 1
  expand = 3
  formula = G4_XYLENE
  name = G4_XYLENE
  specific = 4
FEATURE [App::DocumentObjectGroupPython] C_element123  label="C_element : 069"  # scripted group (container) (typed FeaturePython)
  n = 1
  ref = C_element
FEATURE [App::DocumentObjectGroupPython] G4_GRAPHITE  # scripted group (container) (typed FeaturePython)
  Dunit = g/cm3
  Dvalue = 2.21
  Group = -> [C_element123]
  conduct = 2
  density = 1
  expand = 3
  formula = G4_GRAPHITE
  name = G4_GRAPHITE
  specific = 4
FEATURE [App::DocumentObjectGroupPython] NIST  # scripted group (container) (typed FeaturePython)
  Group = -> [G4_A_150_TISSUE,G4_ACETONE,G4_ACETYLENE,G4_ADENINE,G4_ADIPOSE_TISSUE_ICRP,G4_AIR,G4_ALANINE,G4_ALUMINUM_OXIDE,G4_AMBER,G4_AMMONIA,G4_ANILINE,G4_ANTHRACENE,G4_B_100_BONE,G4_BAKELITE,G4_BARIUM_FLUORIDE,G4_BARIUM_SULFATE,G4_BENZENE,G4_BERYLLIUM_OXIDE,G4_BGO,G4_BLOOD_ICRP,G4_BONE_COMPACT_ICRU,G4_BONE_CORTICAL_ICRP,G4_BORON_CARBIDE,G4_BORON_OXIDE,G4_BRAIN_ICRP,G4_BUTANE,G4_N_BUTYL_ALCOHOL,G4_C_552,+152 more]
FEATURE [App::DocumentObjectGroupPython] H_element113  label="H_element : 062"  # scripted group (container) (typed FeaturePython)
  n = 1
  ref = H_element
FEATURE [App::DocumentObjectGroupPython] G4_H  # scripted group (container) (typed FeaturePython)
  Dunit = g/cm3
  Dvalue = 8.3748e-05
  Group = -> [H_element113]
  conduct = 2
  density = 1
  expand = 3
  formula = H
  name = G4_H
  specific = 4
FEATURE [App::DocumentObjectGroupPython] He_element001  label="He_element : 1"  # scripted group (container) (typed FeaturePython)
  n = 1
  ref = He_element
FEATURE [App::DocumentObjectGroupPython] G4_He  # scripted group (container) (typed FeaturePython)
  Dunit = g/cm3
  Dvalue = 0.000166322
  Group = -> [He_element001]
  conduct = 2
  density = 1
  expand = 3
  formula = He
  name = G4_He
  specific = 4
FEATURE [App::DocumentObjectGroupPython] Li_element008  label="Li_element : 008"  # scripted group (container) (typed FeaturePython)
  n = 1
  ref = Li_element
FEATURE [App::DocumentObjectGroupPython] G4_Li  # scripted group (container) (typed FeaturePython)
  Dunit = g/cm3
  Dvalue = 0.534
  Group = -> [Li_element008]
  conduct = 2
  density = 1
  expand = 3
  formula = Li
  name = G4_Li
  specific = 4
FEATURE [App::DocumentObjectGroupPython] Be_element002  label="Be_element : 002"  # scripted group (container) (typed FeaturePython)
  n = 1
  ref = Be_element
FEATURE [App::DocumentObjectGroupPython] G4_Be  # scripted group (container) (typed FeaturePython)
  Dunit = g/cm3
  Dvalue = 1.848
  Group = -> [Be_element002]
  conduct = 2
  density = 1
  expand = 3
  formula = Be
  name = G4_Be
  specific = 4
FEATURE [App::DocumentObjectGroupPython] B_element007  label="B_element : 007"  # scripted group (container) (typed FeaturePython)
  n = 1
  ref = B_element
FEATURE [App::DocumentObjectGroupPython] G4_B  # scripted group (container) (typed FeaturePython)
  Dunit = g/cm3
  Dvalue = 2.37
  Group = -> [B_element007]
  conduct = 2
  density = 1
  expand = 3
  formula = B
  name = G4_B
  specific = 4
FEATURE [App::DocumentObjectGroupPython] C_element124  label="C_element : 070"  # scripted group (container) (typed FeaturePython)
  n = 1
  ref = C_element
FEATURE [App::DocumentObjectGroupPython] G4_C  # scripted group (container) (typed FeaturePython)
  Dunit = g/cm3
  Dvalue = 2
  Group = -> [C_element124]
  conduct = 2
  density = 1
  expand = 3
  formula = C
  name = G4_C
  specific = 4
FEATURE [App::DocumentObjectGroupPython] N_element048  label="N_element : 021"  # scripted group (container) (typed FeaturePython)
  n = 1
  ref = N_element
FEATURE [App::DocumentObjectGroupPython] G4_N  # scripted group (container) (typed FeaturePython)
  Dunit = g/cm3
  Dvalue = 0.0011652
  Group = -> [N_element048]
  conduct = 2
  density = 1
  expand = 3
  formula = N
  name = G4_N
  specific = 4
FEATURE [App::DocumentObjectGroupPython] O_element105  label="O_element : 059"  # scripted group (container) (typed FeaturePython)
  n = 1
  ref = O_element
FEATURE [App::DocumentObjectGroupPython] G4_O  # scripted group (container) (typed FeaturePython)
  Dunit = g/cm3
  Dvalue = 0.00133151
  Group = -> [O_element105]
  conduct = 2
  density = 1
  expand = 3
  formula = O
  name = G4_O
  specific = 4
FEATURE [App::DocumentObjectGroupPython] F_element019  label="F_element : 008"  # scripted group (container) (typed FeaturePython)
  n = 1
  ref = F_element
FEATURE [App::DocumentObjectGroupPython] G4_F  # scripted group (container) (typed FeaturePython)
  Dunit = g/cm3
  Dvalue = 0.00158029
  Group = -> [F_element019]
  conduct = 2
  density = 1
  expand = 3
  formula = F
  name = G4_F
  specific = 4
FEATURE [App::DocumentObjectGroupPython] Ne_element001  label="Ne_element : 1"  # scripted group (container) (typed FeaturePython)
  n = 1
  ref = Ne_element
FEATURE [App::DocumentObjectGroupPython] G4_Ne  # scripted group (container) (typed FeaturePython)
  Dunit = g/cm3
  Dvalue = 0.000838505
  Group = -> [Ne_element001]
  conduct = 2
  density = 1
  expand = 3
  formula = Ne
  name = G4_Ne
  specific = 4
FEATURE [App::DocumentObjectGroupPython] Na_element020  label="Na_element : 005"  # scripted group (container) (typed FeaturePython)
  n = 1
  ref = Na_element
FEATURE [App::DocumentObjectGroupPython] G4_Na  # scripted group (container) (typed FeaturePython)
  Dunit = g/cm3
  Dvalue = 0.971
  Group = -> [Na_element020]
  conduct = 2
  density = 1
  expand = 3
  formula = Na
  name = G4_Na
  specific = 4
FEATURE [App::DocumentObjectGroupPython] Mg_element011  label="Mg_element : 005"  # scripted group (container) (typed FeaturePython)
  n = 1
  ref = Mg_element
FEATURE [App::DocumentObjectGroupPython] G4_Mg  # scripted group (container) (typed FeaturePython)
  Dunit = g/cm3
  Dvalue = 1.74
  Group = -> [Mg_element011]
  conduct = 2
  density = 1
  expand = 3
  formula = Mg
  name = G4_Mg
  specific = 4
FEATURE [App::DocumentObjectGroupPython] Al_element004  label="Al_element : 1"  # scripted group (container) (typed FeaturePython)
  n = 1
  ref = Al_element
FEATURE [App::DocumentObjectGroupPython] G4_Al  # scripted group (container) (typed FeaturePython)
  Dunit = g/cm3
  Dvalue = 2.699
  Group = -> [Al_element004]
  conduct = 2
  density = 1
  expand = 3
  formula = Al
  name = G4_Al
  specific = 4
FEATURE [App::DocumentObjectGroupPython] Si_element007  label="Si_element : 002"  # scripted group (container) (typed FeaturePython)
  n = 1
  ref = Si_element
FEATURE [App::DocumentObjectGroupPython] G4_Si  # scripted group (container) (typed FeaturePython)
  Dunit = g/cm3
  Dvalue = 2.33
  Group = -> [Si_element007]
  conduct = 2
  density = 1
  expand = 3
  formula = Si
  name = G4_Si
  specific = 4
FEATURE [App::DocumentObjectGroupPython] P_element013  label="P_element : 002"  # scripted group (container) (typed FeaturePython)
  n = 1
  ref = P_element
FEATURE [App::DocumentObjectGroupPython] G4_P  # scripted group (container) (typed FeaturePython)
  Dunit = g/cm3
  Dvalue = 2.2
  Group = -> [P_element013]
  conduct = 2
  density = 1
  expand = 3
  formula = P
  name = G4_P
  specific = 4
FEATURE [App::DocumentObjectGroupPython] S_element023  label="S_element : 007"  # scripted group (container) (typed FeaturePython)
  n = 1
  ref = S_element
FEATURE [App::DocumentObjectGroupPython] G4_S  # scripted group (container) (typed FeaturePython)
  Dunit = g/cm3
  Dvalue = 2
  Group = -> [S_element023]
  conduct = 2
  density = 1
  expand = 3
  formula = S
  name = G4_S
  specific = 4
FEATURE [App::DocumentObjectGroupPython] Cl_element029  label="Cl_element : 015"  # scripted group (container) (typed FeaturePython)
  n = 1
  ref = Cl_element
FEATURE [App::DocumentObjectGroupPython] G4_Cl  # scripted group (container) (typed FeaturePython)
  Dunit = g/cm3
  Dvalue = 0.00299473
  Group = -> [Cl_element029]
  conduct = 2
  density = 1
  expand = 3
  formula = Cl
  name = G4_Cl
  specific = 4
FEATURE [App::DocumentObjectGroupPython] Ar_element002  label="Ar_element : 1"  # scripted group (container) (typed FeaturePython)
  n = 1
  ref = Ar_element
FEATURE [App::DocumentObjectGroupPython] G4_Ar  # scripted group (container) (typed FeaturePython)
  Dunit = g/cm3
  Dvalue = 0.00166201
  Group = -> [Ar_element002]
  conduct = 2
  density = 1
  expand = 3
  formula = Ar
  name = G4_Ar
  specific = 4
FEATURE [App::DocumentObjectGroupPython] K_element013  label="K_element : 003"  # scripted group (container) (typed FeaturePython)
  n = 1
  ref = K_element
FEATURE [App::DocumentObjectGroupPython] G4_K  # scripted group (container) (typed FeaturePython)
  Dunit = g/cm3
  Dvalue = 0.862
  Group = -> [K_element013]
  conduct = 2
  density = 1
  expand = 3
  formula = K
  name = G4_K
  specific = 4
FEATURE [App::DocumentObjectGroupPython] Ca_element014  label="Ca_element : 007"  # scripted group (container) (typed FeaturePython)
  n = 1
  ref = Ca_element
FEATURE [App::DocumentObjectGroupPython] G4_Ca  # scripted group (container) (typed FeaturePython)
  Dunit = g/cm3
  Dvalue = 1.55
  Group = -> [Ca_element014]
  conduct = 2
  density = 1
  expand = 3
  formula = Ca
  name = G4_Ca
  specific = 4
FEATURE [App::DocumentObjectGroupPython] Sc_element001  label="Sc_element : 1"  # scripted group (container) (typed FeaturePython)
  n = 1
  ref = Sc_element
FEATURE [App::DocumentObjectGroupPython] G4_Sc  # scripted group (container) (typed FeaturePython)
  Dunit = g/cm3
  Dvalue = 2.989
  Group = -> [Sc_element001]
  conduct = 2
  density = 1
  expand = 3
  formula = Sc
  name = G4_Sc
  specific = 4
FEATURE [App::DocumentObjectGroupPython] Ti_element004  label="Ti_element : 002"  # scripted group (container) (typed FeaturePython)
  n = 1
  ref = Ti_element
FEATURE [App::DocumentObjectGroupPython] G4_Ti  # scripted group (container) (typed FeaturePython)
  Dunit = g/cm3
  Dvalue = 4.54
  Group = -> [Ti_element004]
  conduct = 2
  density = 1
  expand = 3
  formula = Ti
  name = G4_Ti
  specific = 4
FEATURE [App::DocumentObjectGroupPython] V_element001  label="V_element : 1"  # scripted group (container) (typed FeaturePython)
  n = 1
  ref = V_element
FEATURE [App::DocumentObjectGroupPython] G4_V  # scripted group (container) (typed FeaturePython)
  Dunit = g/cm3
  Dvalue = 6.11
  Group = -> [V_element001]
  conduct = 2
  density = 1
  expand = 3
  formula = V
  name = G4_V
  specific = 4
FEATURE [App::DocumentObjectGroupPython] Cr_element001  label="Cr_element : 1"  # scripted group (container) (typed FeaturePython)
  n = 1
  ref = Cr_element
FEATURE [App::DocumentObjectGroupPython] G4_Cr  # scripted group (container) (typed FeaturePython)
  Dunit = g/cm3
  Dvalue = 7.18
  Group = -> [Cr_element001]
  conduct = 2
  density = 1
  expand = 3
  formula = Cr
  name = G4_Cr
  specific = 4
FEATURE [App::DocumentObjectGroupPython] Mn_element001  label="Mn_element : 1"  # scripted group (container) (typed FeaturePython)
  n = 1
  ref = Mn_element
FEATURE [App::DocumentObjectGroupPython] G4_Mn  # scripted group (container) (typed FeaturePython)
  Dunit = g/cm3
  Dvalue = 7.44
  Group = -> [Mn_element001]
  conduct = 2
  density = 1
  expand = 3
  formula = Mn
  name = G4_Mn
  specific = 4
FEATURE [App::DocumentObjectGroupPython] Fe_element007  label="Fe_element : 004"  # scripted group (container) (typed FeaturePython)
  n = 1
  ref = Fe_element
FEATURE [App::DocumentObjectGroupPython] G4_Fe  # scripted group (container) (typed FeaturePython)
  Dunit = g/cm3
  Dvalue = 7.874
  Group = -> [Fe_element007]
  conduct = 2
  density = 1
  expand = 3
  formula = Fe
  name = G4_Fe
  specific = 4
FEATURE [App::DocumentObjectGroupPython] Co_element001  label="Co_element : 1"  # scripted group (container) (typed FeaturePython)
  n = 1
  ref = Co_element
FEATURE [App::DocumentObjectGroupPython] G4_Co  # scripted group (container) (typed FeaturePython)
  Dunit = g/cm3
  Dvalue = 8.9
  Group = -> [Co_element001]
  conduct = 2
  density = 1
  expand = 3
  formula = Co
  name = G4_Co
  specific = 4
FEATURE [App::DocumentObjectGroupPython] Ni_element001  label="Ni_element : 1"  # scripted group (container) (typed FeaturePython)
  n = 1
  ref = Ni_element
FEATURE [App::DocumentObjectGroupPython] G4_Ni  # scripted group (container) (typed FeaturePython)
  Dunit = g/cm3
  Dvalue = 8.902
  Group = -> [Ni_element001]
  conduct = 2
  density = 1
  expand = 3
  formula = Ni
  name = G4_Ni
  specific = 4
FEATURE [App::DocumentObjectGroupPython] Cu_element001  label="Cu_element : 1"  # scripted group (container) (typed FeaturePython)
  n = 1
  ref = Cu_element
FEATURE [App::DocumentObjectGroupPython] G4_Cu  # scripted group (container) (typed FeaturePython)
  Dunit = g/cm3
  Dvalue = 8.96
  Group = -> [Cu_element001]
  conduct = 2
  density = 1
  expand = 3
  formula = Cu
  name = G4_Cu
  specific = 4
FEATURE [App::DocumentObjectGroupPython] Zn_element001  label="Zn_element : 1"  # scripted group (container) (typed FeaturePython)
  n = 1
  ref = Zn_element
FEATURE [App::DocumentObjectGroupPython] G4_Zn  # scripted group (container) (typed FeaturePython)
  Dunit = g/cm3
  Dvalue = 7.133
  Group = -> [Zn_element001]
  conduct = 2
  density = 1
  expand = 3
  formula = Zn
  name = G4_Zn
  specific = 4
FEATURE [App::DocumentObjectGroupPython] Ga_element002  label="Ga_element : 002"  # scripted group (container) (typed FeaturePython)
  n = 1
  ref = Ga_element
FEATURE [App::DocumentObjectGroupPython] G4_Ga  # scripted group (container) (typed FeaturePython)
  Dunit = g/cm3
  Dvalue = 5.904
  Group = -> [Ga_element002]
  conduct = 2
  density = 1
  expand = 3
  formula = Ga
  name = G4_Ga
  specific = 4
FEATURE [App::DocumentObjectGroupPython] Ge_element002  label="Ge_element : 1"  # scripted group (container) (typed FeaturePython)
  n = 1
  ref = Ge_element
FEATURE [App::DocumentObjectGroupPython] G4_Ge  # scripted group (container) (typed FeaturePython)
  Dunit = g/cm3
  Dvalue = 5.323
  Group = -> [Ge_element002]
  conduct = 2
  density = 1
  expand = 3
  formula = Ge
  name = G4_Ge
  specific = 4
FEATURE [App::DocumentObjectGroupPython] As_element003  label="As_element : 002"  # scripted group (container) (typed FeaturePython)
  n = 1
  ref = As_element
FEATURE [App::DocumentObjectGroupPython] G4_As  # scripted group (container) (typed FeaturePython)
  Dunit = g/cm3
  Dvalue = 5.73
  Group = -> [As_element003]
  conduct = 2
  density = 1
  expand = 3
  formula = As
  name = G4_As
  specific = 4
FEATURE [App::DocumentObjectGroupPython] Se_element001  label="Se_element : 1"  # scripted group (container) (typed FeaturePython)
  n = 1
  ref = Se_element
FEATURE [App::DocumentObjectGroupPython] G4_Se  # scripted group (container) (typed FeaturePython)
  Dunit = g/cm3
  Dvalue = 4.5
  Group = -> [Se_element001]
  conduct = 2
  density = 1
  expand = 3
  formula = Se
  name = G4_Se
  specific = 4
FEATURE [App::DocumentObjectGroupPython] Br_element007  label="Br_element : 004"  # scripted group (container) (typed FeaturePython)
  n = 1
  ref = Br_element
FEATURE [App::DocumentObjectGroupPython] G4_Br  # scripted group (container) (typed FeaturePython)
  Dunit = g/cm3
  Dvalue = 0.0070721
  Group = -> [Br_element007]
  conduct = 2
  density = 1
  expand = 3
  formula = Br
  name = G4_Br
  specific = 4
FEATURE [App::DocumentObjectGroupPython] Kr_element001  label="Kr_element : 1"  # scripted group (container) (typed FeaturePython)
  n = 1
  ref = Kr_element
FEATURE [App::DocumentObjectGroupPython] G4_Kr  # scripted group (container) (typed FeaturePython)
  Dunit = g/cm3
  Dvalue = 0.00347832
  Group = -> [Kr_element001]
  conduct = 2
  density = 1
  expand = 3
  formula = Kr
  name = G4_Kr
  specific = 4
FEATURE [App::DocumentObjectGroupPython] Rb_element001  label="Rb_element : 1"  # scripted group (container) (typed FeaturePython)
  n = 1
  ref = Rb_element
FEATURE [App::DocumentObjectGroupPython] G4_Rb  # scripted group (container) (typed FeaturePython)
  Dunit = g/cm3
  Dvalue = 1.532
  Group = -> [Rb_element001]
  conduct = 2
  density = 1
  expand = 3
  formula = Rb
  name = G4_Rb
  specific = 4
FEATURE [App::DocumentObjectGroupPython] Sr_element001  label="Sr_element : 1"  # scripted group (container) (typed FeaturePython)
  n = 1
  ref = Sr_element
FEATURE [App::DocumentObjectGroupPython] G4_Sr  # scripted group (container) (typed FeaturePython)
  Dunit = g/cm3
  Dvalue = 2.54
  Group = -> [Sr_element001]
  conduct = 2
  density = 1
  expand = 3
  formula = Sr
  name = G4_Sr
  specific = 4
FEATURE [App::DocumentObjectGroupPython] Y_element001  label="Y_element : 1"  # scripted group (container) (typed FeaturePython)
  n = 1
  ref = Y_element
FEATURE [App::DocumentObjectGroupPython] G4_Y  # scripted group (container) (typed FeaturePython)
  Dunit = g/cm3
  Dvalue = 4.469
  Group = -> [Y_element001]
  conduct = 2
  density = 1
  expand = 3
  formula = Y
  name = G4_Y
  specific = 4
FEATURE [App::DocumentObjectGroupPython] Zr_element001  label="Zr_element : 1"  # scripted group (container) (typed FeaturePython)
  n = 1
  ref = Zr_element
FEATURE [App::DocumentObjectGroupPython] G4_Zr  # scripted group (container) (typed FeaturePython)
  Dunit = g/cm3
  Dvalue = 6.506
  Group = -> [Zr_element001]
  conduct = 2
  density = 1
  expand = 3
  formula = Zr
  name = G4_Zr
  specific = 4
FEATURE [App::DocumentObjectGroupPython] Nb_element001  label="Nb_element : 1"  # scripted group (container) (typed FeaturePython)
  n = 1
  ref = Nb_element
FEATURE [App::DocumentObjectGroupPython] G4_Nb  # scripted group (container) (typed FeaturePython)
  Dunit = g/cm3
  Dvalue = 8.57
  Group = -> [Nb_element001]
  conduct = 2
  density = 1
  expand = 3
  formula = Nb
  name = G4_Nb
  specific = 4
FEATURE [App::DocumentObjectGroupPython] Mo_element001  label="Mo_element : 1"  # scripted group (container) (typed FeaturePython)
  n = 1
  ref = Mo_element
FEATURE [App::DocumentObjectGroupPython] G4_Mo  # scripted group (container) (typed FeaturePython)
  Dunit = g/cm3
  Dvalue = 10.22
  Group = -> [Mo_element001]
  conduct = 2
  density = 1
  expand = 3
  formula = Mo
  name = G4_Mo
  specific = 4
FEATURE [App::DocumentObjectGroupPython] Tc_element001  label="Tc_element : 1"  # scripted group (container) (typed FeaturePython)
  n = 1
  ref = Tc_element
FEATURE [App::DocumentObjectGroupPython] G4_Tc  # scripted group (container) (typed FeaturePython)
  Dunit = g/cm3
  Dvalue = 11.5
  Group = -> [Tc_element001]
  conduct = 2
  density = 1
  expand = 3
  formula = Tc
  name = G4_Tc
  specific = 4
FEATURE [App::DocumentObjectGroupPython] Ru_element001  label="Ru_element : 1"  # scripted group (container) (typed FeaturePython)
  n = 1
  ref = Ru_element
FEATURE [App::DocumentObjectGroupPython] G4_Ru  # scripted group (container) (typed FeaturePython)
  Dunit = g/cm3
  Dvalue = 12.41
  Group = -> [Ru_element001]
  conduct = 2
  density = 1
  expand = 3
  formula = Ru
  name = G4_Ru
  specific = 4
FEATURE [App::DocumentObjectGroupPython] Rh_element001  label="Rh_element : 1"  # scripted group (container) (typed FeaturePython)
  n = 1
  ref = Rh_element
FEATURE [App::DocumentObjectGroupPython] G4_Rh  # scripted group (container) (typed FeaturePython)
  Dunit = g/cm3
  Dvalue = 12.41
  Group = -> [Rh_element001]
  conduct = 2
  density = 1
  expand = 3
  formula = Rh
  name = G4_Rh
  specific = 4
FEATURE [App::DocumentObjectGroupPython] Pd_element001  label="Pd_element : 1"  # scripted group (container) (typed FeaturePython)
  n = 1
  ref = Pd_element
FEATURE [App::DocumentObjectGroupPython] G4_Pd  # scripted group (container) (typed FeaturePython)
  Dunit = g/cm3
  Dvalue = 12.02
  Group = -> [Pd_element001]
  conduct = 2
  density = 1
  expand = 3
  formula = Pd
  name = G4_Pd
  specific = 4
FEATURE [App::DocumentObjectGroupPython] Ag_element006  label="Ag_element : 004"  # scripted group (container) (typed FeaturePython)
  n = 1
  ref = Ag_element
FEATURE [App::DocumentObjectGroupPython] G4_Ag  # scripted group (container) (typed FeaturePython)
  Dunit = g/cm3
  Dvalue = 10.5
  Group = -> [Ag_element006]
  conduct = 2
  density = 1
  expand = 3
  formula = Ag
  name = G4_Ag
  specific = 4
FEATURE [App::DocumentObjectGroupPython] Cd_element003  label="Cd_element : 003"  # scripted group (container) (typed FeaturePython)
  n = 1
  ref = Cd_element
FEATURE [App::DocumentObjectGroupPython] G4_Cd  # scripted group (container) (typed FeaturePython)
  Dunit = g/cm3
  Dvalue = 8.65
  Group = -> [Cd_element003]
  conduct = 2
  density = 1
  expand = 3
  formula = Cd
  name = G4_Cd
  specific = 4
FEATURE [App::DocumentObjectGroupPython] In_element001  label="In_element : 1"  # scripted group (container) (typed FeaturePython)
  n = 1
  ref = In_element
FEATURE [App::DocumentObjectGroupPython] G4_In  # scripted group (container) (typed FeaturePython)
  Dunit = g/cm3
  Dvalue = 7.31
  Group = -> [In_element001]
  conduct = 2
  density = 1
  expand = 3
  formula = In
  name = G4_In
  specific = 4
FEATURE [App::DocumentObjectGroupPython] Sn_element001  label="Sn_element : 1"  # scripted group (container) (typed FeaturePython)
  n = 1
  ref = Sn_element
FEATURE [App::DocumentObjectGroupPython] G4_Sn  # scripted group (container) (typed FeaturePython)
  Dunit = g/cm3
  Dvalue = 7.31
  Group = -> [Sn_element001]
  conduct = 2
  density = 1
  expand = 3
  formula = Sn
  name = G4_Sn
  specific = 4
FEATURE [App::DocumentObjectGroupPython] Sb_element001  label="Sb_element : 1"  # scripted group (container) (typed FeaturePython)
  n = 1
  ref = Sb_element
FEATURE [App::DocumentObjectGroupPython] G4_Sb  # scripted group (container) (typed FeaturePython)
  Dunit = g/cm3
  Dvalue = 6.691
  Group = -> [Sb_element001]
  conduct = 2
  density = 1
  expand = 3
  formula = Sb
  name = G4_Sb
  specific = 4
FEATURE [App::DocumentObjectGroupPython] Te_element002  label="Te_element : 002"  # scripted group (container) (typed FeaturePython)
  n = 1
  ref = Te_element
FEATURE [App::DocumentObjectGroupPython] G4_Te  # scripted group (container) (typed FeaturePython)
  Dunit = g/cm3
  Dvalue = 6.24
  Group = -> [Te_element002]
  conduct = 2
  density = 1
  expand = 3
  formula = Te
  name = G4_Te
  specific = 4
FEATURE [App::DocumentObjectGroupPython] I_element010  label="I_element : 006"  # scripted group (container) (typed FeaturePython)
  n = 1
  ref = I_element
FEATURE [App::DocumentObjectGroupPython] G4_I  # scripted group (container) (typed FeaturePython)
  Dunit = g/cm3
  Dvalue = 4.93
  Group = -> [I_element010]
  conduct = 2
  density = 1
  expand = 3
  formula = I
  name = G4_I
  specific = 4
FEATURE [App::DocumentObjectGroupPython] Xe_element001  label="Xe_element : 1"  # scripted group (container) (typed FeaturePython)
  n = 1
  ref = Xe_element
FEATURE [App::DocumentObjectGroupPython] G4_Xe  # scripted group (container) (typed FeaturePython)
  Dunit = g/cm3
  Dvalue = 0.00548536
  Group = -> [Xe_element001]
  conduct = 2
  density = 1
  expand = 3
  formula = Xe
  name = G4_Xe
  specific = 4
FEATURE [App::DocumentObjectGroupPython] Cs_element003  label="Cs_element : 003"  # scripted group (container) (typed FeaturePython)
  n = 1
  ref = Cs_element
FEATURE [App::DocumentObjectGroupPython] G4_Cs  # scripted group (container) (typed FeaturePython)
  Dunit = g/cm3
  Dvalue = 1.873
  Group = -> [Cs_element003]
  conduct = 2
  density = 1
  expand = 3
  formula = Cs
  name = G4_Cs
  specific = 4
FEATURE [App::DocumentObjectGroupPython] Ba_element003  label="Ba_element : 003"  # scripted group (container) (typed FeaturePython)
  n = 1
  ref = Ba_element
FEATURE [App::DocumentObjectGroupPython] G4_Ba  # scripted group (container) (typed FeaturePython)
  Dunit = g/cm3
  Dvalue = 3.5
  Group = -> [Ba_element003]
  conduct = 2
  density = 1
  expand = 3
  formula = Ba
  name = G4_Ba
  specific = 4
FEATURE [App::DocumentObjectGroupPython] La_element003  label="La_element : 003"  # scripted group (container) (typed FeaturePython)
  n = 1
  ref = La_element
FEATURE [App::DocumentObjectGroupPython] G4_La  # scripted group (container) (typed FeaturePython)
  Dunit = g/cm3
  Dvalue = 6.154
  Group = -> [La_element003]
  conduct = 2
  density = 1
  expand = 3
  formula = La
  name = G4_La
  specific = 4
FEATURE [App::DocumentObjectGroupPython] Ce_element002  label="Ce_element : 1"  # scripted group (container) (typed FeaturePython)
  n = 1
  ref = Ce_element
FEATURE [App::DocumentObjectGroupPython] G4_Ce  # scripted group (container) (typed FeaturePython)
  Dunit = g/cm3
  Dvalue = 6.657
  Group = -> [Ce_element002]
  conduct = 2
  density = 1
  expand = 3
  formula = Ce
  name = G4_Ce
  specific = 4
FEATURE [App::DocumentObjectGroupPython] Pr_element001  label="Pr_element : 1"  # scripted group (container) (typed FeaturePython)
  n = 1
  ref = Pr_element
FEATURE [App::DocumentObjectGroupPython] G4_Pr  # scripted group (container) (typed FeaturePython)
  Dunit = g/cm3
  Dvalue = 6.71
  Group = -> [Pr_element001]
  conduct = 2
  density = 1
  expand = 3
  formula = Pr
  name = G4_Pr
  specific = 4
FEATURE [App::DocumentObjectGroupPython] Nd_element001  label="Nd_element : 1"  # scripted group (container) (typed FeaturePython)
  n = 1
  ref = Nd_element
FEATURE [App::DocumentObjectGroupPython] G4_Nd  # scripted group (container) (typed FeaturePython)
  Dunit = g/cm3
  Dvalue = 6.9
  Group = -> [Nd_element001]
  conduct = 2
  density = 1
  expand = 3
  formula = Nd
  name = G4_Nd
  specific = 4
FEATURE [App::DocumentObjectGroupPython] Pm_element001  label="Pm_element : 1"  # scripted group (container) (typed FeaturePython)
  n = 1
  ref = Pm_element
FEATURE [App::DocumentObjectGroupPython] G4_Pm  # scripted group (container) (typed FeaturePython)
  Dunit = g/cm3
  Dvalue = 7.22
  Group = -> [Pm_element001]
  conduct = 2
  density = 1
  expand = 3
  formula = Pm
  name = G4_Pm
  specific = 4
FEATURE [App::DocumentObjectGroupPython] Sm_element001  label="Sm_element : 1"  # scripted group (container) (typed FeaturePython)
  n = 1
  ref = Sm_element
FEATURE [App::DocumentObjectGroupPython] G4_Sm  # scripted group (container) (typed FeaturePython)
  Dunit = g/cm3
  Dvalue = 7.46
  Group = -> [Sm_element001]
  conduct = 2
  density = 1
  expand = 3
  formula = Sm
  name = G4_Sm
  specific = 4
FEATURE [App::DocumentObjectGroupPython] Eu_element001  label="Eu_element : 1"  # scripted group (container) (typed FeaturePython)
  n = 1
  ref = Eu_element
FEATURE [App::DocumentObjectGroupPython] G4_Eu  # scripted group (container) (typed FeaturePython)
  Dunit = g/cm3
  Dvalue = 5.243
  Group = -> [Eu_element001]
  conduct = 2
  density = 1
  expand = 3
  formula = Eu
  name = G4_Eu
  specific = 4
FEATURE [App::DocumentObjectGroupPython] Gd_element002  label="Gd_element : 1"  # scripted group (container) (typed FeaturePython)
  n = 1
  ref = Gd_element
FEATURE [App::DocumentObjectGroupPython] G4_Gd  # scripted group (container) (typed FeaturePython)
  Dunit = g/cm3
  Dvalue = 7.9004
  Group = -> [Gd_element002]
  conduct = 2
  density = 1
  expand = 3
  formula = Gd
  name = G4_Gd
  specific = 4
FEATURE [App::DocumentObjectGroupPython] Tb_element001  label="Tb_element : 1"  # scripted group (container) (typed FeaturePython)
  n = 1
  ref = Tb_element
FEATURE [App::DocumentObjectGroupPython] G4_Tb  # scripted group (container) (typed FeaturePython)
  Dunit = g/cm3
  Dvalue = 8.229
  Group = -> [Tb_element001]
  conduct = 2
  density = 1
  expand = 3
  formula = Tb
  name = G4_Tb
  specific = 4
FEATURE [App::DocumentObjectGroupPython] Dy_element001  label="Dy_element : 1"  # scripted group (container) (typed FeaturePython)
  n = 1
  ref = Dy_element
FEATURE [App::DocumentObjectGroupPython] G4_Dy  # scripted group (container) (typed FeaturePython)
  Dunit = g/cm3
  Dvalue = 8.55
  Group = -> [Dy_element001]
  conduct = 2
  density = 1
  expand = 3
  formula = Dy
  name = G4_Dy
  specific = 4
FEATURE [App::DocumentObjectGroupPython] Ho_element001  label="Ho_element : 1"  # scripted group (container) (typed FeaturePython)
  n = 1
  ref = Ho_element
FEATURE [App::DocumentObjectGroupPython] G4_Ho  # scripted group (container) (typed FeaturePython)
  Dunit = g/cm3
  Dvalue = 8.795
  Group = -> [Ho_element001]
  conduct = 2
  density = 1
  expand = 3
  formula = Ho
  name = G4_Ho
  specific = 4
FEATURE [App::DocumentObjectGroupPython] Er_element001  label="Er_element : 1"  # scripted group (container) (typed FeaturePython)
  n = 1
  ref = Er_element
FEATURE [App::DocumentObjectGroupPython] G4_Er  # scripted group (container) (typed FeaturePython)
  Dunit = g/cm3
  Dvalue = 9.066
  Group = -> [Er_element001]
  conduct = 2
  density = 1
  expand = 3
  formula = Er
  name = G4_Er
  specific = 4
FEATURE [App::DocumentObjectGroupPython] Tm_element001  label="Tm_element : 1"  # scripted group (container) (typed FeaturePython)
  n = 1
  ref = Tm_element
FEATURE [App::DocumentObjectGroupPython] G4_Tm  # scripted group (container) (typed FeaturePython)
  Dunit = g/cm3
  Dvalue = 9.321
  Group = -> [Tm_element001]
  conduct = 2
  density = 1
  expand = 3
  formula = Tm
  name = G4_Tm
  specific = 4
FEATURE [App::DocumentObjectGroupPython] Yb_element001  label="Yb_element : 1"  # scripted group (container) (typed FeaturePython)
  n = 1
  ref = Yb_element
FEATURE [App::DocumentObjectGroupPython] G4_Yb  # scripted group (container) (typed FeaturePython)
  Dunit = g/cm3
  Dvalue = 6.73
  Group = -> [Yb_element001]
  conduct = 2
  density = 1
  expand = 3
  formula = Yb
  name = G4_Yb
  specific = 4
FEATURE [App::DocumentObjectGroupPython] Lu_element001  label="Lu_element : 1"  # scripted group (container) (typed FeaturePython)
  n = 1
  ref = Lu_element
FEATURE [App::DocumentObjectGroupPython] G4_Lu  # scripted group (container) (typed FeaturePython)
  Dunit = g/cm3
  Dvalue = 9.84
  Group = -> [Lu_element001]
  conduct = 2
  density = 1
  expand = 3
  formula = Lu
  name = G4_Lu
  specific = 4
FEATURE [App::DocumentObjectGroupPython] Hf_element001  label="Hf_element : 1"  # scripted group (container) (typed FeaturePython)
  n = 1
  ref = Hf_element
FEATURE [App::DocumentObjectGroupPython] G4_Hf  # scripted group (container) (typed FeaturePython)
  Dunit = g/cm3
  Dvalue = 13.31
  Group = -> [Hf_element001]
  conduct = 2
  density = 1
  expand = 3
  formula = Hf
  name = G4_Hf
  specific = 4
FEATURE [App::DocumentObjectGroupPython] Ta_element001  label="Ta_element : 1"  # scripted group (container) (typed FeaturePython)
  n = 1
  ref = Ta_element
FEATURE [App::DocumentObjectGroupPython] G4_Ta  # scripted group (container) (typed FeaturePython)
  Dunit = g/cm3
  Dvalue = 16.654
  Group = -> [Ta_element001]
  conduct = 2
  density = 1
  expand = 3
  formula = Ta
  name = G4_Ta
  specific = 4
FEATURE [App::DocumentObjectGroupPython] W_element004  label="W_element : 004"  # scripted group (container) (typed FeaturePython)
  n = 1
  ref = W_element
FEATURE [App::DocumentObjectGroupPython] G4_W  # scripted group (container) (typed FeaturePython)
  Dunit = g/cm3
  Dvalue = 19.3
  Group = -> [W_element004]
  conduct = 2
  density = 1
  expand = 3
  formula = W
  name = G4_W
  specific = 4
FEATURE [App::DocumentObjectGroupPython] Re_element001  label="Re_element : 1"  # scripted group (container) (typed FeaturePython)
  n = 1
  ref = Re_element
FEATURE [App::DocumentObjectGroupPython] G4_Re  # scripted group (container) (typed FeaturePython)
  Dunit = g/cm3
  Dvalue = 21.02
  Group = -> [Re_element001]
  conduct = 2
  density = 1
  expand = 3
  formula = Re
  name = G4_Re
  specific = 4
FEATURE [App::DocumentObjectGroupPython] Os_element001  label="Os_element : 1"  # scripted group (container) (typed FeaturePython)
  n = 1
  ref = Os_element
FEATURE [App::DocumentObjectGroupPython] G4_Os  # scripted group (container) (typed FeaturePython)
  Dunit = g/cm3
  Dvalue = 22.57
  Group = -> [Os_element001]
  conduct = 2
  density = 1
  expand = 3
  formula = Os
  name = G4_Os
  specific = 4
FEATURE [App::DocumentObjectGroupPython] Ir_element001  label="Ir_element : 1"  # scripted group (container) (typed FeaturePython)
  n = 1
  ref = Ir_element
FEATURE [App::DocumentObjectGroupPython] G4_Ir  # scripted group (container) (typed FeaturePython)
  Dunit = g/cm3
  Dvalue = 22.42
  Group = -> [Ir_element001]
  conduct = 2
  density = 1
  expand = 3
  formula = Ir
  name = G4_Ir
  specific = 4
FEATURE [App::DocumentObjectGroupPython] Pt_element001  label="Pt_element : 1"  # scripted group (container) (typed FeaturePython)
  n = 1
  ref = Pt_element
FEATURE [App::DocumentObjectGroupPython] G4_Pt  # scripted group (container) (typed FeaturePython)
  Dunit = g/cm3
  Dvalue = 21.45
  Group = -> [Pt_element001]
  conduct = 2
  density = 1
  expand = 3
  formula = Pt
  name = G4_Pt
  specific = 4
FEATURE [App::DocumentObjectGroupPython] Au_element001  label="Au_element : 1"  # scripted group (container) (typed FeaturePython)
  n = 1
  ref = Au_element
FEATURE [App::DocumentObjectGroupPython] G4_Au  # scripted group (container) (typed FeaturePython)
  Dunit = g/cm3
  Dvalue = 19.32
  Group = -> [Au_element001]
  conduct = 2
  density = 1
  expand = 3
  formula = Au
  name = G4_Au
  specific = 4
FEATURE [App::DocumentObjectGroupPython] Hg_element002  label="Hg_element : 002"  # scripted group (container) (typed FeaturePython)
  n = 1
  ref = Hg_element
FEATURE [App::DocumentObjectGroupPython] G4_Hg  # scripted group (container) (typed FeaturePython)
  Dunit = g/cm3
  Dvalue = 13.546
  Group = -> [Hg_element002]
  conduct = 2
  density = 1
  expand = 3
  formula = Hg
  name = G4_Hg
  specific = 4
FEATURE [App::DocumentObjectGroupPython] Tl_element002  label="Tl_element : 002"  # scripted group (container) (typed FeaturePython)
  n = 1
  ref = Tl_element
FEATURE [App::DocumentObjectGroupPython] G4_Tl  # scripted group (container) (typed FeaturePython)
  Dunit = g/cm3
  Dvalue = 11.72
  Group = -> [Tl_element002]
  conduct = 2
  density = 1
  expand = 3
  formula = Tl
  name = G4_Tl
  specific = 4
FEATURE [App::DocumentObjectGroupPython] Pb_element003  label="Pb_element : 1"  # scripted group (container) (typed FeaturePython)
  n = 1
  ref = Pb_element
FEATURE [App::DocumentObjectGroupPython] G4_Pb  # scripted group (container) (typed FeaturePython)
  Dunit = g/cm3
  Dvalue = 11.35
  Group = -> [Pb_element003]
  conduct = 2
  density = 1
  expand = 3
  formula = Pb
  name = G4_Pb
  specific = 4
FEATURE [App::DocumentObjectGroupPython] Bi_element002  label="Bi_element : 1"  # scripted group (container) (typed FeaturePython)
  n = 1
  ref = Bi_element
FEATURE [App::DocumentObjectGroupPython] G4_Bi  # scripted group (container) (typed FeaturePython)
  Dunit = g/cm3
  Dvalue = 9.747
  Group = -> [Bi_element002]
  conduct = 2
  density = 1
  expand = 3
  formula = Bi
  name = G4_Bi
  specific = 4
FEATURE [App::DocumentObjectGroupPython] Po_element001  label="Po_element : 1"  # scripted group (container) (typed FeaturePython)
  n = 1
  ref = Po_element
FEATURE [App::DocumentObjectGroupPython] G4_Po  # scripted group (container) (typed FeaturePython)
  Dunit = g/cm3
  Dvalue = 9.32
  Group = -> [Po_element001]
  conduct = 2
  density = 1
  expand = 3
  formula = Po
  name = G4_Po
  specific = 4
FEATURE [App::DocumentObjectGroupPython] At_element001  label="At_element : 1"  # scripted group (container) (typed FeaturePython)
  n = 1
  ref = At_element
FEATURE [App::DocumentObjectGroupPython] G4_At  # scripted group (container) (typed FeaturePython)
  Dunit = g/cm3
  Dvalue = 9.32
  Group = -> [At_element001]
  conduct = 2
  density = 1
  expand = 3
  formula = At
  name = G4_At
  specific = 4
FEATURE [App::DocumentObjectGroupPython] Rn_element001  label="Rn_element : 1"  # scripted group (container) (typed FeaturePython)
  n = 1
  ref = Rn_element
FEATURE [App::DocumentObjectGroupPython] G4_Rn  # scripted group (container) (typed FeaturePython)
  Dunit = g/cm3
  Dvalue = 0.00900662
  Group = -> [Rn_element001]
  conduct = 2
  density = 1
  expand = 3
  formula = Rn
  name = G4_Rn
  specific = 4
FEATURE [App::DocumentObjectGroupPython] Fr_element001  label="Fr_element : 1"  # scripted group (container) (typed FeaturePython)
  n = 1
  ref = Fr_element
FEATURE [App::DocumentObjectGroupPython] G4_Fr  # scripted group (container) (typed FeaturePython)
  Dunit = g/cm3
  Dvalue = 1
  Group = -> [Fr_element001]
  conduct = 2
  density = 1
  expand = 3
  formula = Fr
  name = G4_Fr
  specific = 4
FEATURE [App::DocumentObjectGroupPython] Ra_element001  label="Ra_element : 1"  # scripted group (container) (typed FeaturePython)
  n = 1
  ref = Ra_element
FEATURE [App::DocumentObjectGroupPython] G4_Ra  # scripted group (container) (typed FeaturePython)
  Dunit = g/cm3
  Dvalue = 5
  Group = -> [Ra_element001]
  conduct = 2
  density = 1
  expand = 3
  formula = Ra
  name = G4_Ra
  specific = 4
FEATURE [App::DocumentObjectGroupPython] Ac_element001  label="Ac_element : 1"  # scripted group (container) (typed FeaturePython)
  n = 1
  ref = Ac_element
FEATURE [App::DocumentObjectGroupPython] G4_Ac  # scripted group (container) (typed FeaturePython)
  Dunit = g/cm3
  Dvalue = 10.07
  Group = -> [Ac_element001]
  conduct = 2
  density = 1
  expand = 3
  formula = Ac
  name = G4_Ac
  specific = 4
FEATURE [App::DocumentObjectGroupPython] Th_element001  label="Th_element : 1"  # scripted group (container) (typed FeaturePython)
  n = 1
  ref = Th_element
FEATURE [App::DocumentObjectGroupPython] G4_Th  # scripted group (container) (typed FeaturePython)
  Dunit = g/cm3
  Dvalue = 11.72
  Group = -> [Th_element001]
  conduct = 2
  density = 1
  expand = 3
  formula = Th
  name = G4_Th
  specific = 4
FEATURE [App::DocumentObjectGroupPython] Pa_element001  label="Pa_element : 1"  # scripted group (container) (typed FeaturePython)
  n = 1
  ref = Pa_element
FEATURE [App::DocumentObjectGroupPython] G4_Pa  # scripted group (container) (typed FeaturePython)
  Dunit = g/cm3
  Dvalue = 15.37
  Group = -> [Pa_element001]
  conduct = 2
  density = 1
  expand = 3
  formula = Pa
  name = G4_Pa
  specific = 4
FEATURE [App::DocumentObjectGroupPython] U_element004  label="U_element : 004"  # scripted group (container) (typed FeaturePython)
  n = 1
  ref = U_element
FEATURE [App::DocumentObjectGroupPython] G4_U  # scripted group (container) (typed FeaturePython)
  Dunit = g/cm3
  Dvalue = 18.95
  Group = -> [U_element004]
  conduct = 2
  density = 1
  expand = 3
  formula = U
  name = G4_U
  specific = 4
FEATURE [App::DocumentObjectGroupPython] Np_element001  label="Np_element : 1"  # scripted group (container) (typed FeaturePython)
  n = 1
  ref = Np_element
FEATURE [App::DocumentObjectGroupPython] G4_Np  # scripted group (container) (typed FeaturePython)
  Dunit = g/cm3
  Dvalue = 20.25
  Group = -> [Np_element001]
  conduct = 2
  density = 1
  expand = 3
  formula = Np
  name = G4_Np
  specific = 4
FEATURE [App::DocumentObjectGroupPython] Pu_element002  label="Pu_element : 002"  # scripted group (container) (typed FeaturePython)
  n = 1
  ref = Pu_element
FEATURE [App::DocumentObjectGroupPython] G4_Pu  # scripted group (container) (typed FeaturePython)
  Dunit = g/cm3
  Dvalue = 19.84
  Group = -> [Pu_element002]
  conduct = 2
  density = 1
  expand = 3
  formula = Pu
  name = G4_Pu
  specific = 4
FEATURE [App::DocumentObjectGroupPython] Am_element001  label="Am_element : 1"  # scripted group (container) (typed FeaturePython)
  n = 1
  ref = Am_element
FEATURE [App::DocumentObjectGroupPython] G4_Am  # scripted group (container) (typed FeaturePython)
  Dunit = g/cm3
  Dvalue = 13.67
  Group = -> [Am_element001]
  conduct = 2
  density = 1
  expand = 3
  formula = Am
  name = G4_Am
  specific = 4
FEATURE [App::DocumentObjectGroupPython] Cm_element001  label="Cm_element : 1"  # scripted group (container) (typed FeaturePython)
  n = 1
  ref = Cm_element
FEATURE [App::DocumentObjectGroupPython] G4_Cm  # scripted group (container) (typed FeaturePython)
  Dunit = g/cm3
  Dvalue = 13.51
  Group = -> [Cm_element001]
  conduct = 2
  density = 1
  expand = 3
  formula = Cm
  name = G4_Cm
  specific = 4
FEATURE [App::DocumentObjectGroupPython] Bk_element001  label="Bk_element : 1"  # scripted group (container) (typed FeaturePython)
  n = 1
  ref = Bk_element
FEATURE [App::DocumentObjectGroupPython] G4_Bk  # scripted group (container) (typed FeaturePython)
  Dunit = g/cm3
  Dvalue = 14
  Group = -> [Bk_element001]
  conduct = 2
  density = 1
  expand = 3
  formula = Bk
  name = G4_Bk
  specific = 4
FEATURE [App::DocumentObjectGroupPython] Cf_element001  label="Cf_element : 1"  # scripted group (container) (typed FeaturePython)
  n = 1
  ref = Cf_element
FEATURE [App::DocumentObjectGroupPython] G4_Cf  # scripted group (container) (typed FeaturePython)
  Dunit = g/cm3
  Dvalue = 10
  Group = -> [Cf_element001]
  conduct = 2
  density = 1
  expand = 3
  formula = Cf
  name = G4_Cf
  specific = 4
FEATURE [App::DocumentObjectGroupPython] Element  # scripted group (container) (typed FeaturePython)
  Group = -> [G4_H,G4_He,G4_Li,G4_Be,G4_B,G4_C,G4_N,G4_O,G4_F,G4_Ne,G4_Na,G4_Mg,G4_Al,G4_Si,G4_P,G4_S,G4_Cl,G4_Ar,G4_K,G4_Ca,G4_Sc,G4_Ti,G4_V,G4_Cr,G4_Mn,G4_Fe,G4_Co,G4_Ni,G4_Cu,G4_Zn,G4_Ga,G4_Ge,G4_As,G4_Se,G4_Br,G4_Kr,G4_Rb,G4_Sr,G4_Y,G4_Zr,G4_Nb,G4_Mo,G4_Tc,G4_Ru,G4_Rh,G4_Pd,G4_Ag,G4_Cd,G4_In,G4_Sn,G4_Sb,G4_Te,G4_I,G4_Xe,G4_Cs,G4_Ba,G4_La,G4_Ce,G4_Pr,G4_Nd,G4_Pm,G4_Sm,G4_Eu,G4_Gd,G4_Tb,G4_Dy,G4_Ho,G4_Er,+30 more]
FEATURE [App::DocumentObjectGroupPython] H_element114  label="H_element : 063"  # scripted group (container) (typed FeaturePython)
  n = 2
  ref = H_element
FEATURE [App::DocumentObjectGroupPython] G4_lH2  # scripted group (container) (typed FeaturePython)
  Dunit = g/cm3
  Dvalue = 0.0708
  Group = -> [H_element114]
  conduct = 2
  density = 1
  expand = 3
  formula = G4_lH2
  name = G4_lH2
  specific = 4
FEATURE [App::DocumentObjectGroupPython] N_element049  label="N_element : 022"  # scripted group (container) (typed FeaturePython)
  n = 2
  ref = N_element
FEATURE [App::DocumentObjectGroupPython] G4_lN2  # scripted group (container) (typed FeaturePython)
  Dunit = g/cm3
  Dvalue = 0.807
  Group = -> [N_element049]
  conduct = 2
  density = 1
  expand = 3
  formula = G4_lN2
  name = G4_lN2
  specific = 4
FEATURE [App::DocumentObjectGroupPython] O_element106  label="O_element : 060"  # scripted group (container) (typed FeaturePython)
  n = 2
  ref = O_element
FEATURE [App::DocumentObjectGroupPython] G4_lO2  # scripted group (container) (typed FeaturePython)
  Dunit = g/cm3
  Dvalue = 1.141
  Group = -> [O_element106]
  conduct = 2
  density = 1
  expand = 3
  formula = G4_lO2
  name = G4_lO2
  specific = 4
FEATURE [App::DocumentObjectGroupPython] Ar  label="Ar : 1"  # scripted group (container) (typed FeaturePython)
  n = 1
  ref = Ar
FEATURE [App::DocumentObjectGroupPython] G4_lAr  # scripted group (container) (typed FeaturePython)
  Dunit = g/cm3
  Dvalue = 1.396
  Group = -> [Ar]
  conduct = 2
  density = 1
  expand = 3
  formula = G4_lAr
  name = G4_lAr
  specific = 4
FEATURE [App::DocumentObjectGroupPython] Br  label="Br : 1"  # scripted group (container) (typed FeaturePython)
  n = 1
  ref = Br
FEATURE [App::DocumentObjectGroupPython] G4_lBr  # scripted group (container) (typed FeaturePython)
  Dunit = g/cm3
  Dvalue = 3.1028
  Group = -> [Br]
  conduct = 2
  density = 1
  expand = 3
  formula = G4_lBr
  name = G4_lBr
  specific = 4
FEATURE [App::DocumentObjectGroupPython] Kr  label="Kr : 1"  # scripted group (container) (typed FeaturePython)
  n = 1
  ref = Kr
FEATURE [App::DocumentObjectGroupPython] G4_lKr  # scripted group (container) (typed FeaturePython)
  Dunit = g/cm3
  Dvalue = 2.418
  Group = -> [Kr]
  conduct = 2
  density = 1
  expand = 3
  formula = G4_lKr
  name = G4_lKr
  specific = 4
FEATURE [App::DocumentObjectGroupPython] Xe  label="Xe : 1"  # scripted group (container) (typed FeaturePython)
  n = 1
  ref = Xe
FEATURE [App::DocumentObjectGroupPython] G4_lXe  # scripted group (container) (typed FeaturePython)
  Dunit = g/cm3
  Dvalue = 2.953
  Group = -> [Xe]
  conduct = 2
  density = 1
  expand = 3
  formula = G4_lXe
  name = G4_lXe
  specific = 4
FEATURE [App::DocumentObjectGroupPython] O_element107  label="O_element : 061"  # scripted group (container) (typed FeaturePython)
  n = 4
  ref = O_element
FEATURE [App::DocumentObjectGroupPython] Pb_element004  label="Pb_element : 002"  # scripted group (container) (typed FeaturePython)
  n = 1
  ref = Pb_element
FEATURE [App::DocumentObjectGroupPython] W_element005  label="W_element : 005"  # scripted group (container) (typed FeaturePython)
  n = 1
  ref = W_element
FEATURE [App::DocumentObjectGroupPython] G4_PbWO4  # scripted group (container) (typed FeaturePython)
  Dunit = g/cm3
  Dvalue = 8.28
  Group = -> [O_element107,Pb_element004,W_element005]
  conduct = 2
  density = 1
  expand = 3
  formula = G4_PbWO4
  name = G4_PbWO4
  specific = 4
FEATURE [App::DocumentObjectGroupPython] alactic  label="alactic : 1"  # scripted group (container) (typed FeaturePython)
  n = 1
  ref = alactic
FEATURE [App::DocumentObjectGroupPython] G4_Galactic  # scripted group (container) (typed FeaturePython)
  Dunit = g/cm3
  Dvalue = 0
  Group = -> [alactic]
  conduct = 2
  density = 1
  expand = 3
  formula = G4_Galactic
  name = G4_Galactic
  specific = 4
FEATURE [App::DocumentObjectGroupPython] RAPHITE_POROUS  label="RAPHITE_POROUS : 1"  # scripted group (container) (typed FeaturePython)
  n = 1
  ref = RAPHITE_POROUS
FEATURE [App::DocumentObjectGroupPython] G4_GRAPHITE_POROUS  # scripted group (container) (typed FeaturePython)
  Dunit = g/cm3
  Dvalue = 1.7
  Group = -> [RAPHITE_POROUS]
  conduct = 2
  density = 1
  expand = 3
  formula = G4_GRAPHITE_POROUS
  name = G4_GRAPHITE_POROUS
  specific = 4
FEATURE [App::DocumentObjectGroupPython] H_element115  label="H_element : 0.150"  # scripted group (container) (typed FeaturePython)
  n = 0.080538
FEATURE [App::DocumentObjectGroupPython] C_element125  label="C_element : 0.600"  # scripted group (container) (typed FeaturePython)
  n = 0.599848
FEATURE [App::DocumentObjectGroupPython] O_element108  label="O_element : 0.320"  # scripted group (container) (typed FeaturePython)
  n = 0.319614
FEATURE [App::DocumentObjectGroupPython] G4_LUCITE  # scripted group (container) (typed FeaturePython)
  Dunit = g/cm3
  Dvalue = 1.19
  Group = -> [H_element115,C_element125,O_element108]
  conduct = 2
  density = 1
  expand = 3
  formula = G4_LUCITE
  name = G4_LUCITE
  specific = 4
FEATURE [App::DocumentObjectGroupPython] Cu_element002  label="Cu_element : 62"  # scripted group (container) (typed FeaturePython)
  n = 62
  ref = Cu_element
FEATURE [App::DocumentObjectGroupPython] Zn_element002  label="Zn_element : 35"  # scripted group (container) (typed FeaturePython)
  n = 35
  ref = Zn_element
FEATURE [App::DocumentObjectGroupPython] Pb_element005  label="Pb_element : 3"  # scripted group (container) (typed FeaturePython)
  n = 3
  ref = Pb_element
FEATURE [App::DocumentObjectGroupPython] G4_BRASS  # scripted group (container) (typed FeaturePython)
  Dunit = g/cm3
  Dvalue = 8.52
  Group = -> [Cu_element002,Zn_element002,Pb_element005]
  conduct = 2
  density = 1
  expand = 3
  formula = G4_BRASS
  name = G4_BRASS
  specific = 4
FEATURE [App::DocumentObjectGroupPython] Cu_element003  label="Cu_element : 89"  # scripted group (container) (typed FeaturePython)
  n = 89
  ref = Cu_element
FEATURE [App::DocumentObjectGroupPython] Zn_element003  label="Zn_element : 9"  # scripted group (container) (typed FeaturePython)
  n = 9
  ref = Zn_element
FEATURE [App::DocumentObjectGroupPython] Pb_element006  label="Pb_element : 2"  # scripted group (container) (typed FeaturePython)
  n = 2
  ref = Pb_element
FEATURE [App::DocumentObjectGroupPython] G4_BRONZE  # scripted group (container) (typed FeaturePython)
  Dunit = g/cm3
  Dvalue = 8.82
  Group = -> [Cu_element003,Zn_element003,Pb_element006]
  conduct = 2
  density = 1
  expand = 3
  formula = G4_BRONZE
  name = G4_BRONZE
  specific = 4
FEATURE [App::DocumentObjectGroupPython] Fe_element008  label="Fe_element : 74"  # scripted group (container) (typed FeaturePython)
  n = 74
  ref = Fe_element
FEATURE [App::DocumentObjectGroupPython] Cr_element002  label="Cr_element : 18"  # scripted group (container) (typed FeaturePython)
  n = 18
  ref = Cr_element
FEATURE [App::DocumentObjectGroupPython] Ni_element002  label="Ni_element : 8"  # scripted group (container) (typed FeaturePython)
  n = 8
  ref = Ni_element
FEATURE [App::DocumentObjectGroupPython] G4_STAINLESS_STEEL  label="G4_STAINLESS-STEEL"  # scripted group (container) (typed FeaturePython)
  Dunit = g/cm3
  Dvalue = 8
  Group = -> [Fe_element008,Cr_element002,Ni_element002]
  conduct = 2
  density = 1
  expand = 3
  formula = G4_STAINLESS-STEEL
  name = G4_STAINLESS-STEEL
  specific = 4
FEATURE [App::DocumentObjectGroupPython] H_element116  label="H_element : 064"  # scripted group (container) (typed FeaturePython)
  n = 18
  ref = H_element
FEATURE [App::DocumentObjectGroupPython] C_element126  label="C_element : 071"  # scripted group (container) (typed FeaturePython)
  n = 12
  ref = C_element
FEATURE [App::DocumentObjectGroupPython] O_element109  label="O_element : 062"  # scripted group (container) (typed FeaturePython)
  n = 7
  ref = O_element
FEATURE [App::DocumentObjectGroupPython] G4_CR39  # scripted group (container) (typed FeaturePython)
  Dunit = g/cm3
  Dvalue = 1.32
  Group = -> [H_element116,C_element126,O_element109]
  conduct = 2
  density = 1
  expand = 3
  formula = G4_CR39
  name = G4_CR39
  specific = 4
FEATURE [App::DocumentObjectGroupPython] H_element117  label="H_element : 38"  # scripted group (container) (typed FeaturePython)
  n = 38
  ref = H_element
FEATURE [App::DocumentObjectGroupPython] C_element127  label="C_element : 072"  # scripted group (container) (typed FeaturePython)
  n = 18
  ref = C_element
FEATURE [App::DocumentObjectGroupPython] O_element110  label="O_element : 063"  # scripted group (container) (typed FeaturePython)
  n = 1
  ref = O_element
FEATURE [App::DocumentObjectGroupPython] G4_OCTADECANOL  # scripted group (container) (typed FeaturePython)
  Dunit = g/cm3
  Dvalue = 0.812
  Group = -> [H_element117,C_element127,O_element110]
  conduct = 2
  density = 1
  expand = 3
  formula = G4_OCTADECANOL
  name = G4_OCTADECANOL
  specific = 4
FEATURE [App::DocumentObjectGroupPython] HEP  # scripted group (container) (typed FeaturePython)
  Group = -> [G4_lH2,G4_lN2,G4_lO2,G4_lAr,G4_lBr,G4_lKr,G4_lXe,G4_PbWO4,G4_Galactic,G4_GRAPHITE_POROUS,G4_LUCITE,G4_BRASS,G4_BRONZE,G4_STAINLESS_STEEL,G4_CR39,G4_OCTADECANOL]
FEATURE [App::DocumentObjectGroupPython] C_element128  label="C_element : 073"  # scripted group (container) (typed FeaturePython)
  n = 14
  ref = C_element
FEATURE [App::DocumentObjectGroupPython] H_element118  label="H_element : 065"  # scripted group (container) (typed FeaturePython)
  n = 10
  ref = H_element
FEATURE [App::DocumentObjectGroupPython] O_element111  label="O_element : 064"  # scripted group (container) (typed FeaturePython)
  n = 2
  ref = O_element
FEATURE [App::DocumentObjectGroupPython] N_element050  label="N_element : 023"  # scripted group (container) (typed FeaturePython)
  n = 2
  ref = N_element
FEATURE [App::DocumentObjectGroupPython] G4_KEVLAR  # scripted group (container) (typed FeaturePython)
  Dunit = g/cm3
  Dvalue = 1.44
  Group = -> [C_element128,H_element118,O_element111,N_element050]
  conduct = 2
  density = 1
  expand = 3
  formula = G4_KEVLAR
  name = G4_KEVLAR
  specific = 4
FEATURE [App::DocumentObjectGroupPython] C_element129  label="C_element : 074"  # scripted group (container) (typed FeaturePython)
  n = 10
  ref = C_element
FEATURE [App::DocumentObjectGroupPython] H_element119  label="H_element : 066"  # scripted group (container) (typed FeaturePython)
  n = 8
  ref = H_element
FEATURE [App::DocumentObjectGroupPython] O_element112  label="O_element : 065"  # scripted group (container) (typed FeaturePython)
  n = 4
  ref = O_element
FEATURE [App::DocumentObjectGroupPython] G4_DACRON  # scripted group (container) (typed FeaturePython)
  Dunit = g/cm3
  Dvalue = 1.4
  Group = -> [C_element129,H_element119,O_element112]
  conduct = 2
  density = 1
  expand = 3
  formula = G4_DACRON
  name = G4_DACRON
  specific = 4
FEATURE [App::DocumentObjectGroupPython] C_element130  label="C_element : 075"  # scripted group (container) (typed FeaturePython)
  n = 4
  ref = C_element
FEATURE [App::DocumentObjectGroupPython] H_element120  label="H_element : 067"  # scripted group (container) (typed FeaturePython)
  n = 5
  ref = H_element
FEATURE [App::DocumentObjectGroupPython] Cl_element030  label="Cl_element : 016"  # scripted group (container) (typed FeaturePython)
  n = 1
  ref = Cl_element
FEATURE [App::DocumentObjectGroupPython] G4_NEOPRENE  # scripted group (container) (typed FeaturePython)
  Dunit = g/cm3
  Dvalue = 1.23
  Group = -> [C_element130,H_element120,Cl_element030]
  conduct = 2
  density = 1
  expand = 3
  formula = G4_NEOPRENE
  name = G4_NEOPRENE
  specific = 4
FEATURE [App::DocumentObjectGroupPython] Space  # scripted group (container) (typed FeaturePython)
  Group = -> [G4_KEVLAR,G4_DACRON,G4_NEOPRENE]
FEATURE [App::DocumentObjectGroupPython] H_element121  label="H_element : 068"  # scripted group (container) (typed FeaturePython)
  n = 5
  ref = H_element
FEATURE [App::DocumentObjectGroupPython] C_element131  label="C_element : 076"  # scripted group (container) (typed FeaturePython)
  n = 4
  ref = C_element
FEATURE [App::DocumentObjectGroupPython] N_element051  label="N_element : 3"  # scripted group (container) (typed FeaturePython)
  n = 3
  ref = N_element
FEATURE [App::DocumentObjectGroupPython] O_element113  label="O_element : 066"  # scripted group (container) (typed FeaturePython)
  n = 1
  ref = O_element
FEATURE [App::DocumentObjectGroupPython] G4_CYTOSINE  # scripted group (container) (typed FeaturePython)
  Dunit = g/cm3
  Dvalue = 1.55
  Group = -> [H_element121,C_element131,N_element051,O_element113]
  conduct = 2
  density = 1
  expand = 3
  formula = G4_CYTOSINE
  name = G4_CYTOSINE
  specific = 4
FEATURE [App::DocumentObjectGroupPython] H_element122  label="H_element : 069"  # scripted group (container) (typed FeaturePython)
  n = 6
  ref = H_element
FEATURE [App::DocumentObjectGroupPython] C_element132  label="C_element : 077"  # scripted group (container) (typed FeaturePython)
  n = 5
  ref = C_element
FEATURE [App::DocumentObjectGroupPython] N_element052  label="N_element : 024"  # scripted group (container) (typed FeaturePython)
  n = 2
  ref = N_element
FEATURE [App::DocumentObjectGroupPython] O_element114  label="O_element : 067"  # scripted group (container) (typed FeaturePython)
  n = 2
  ref = O_element
FEATURE [App::DocumentObjectGroupPython] G4_THYMINE  # scripted group (container) (typed FeaturePython)
  Dunit = g/cm3
  Dvalue = 1.23
  Group = -> [H_element122,C_element132,N_element052,O_element114]
  conduct = 2
  density = 1
  expand = 3
  formula = G4_THYMINE
  name = G4_THYMINE
  specific = 4
FEATURE [App::DocumentObjectGroupPython] H_element123  label="H_element : 070"  # scripted group (container) (typed FeaturePython)
  n = 4
  ref = H_element
FEATURE [App::DocumentObjectGroupPython] C_element133  label="C_element : 078"  # scripted group (container) (typed FeaturePython)
  n = 4
  ref = C_element
FEATURE [App::DocumentObjectGroupPython] N_element053  label="N_element : 025"  # scripted group (container) (typed FeaturePython)
  n = 2
  ref = N_element
FEATURE [App::DocumentObjectGroupPython] O_element115  label="O_element : 068"  # scripted group (container) (typed FeaturePython)
  n = 2
  ref = O_element
FEATURE [App::DocumentObjectGroupPython] G4_URACIL  # scripted group (container) (typed FeaturePython)
  Dunit = g/cm3
  Dvalue = 1.32
  Group = -> [H_element123,C_element133,N_element053,O_element115]
  conduct = 2
  density = 1
  expand = 3
  formula = G4_URACIL
  name = G4_URACIL
  specific = 4
FEATURE [App::DocumentObjectGroupPython] H_element124  label="H_element : 071"  # scripted group (container) (typed FeaturePython)
  n = 4
  ref = H_element
FEATURE [App::DocumentObjectGroupPython] C_element134  label="C_element : 079"  # scripted group (container) (typed FeaturePython)
  n = 5
  ref = C_element
FEATURE [App::DocumentObjectGroupPython] N_element054  label="N_element : 026"  # scripted group (container) (typed FeaturePython)
  n = 5
  ref = N_element
FEATURE [App::DocumentObjectGroupPython] G4_DNA_ADENINE  # scripted group (container) (typed FeaturePython)
  Dunit = g/cm3
  Dvalue = 1
  Group = -> [H_element124,C_element134,N_element054]
  conduct = 2
  density = 1
  expand = 3
  formula = G4_DNA_ADENINE
  name = G4_DNA_ADENINE
  specific = 4
FEATURE [App::DocumentObjectGroupPython] H_element125  label="H_element : 072"  # scripted group (container) (typed FeaturePython)
  n = 4
  ref = H_element
FEATURE [App::DocumentObjectGroupPython] C_element135  label="C_element : 080"  # scripted group (container) (typed FeaturePython)
  n = 5
  ref = C_element
FEATURE [App::DocumentObjectGroupPython] N_element055  label="N_element : 027"  # scripted group (container) (typed FeaturePython)
  n = 5
  ref = N_element
FEATURE [App::DocumentObjectGroupPython] O_element116  label="O_element : 069"  # scripted group (container) (typed FeaturePython)
  n = 1
  ref = O_element
FEATURE [App::DocumentObjectGroupPython] G4_DNA_GUANINE  # scripted group (container) (typed FeaturePython)
  Dunit = g/cm3
  Dvalue = 1
  Group = -> [H_element125,C_element135,N_element055,O_element116]
  conduct = 2
  density = 1
  expand = 3
  formula = G4_DNA_GUANINE
  name = G4_DNA_GUANINE
  specific = 4
FEATURE [App::DocumentObjectGroupPython] H_element126  label="H_element : 073"  # scripted group (container) (typed FeaturePython)
  n = 4
  ref = H_element
FEATURE [App::DocumentObjectGroupPython] C_element136  label="C_element : 081"  # scripted group (container) (typed FeaturePython)
  n = 4
  ref = C_element
FEATURE [App::DocumentObjectGroupPython] N_element056  label="N_element : 028"  # scripted group (container) (typed FeaturePython)
  n = 3
  ref = N_element
FEATURE [App::DocumentObjectGroupPython] O_element117  label="O_element : 070"  # scripted group (container) (typed FeaturePython)
  n = 1
  ref = O_element
FEATURE [App::DocumentObjectGroupPython] G4_DNA_CYTOSINE  # scripted group (container) (typed FeaturePython)
  Dunit = g/cm3
  Dvalue = 1
  Group = -> [H_element126,C_element136,N_element056,O_element117]
  conduct = 2
  density = 1
  expand = 3
  formula = G4_DNA_CYTOSINE
  name = G4_DNA_CYTOSINE
  specific = 4
FEATURE [App::DocumentObjectGroupPython] H_element127  label="H_element : 074"  # scripted group (container) (typed FeaturePython)
  n = 5
  ref = H_element
FEATURE [App::DocumentObjectGroupPython] C_element137  label="C_element : 082"  # scripted group (container) (typed FeaturePython)
  n = 5
  ref = C_element
FEATURE [App::DocumentObjectGroupPython] N_element057  label="N_element : 029"  # scripted group (container) (typed FeaturePython)
  n = 2
  ref = N_element
FEATURE [App::DocumentObjectGroupPython] O_element118  label="O_element : 071"  # scripted group (container) (typed FeaturePython)
  n = 2
  ref = O_element
FEATURE [App::DocumentObjectGroupPython] G4_DNA_THYMINE  # scripted group (container) (typed FeaturePython)
  Dunit = g/cm3
  Dvalue = 1
  Group = -> [H_element127,C_element137,N_element057,O_element118]
  conduct = 2
  density = 1
  expand = 3
  formula = G4_DNA_THYMINE
  name = G4_DNA_THYMINE
  specific = 4
FEATURE [App::DocumentObjectGroupPython] H_element128  label="H_element : 075"  # scripted group (container) (typed FeaturePython)
  n = 3
  ref = H_element
FEATURE [App::DocumentObjectGroupPython] C_element138  label="C_element : 083"  # scripted group (container) (typed FeaturePython)
  n = 4
  ref = C_element
FEATURE [App::DocumentObjectGroupPython] N_element058  label="N_element : 030"  # scripted group (container) (typed FeaturePython)
  n = 2
  ref = N_element
FEATURE [App::DocumentObjectGroupPython] O_element119  label="O_element : 072"  # scripted group (container) (typed FeaturePython)
  n = 2
  ref = O_element
FEATURE [App::DocumentObjectGroupPython] G4_DNA_URACIL  # scripted group (container) (typed FeaturePython)
  Dunit = g/cm3
  Dvalue = 1
  Group = -> [H_element128,C_element138,N_element058,O_element119]
  conduct = 2
  density = 1
  expand = 3
  formula = G4_DNA_URACIL
  name = G4_DNA_URACIL
  specific = 4
FEATURE [App::DocumentObjectGroupPython] H_element129  label="H_element : 076"  # scripted group (container) (typed FeaturePython)
  n = 10
  ref = H_element
FEATURE [App::DocumentObjectGroupPython] C_element139  label="C_element : 084"  # scripted group (container) (typed FeaturePython)
  n = 10
  ref = C_element
FEATURE [App::DocumentObjectGroupPython] N_element059  label="N_element : 031"  # scripted group (container) (typed FeaturePython)
  n = 5
  ref = N_element
FEATURE [App::DocumentObjectGroupPython] O_element120  label="O_element : 073"  # scripted group (container) (typed FeaturePython)
  n = 4
  ref = O_element
FEATURE [App::DocumentObjectGroupPython] G4_DNA_ADENOSINE  # scripted group (container) (typed FeaturePython)
  Dunit = g/cm3
  Dvalue = 1
  Group = -> [H_element129,C_element139,N_element059,O_element120]
  conduct = 2
  density = 1
  expand = 3
  formula = G4_DNA_ADENOSINE
  name = G4_DNA_ADENOSINE
  specific = 4
FEATURE [App::DocumentObjectGroupPython] H_element130  label="H_element : 077"  # scripted group (container) (typed FeaturePython)
  n = 10
  ref = H_element
FEATURE [App::DocumentObjectGroupPython] C_element140  label="C_element : 085"  # scripted group (container) (typed FeaturePython)
  n = 10
  ref = C_element
FEATURE [App::DocumentObjectGroupPython] N_element060  label="N_element : 032"  # scripted group (container) (typed FeaturePython)
  n = 5
  ref = N_element
FEATURE [App::DocumentObjectGroupPython] O_element121  label="O_element : 074"  # scripted group (container) (typed FeaturePython)
  n = 5
  ref = O_element
FEATURE [App::DocumentObjectGroupPython] G4_DNA_GUANOSINE  # scripted group (container) (typed FeaturePython)
  Dunit = g/cm3
  Dvalue = 1
  Group = -> [H_element130,C_element140,N_element060,O_element121]
  conduct = 2
  density = 1
  expand = 3
  formula = G4_DNA_GUANOSINE
  name = G4_DNA_GUANOSINE
  specific = 4
FEATURE [App::DocumentObjectGroupPython] H_element131  label="H_element : 078"  # scripted group (container) (typed FeaturePython)
  n = 10
  ref = H_element
FEATURE [App::DocumentObjectGroupPython] C_element141  label="C_element : 086"  # scripted group (container) (typed FeaturePython)
  n = 9
  ref = C_element
FEATURE [App::DocumentObjectGroupPython] N_element061  label="N_element : 033"  # scripted group (container) (typed FeaturePython)
  n = 3
  ref = N_element
FEATURE [App::DocumentObjectGroupPython] O_element122  label="O_element : 075"  # scripted group (container) (typed FeaturePython)
  n = 5
  ref = O_element
FEATURE [App::DocumentObjectGroupPython] G4_DNA_CYTIDINE  # scripted group (container) (typed FeaturePython)
  Dunit = g/cm3
  Dvalue = 1
  Group = -> [H_element131,C_element141,N_element061,O_element122]
  conduct = 2
  density = 1
  expand = 3
  formula = G4_DNA_CYTIDINE
  name = G4_DNA_CYTIDINE
  specific = 4
FEATURE [App::DocumentObjectGroupPython] H_element132  label="H_element : 079"  # scripted group (container) (typed FeaturePython)
  n = 9
  ref = H_element
FEATURE [App::DocumentObjectGroupPython] C_element142  label="C_element : 087"  # scripted group (container) (typed FeaturePython)
  n = 9
  ref = C_element
FEATURE [App::DocumentObjectGroupPython] N_element062  label="N_element : 034"  # scripted group (container) (typed FeaturePython)
  n = 2
  ref = N_element
FEATURE [App::DocumentObjectGroupPython] O_element123  label="O_element : 076"  # scripted group (container) (typed FeaturePython)
  n = 6
  ref = O_element
FEATURE [App::DocumentObjectGroupPython] G4_DNA_URIDINE  # scripted group (container) (typed FeaturePython)
  Dunit = g/cm3
  Dvalue = 1
  Group = -> [H_element132,C_element142,N_element062,O_element123]
  conduct = 2
  density = 1
  expand = 3
  formula = G4_DNA_URIDINE
  name = G4_DNA_URIDINE
  specific = 4
FEATURE [App::DocumentObjectGroupPython] H_element133  label="H_element : 080"  # scripted group (container) (typed FeaturePython)
  n = 11
  ref = H_element
FEATURE [App::DocumentObjectGroupPython] C_element143  label="C_element : 088"  # scripted group (container) (typed FeaturePython)
  n = 10
  ref = C_element
FEATURE [App::DocumentObjectGroupPython] N_element063  label="N_element : 035"  # scripted group (container) (typed FeaturePython)
  n = 2
  ref = N_element
FEATURE [App::DocumentObjectGroupPython] O_element124  label="O_element : 077"  # scripted group (container) (typed FeaturePython)
  n = 6
  ref = O_element
FEATURE [App::DocumentObjectGroupPython] G4_DNA_METHYLURIDINE  # scripted group (container) (typed FeaturePython)
  Dunit = g/cm3
  Dvalue = 1
  Group = -> [H_element133,C_element143,N_element063,O_element124]
  conduct = 2
  density = 1
  expand = 3
  formula = G4_DNA_METHYLURIDINE
  name = G4_DNA_METHYLURIDINE
  specific = 4
FEATURE [App::DocumentObjectGroupPython] P_element014  label="P_element : 003"  # scripted group (container) (typed FeaturePython)
  n = 1
  ref = P_element
FEATURE [App::DocumentObjectGroupPython] O_element125  label="O_element : 078"  # scripted group (container) (typed FeaturePython)
  n = 3
  ref = O_element
FEATURE [App::DocumentObjectGroupPython] G4_DNA_MONOPHOSPHATE  # scripted group (container) (typed FeaturePython)
  Dunit = g/cm3
  Dvalue = 1
  Group = -> [P_element014,O_element125]
  conduct = 2
  density = 1
  expand = 3
  formula = G4_DNA_MONOPHOSPHATE
  name = G4_DNA_MONOPHOSPHATE
  specific = 4
FEATURE [App::DocumentObjectGroupPython] H_element134  label="H_element : 081"  # scripted group (container) (typed FeaturePython)
  n = 10
  ref = H_element
FEATURE [App::DocumentObjectGroupPython] C_element144  label="C_element : 089"  # scripted group (container) (typed FeaturePython)
  n = 10
  ref = C_element
FEATURE [App::DocumentObjectGroupPython] N_element064  label="N_element : 036"  # scripted group (container) (typed FeaturePython)
  n = 5
  ref = N_element
FEATURE [App::DocumentObjectGroupPython] O_element126  label="O_element : 079"  # scripted group (container) (typed FeaturePython)
  n = 7
  ref = O_element
FEATURE [App::DocumentObjectGroupPython] P_element015  label="P_element : 004"  # scripted group (container) (typed FeaturePython)
  n = 1
  ref = P_element
FEATURE [App::DocumentObjectGroupPython] G4_DNA_A  # scripted group (container) (typed FeaturePython)
  Dunit = g/cm3
  Dvalue = 1
  Group = -> [H_element134,C_element144,N_element064,O_element126,P_element015]
  conduct = 2
  density = 1
  expand = 3
  formula = G4_DNA_A
  name = G4_DNA_A
  specific = 4
FEATURE [App::DocumentObjectGroupPython] H_element135  label="H_element : 082"  # scripted group (container) (typed FeaturePython)
  n = 10
  ref = H_element
FEATURE [App::DocumentObjectGroupPython] C_element145  label="C_element : 090"  # scripted group (container) (typed FeaturePython)
  n = 10
  ref = C_element
FEATURE [App::DocumentObjectGroupPython] N_element065  label="N_element : 037"  # scripted group (container) (typed FeaturePython)
  n = 5
  ref = N_element
FEATURE [App::DocumentObjectGroupPython] O_element127  label="O_element : 8"  # scripted group (container) (typed FeaturePython)
  n = 8
  ref = O_element
FEATURE [App::DocumentObjectGroupPython] P_element016  label="P_element : 005"  # scripted group (container) (typed FeaturePython)
  n = 1
  ref = P_element
FEATURE [App::DocumentObjectGroupPython] G4_DNA_G  # scripted group (container) (typed FeaturePython)
  Dunit = g/cm3
  Dvalue = 1
  Group = -> [H_element135,C_element145,N_element065,O_element127,P_element016]
  conduct = 2
  density = 1
  expand = 3
  formula = G4_DNA_G
  name = G4_DNA_G
  specific = 4
FEATURE [App::DocumentObjectGroupPython] H_element136  label="H_element : 083"  # scripted group (container) (typed FeaturePython)
  n = 10
  ref = H_element
FEATURE [App::DocumentObjectGroupPython] C_element146  label="C_element : 091"  # scripted group (container) (typed FeaturePython)
  n = 9
  ref = C_element
FEATURE [App::DocumentObjectGroupPython] N_element066  label="N_element : 038"  # scripted group (container) (typed FeaturePython)
  n = 3
  ref = N_element
FEATURE [App::DocumentObjectGroupPython] O_element128  label="O_element : 080"  # scripted group (container) (typed FeaturePython)
  n = 8
  ref = O_element
FEATURE [App::DocumentObjectGroupPython] P_element017  label="P_element : 006"  # scripted group (container) (typed FeaturePython)
  n = 1
  ref = P_element
FEATURE [App::DocumentObjectGroupPython] G4_DNA_C  # scripted group (container) (typed FeaturePython)
  Dunit = g/cm3
  Dvalue = 1
  Group = -> [H_element136,C_element146,N_element066,O_element128,P_element017]
  conduct = 2
  density = 1
  expand = 3
  formula = G4_DNA_C
  name = G4_DNA_C
  specific = 4
FEATURE [App::DocumentObjectGroupPython] H_element137  label="H_element : 084"  # scripted group (container) (typed FeaturePython)
  n = 9
  ref = H_element
FEATURE [App::DocumentObjectGroupPython] C_element147  label="C_element : 092"  # scripted group (container) (typed FeaturePython)
  n = 9
  ref = C_element
FEATURE [App::DocumentObjectGroupPython] N_element067  label="N_element : 039"  # scripted group (container) (typed FeaturePython)
  n = 2
  ref = N_element
FEATURE [App::DocumentObjectGroupPython] O_element129  label="O_element : 9"  # scripted group (container) (typed FeaturePython)
  n = 9
  ref = O_element
FEATURE [App::DocumentObjectGroupPython] P_element018  label="P_element : 007"  # scripted group (container) (typed FeaturePython)
  n = 1
  ref = P_element
FEATURE [App::DocumentObjectGroupPython] G4_DNA_U  # scripted group (container) (typed FeaturePython)
  Dunit = g/cm3
  Dvalue = 1
  Group = -> [H_element137,C_element147,N_element067,O_element129,P_element018]
  conduct = 2
  density = 1
  expand = 3
  formula = G4_DNA_U
  name = G4_DNA_U
  specific = 4
FEATURE [App::DocumentObjectGroupPython] H_element138  label="H_element : 085"  # scripted group (container) (typed FeaturePython)
  n = 11
  ref = H_element
FEATURE [App::DocumentObjectGroupPython] C_element148  label="C_element : 093"  # scripted group (container) (typed FeaturePython)
  n = 10
  ref = C_element
FEATURE [App::DocumentObjectGroupPython] N_element068  label="N_element : 040"  # scripted group (container) (typed FeaturePython)
  n = 2
  ref = N_element
FEATURE [App::DocumentObjectGroupPython] O_element130  label="O_element : 081"  # scripted group (container) (typed FeaturePython)
  n = 9
  ref = O_element
FEATURE [App::DocumentObjectGroupPython] P_element019  label="P_element : 008"  # scripted group (container) (typed FeaturePython)
  n = 1
  ref = P_element
FEATURE [App::DocumentObjectGroupPython] G4_DNA_MU  # scripted group (container) (typed FeaturePython)
  Dunit = g/cm3
  Dvalue = 1
  Group = -> [H_element138,C_element148,N_element068,O_element130,P_element019]
  conduct = 2
  density = 1
  expand = 3
  formula = G4_DNA_MU
  name = G4_DNA_MU
  specific = 4
FEATURE [App::DocumentObjectGroupPython] BioChemical  # scripted group (container) (typed FeaturePython)
  Group = -> [G4_CYTOSINE,G4_THYMINE,G4_URACIL,G4_DNA_ADENINE,G4_DNA_GUANINE,G4_DNA_CYTOSINE,G4_DNA_THYMINE,G4_DNA_URACIL,G4_DNA_ADENOSINE,G4_DNA_GUANOSINE,G4_DNA_CYTIDINE,G4_DNA_URIDINE,G4_DNA_METHYLURIDINE,G4_DNA_MONOPHOSPHATE,G4_DNA_A,G4_DNA_G,G4_DNA_C,G4_DNA_U,G4_DNA_MU]
FEATURE [App::DocumentObjectGroupPython] G4Materials  # scripted group (container) (typed FeaturePython)
  Group = -> [NIST,Element,HEP,Space,BioChemical]
  version = 1
FEATURE [App::DocumentObjectGroupPython] Geant4  # scripted group (container) (typed FeaturePython)
  Group = -> [G4Isotopes,G4Elements,G4Materials]
FEATURE [App::DocumentObjectGroupPython] Materials  # scripted group (container) (typed FeaturePython)
  Group = -> [Geant4]
FEATURE [Part::FeaturePython] GDMLBox_WorldBox  # WARN: FeaturePython — macro-defined, semantics opaque (R4)
  lunit = 2
  material = 5
  x = 273
  y = 273
  z = 130
FEATURE [Part::FeaturePython] GDMLBox_Box  # WARN: FeaturePython — macro-defined, semantics opaque (R4)
  Placement = pos=(20,0,0) rot=(0,0,1;0rad)
  lunit = 2
  material = 0
  x = 10
  y = 10
  z = 10
FEATURE [Part::FeaturePython] GDMLTube  # WARN: FeaturePython — macro-defined, semantics opaque (R4)
  Placement = pos=(17,-4,0) rot=(0,0,1;0rad)
  aunit = 1
  deltaphi = 90
  lunit = 2
  material = 0
  rmax = 7
  rmin = 5
  startphi = 0
  z = 7
FEATURE [App::Part] LV_Tube
  Group = -> [GDMLTube]
  Origin = -> Origin003
  SkinSurface = 0
FEATURE [App::Part] LV_Box
  Group = -> [GDMLBox_Box,LV_Tube]
  Origin = -> Origin002
  Placement = pos=(0,0,0) rot=(0,0,1;-0.523599rad)
FEATURE [Part::FeaturePython] Array  # Draft array (typed FeaturePython)
  AlwaysSyncPlacement = false
  Angle = 180
  ArrayType = 1
  Axis = (0,0,1)
  Base = -> LV_Box
  Center = (0,0,0)
  Count = 5
  ExpandArray = false
  Fuse = false
  IntervalAxis = (0,0,0)
  IntervalX = (100,0,0)
  IntervalY = (0,100,0)
  IntervalZ = (0,0,100)
  NumberCircles = 3
  NumberPolar = 5
  NumberX = 2
  NumberY = 2
  NumberZ = 1
  PlacementList = 5 placements: [(0,0,0),(0,0,0),(0,0,0),(0,0,0),(0,0,0)]
  RadialDistance = 50
  ScaleList = (5) [(1,1,1),(1,1,1),(1,1,1),(1,1,1),(1,1,1)]
  Symmetry = 1
  TangentialDistance = 25
FEATURE [App::Part] Part  label="experiment"
  Group = -> [LV_Box,Array]
  Origin = -> Origin001
FEATURE [App::Part] worldVOL
  Group = -> [GDMLBox_WorldBox,Part]
  Origin = -> Origin
